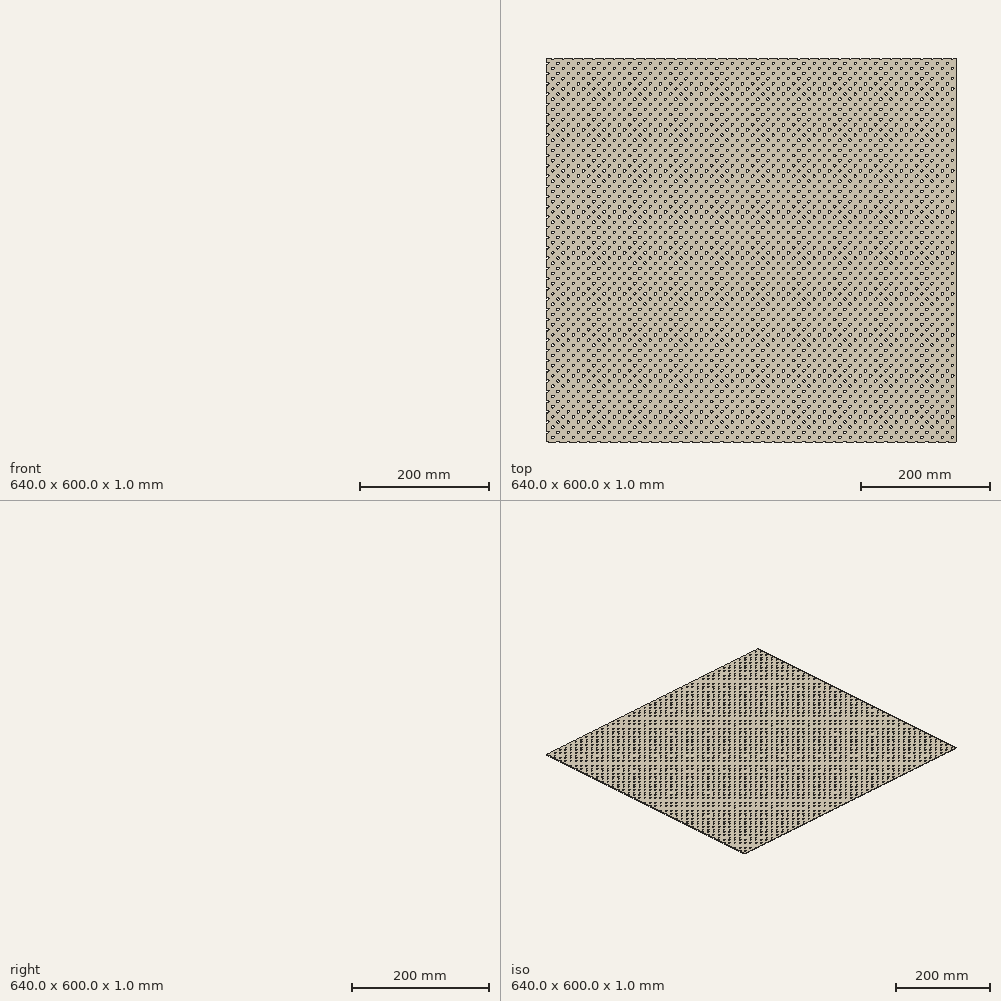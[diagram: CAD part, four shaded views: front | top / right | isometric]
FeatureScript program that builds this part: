
annotation { "Feature Type Name" : "Feature", "Feature Type Description" : "" }
export const myFeature = defineFeature(function(context is Context, id is Id, definition is map)
    precondition{}
    {
        {
            var Q0;
            Q0=qCreatedBy(makeId("Top.planeOp"),FACE);
            var sketch = newSketch(context, id + "F0", { "sketchPlane" : qUnion([Q0])});
            skLineSegment(sketch, "E0.bottom", {"start": v(320, -300) * mm, "end": v(-320, -300) * mm});
            skLineSegment(sketch, "E0.top", {"start": v(320, 300) * mm, "end": v(-320, 300) * mm});
            skLineSegment(sketch, "E0.left", {"start": v(320, -300) * mm, "end": v(320, 300) * mm});
            skLineSegment(sketch, "E0.right", {"start": v(-320, -300) * mm, "end": v(-320, 300) * mm});
            skPoint(sketch, "E0.middle", {"position": v(0, 0) * mm});
            skCircle(sketch, "E1", {"center": v(-317.9, -299.9) * mm, "radius": 2 * mm});
            skCircle(sketch, "E2.0.1.0", {"center": v(-317.9, -283.9) * mm, "radius": 2 * mm});
            skCircle(sketch, "E2.0.2.0", {"center": v(-317.9, -267.9) * mm, "radius": 2 * mm});
            skCircle(sketch, "E2.0.3.0", {"center": v(-317.9, -251.9) * mm, "radius": 2 * mm});
            skCircle(sketch, "E2.0.4.0", {"center": v(-317.9, -235.9) * mm, "radius": 2 * mm});
            skCircle(sketch, "E2.0.5.0", {"center": v(-317.9, -219.9) * mm, "radius": 2 * mm});
            skCircle(sketch, "E2.0.6.0", {"center": v(-317.9, -203.9) * mm, "radius": 2 * mm});
            skCircle(sketch, "E2.0.7.0", {"center": v(-317.9, -187.9) * mm, "radius": 2 * mm});
            skCircle(sketch, "E2.1.0.0", {"center": v(-301.9, -299.9) * mm, "radius": 2 * mm});
            skCircle(sketch, "E2.1.1.0", {"center": v(-301.9, -283.9) * mm, "radius": 2 * mm});
            skCircle(sketch, "E2.1.2.0", {"center": v(-301.9, -267.9) * mm, "radius": 2 * mm});
            skCircle(sketch, "E2.1.3.0", {"center": v(-301.9, -251.9) * mm, "radius": 2 * mm});
            skCircle(sketch, "E2.1.4.0", {"center": v(-301.9, -235.9) * mm, "radius": 2 * mm});
            skCircle(sketch, "E2.1.5.0", {"center": v(-301.9, -219.9) * mm, "radius": 2 * mm});
            skCircle(sketch, "E2.1.6.0", {"center": v(-301.9, -203.9) * mm, "radius": 2 * mm});
            skCircle(sketch, "E2.1.7.0", {"center": v(-301.9, -187.9) * mm, "radius": 2 * mm});
            skCircle(sketch, "E2.2.0.0", {"center": v(-285.9, -299.9) * mm, "radius": 2 * mm});
            skCircle(sketch, "E2.2.1.0", {"center": v(-285.9, -283.9) * mm, "radius": 2 * mm});
            skCircle(sketch, "E2.2.2.0", {"center": v(-285.9, -267.9) * mm, "radius": 2 * mm});
            skCircle(sketch, "E2.2.3.0", {"center": v(-285.9, -251.9) * mm, "radius": 2 * mm});
            skCircle(sketch, "E2.2.4.0", {"center": v(-285.9, -235.9) * mm, "radius": 2 * mm});
            skCircle(sketch, "E2.2.5.0", {"center": v(-285.9, -219.9) * mm, "radius": 2 * mm});
            skCircle(sketch, "E2.2.6.0", {"center": v(-285.9, -203.9) * mm, "radius": 2 * mm});
            skCircle(sketch, "E2.2.7.0", {"center": v(-285.9, -187.9) * mm, "radius": 2 * mm});
            skCircle(sketch, "E2.3.0.0", {"center": v(-269.9, -299.9) * mm, "radius": 2 * mm});
            skCircle(sketch, "E2.3.1.0", {"center": v(-269.9, -283.9) * mm, "radius": 2 * mm});
            skCircle(sketch, "E2.3.2.0", {"center": v(-269.9, -267.9) * mm, "radius": 2 * mm});
            skCircle(sketch, "E2.3.3.0", {"center": v(-269.9, -251.9) * mm, "radius": 2 * mm});
            skCircle(sketch, "E2.3.4.0", {"center": v(-269.9, -235.9) * mm, "radius": 2 * mm});
            skCircle(sketch, "E2.3.5.0", {"center": v(-269.9, -219.9) * mm, "radius": 2 * mm});
            skCircle(sketch, "E2.3.6.0", {"center": v(-269.9, -203.9) * mm, "radius": 2 * mm});
            skCircle(sketch, "E2.3.7.0", {"center": v(-269.9, -187.9) * mm, "radius": 2 * mm});
            skCircle(sketch, "E2.4.0.0", {"center": v(-253.9, -299.9) * mm, "radius": 2 * mm});
            skCircle(sketch, "E2.4.1.0", {"center": v(-253.9, -283.9) * mm, "radius": 2 * mm});
            skCircle(sketch, "E2.4.2.0", {"center": v(-253.9, -267.9) * mm, "radius": 2 * mm});
            skCircle(sketch, "E2.4.3.0", {"center": v(-253.9, -251.9) * mm, "radius": 2 * mm});
            skCircle(sketch, "E2.4.4.0", {"center": v(-253.9, -235.9) * mm, "radius": 2 * mm});
            skCircle(sketch, "E2.4.5.0", {"center": v(-253.9, -219.9) * mm, "radius": 2 * mm});
            skCircle(sketch, "E2.4.6.0", {"center": v(-253.9, -203.9) * mm, "radius": 2 * mm});
            skCircle(sketch, "E2.4.7.0", {"center": v(-253.9, -187.9) * mm, "radius": 2 * mm});
            skCircle(sketch, "E2.5.0.0", {"center": v(-237.9, -299.9) * mm, "radius": 2 * mm});
            skCircle(sketch, "E2.5.1.0", {"center": v(-237.9, -283.9) * mm, "radius": 2 * mm});
            skCircle(sketch, "E2.5.2.0", {"center": v(-237.9, -267.9) * mm, "radius": 2 * mm});
            skCircle(sketch, "E2.5.3.0", {"center": v(-237.9, -251.9) * mm, "radius": 2 * mm});
            skCircle(sketch, "E2.5.4.0", {"center": v(-237.9, -235.9) * mm, "radius": 2 * mm});
            skCircle(sketch, "E2.5.5.0", {"center": v(-237.9, -219.9) * mm, "radius": 2 * mm});
            skCircle(sketch, "E2.5.6.0", {"center": v(-237.9, -203.9) * mm, "radius": 2 * mm});
            skCircle(sketch, "E2.5.7.0", {"center": v(-237.9, -187.9) * mm, "radius": 2 * mm});
            skCircle(sketch, "E2.6.0.0", {"center": v(-221.9, -299.9) * mm, "radius": 2 * mm});
            skCircle(sketch, "E2.6.1.0", {"center": v(-221.9, -283.9) * mm, "radius": 2 * mm});
            skCircle(sketch, "E2.6.2.0", {"center": v(-221.9, -267.9) * mm, "radius": 2 * mm});
            skCircle(sketch, "E2.6.3.0", {"center": v(-221.9, -251.9) * mm, "radius": 2 * mm});
            skCircle(sketch, "E2.6.4.0", {"center": v(-221.9, -235.9) * mm, "radius": 2 * mm});
            skCircle(sketch, "E2.6.5.0", {"center": v(-221.9, -219.9) * mm, "radius": 2 * mm});
            skCircle(sketch, "E2.6.6.0", {"center": v(-221.9, -203.9) * mm, "radius": 2 * mm});
            skCircle(sketch, "E2.6.7.0", {"center": v(-221.9, -187.9) * mm, "radius": 2 * mm});
            skCircle(sketch, "E2.7.0.0", {"center": v(-205.9, -299.9) * mm, "radius": 2 * mm});
            skCircle(sketch, "E2.7.1.0", {"center": v(-205.9, -283.9) * mm, "radius": 2 * mm});
            skCircle(sketch, "E2.7.2.0", {"center": v(-205.9, -267.9) * mm, "radius": 2 * mm});
            skCircle(sketch, "E2.7.3.0", {"center": v(-205.9, -251.9) * mm, "radius": 2 * mm});
            skCircle(sketch, "E2.7.4.0", {"center": v(-205.9, -235.9) * mm, "radius": 2 * mm});
            skCircle(sketch, "E2.7.5.0", {"center": v(-205.9, -219.9) * mm, "radius": 2 * mm});
            skCircle(sketch, "E2.7.6.0", {"center": v(-205.9, -203.9) * mm, "radius": 2 * mm});
            skCircle(sketch, "E2.7.7.0", {"center": v(-205.9, -187.9) * mm, "radius": 2 * mm});
            skCircle(sketch, "E2.8.0.0", {"center": v(-189.9, -299.9) * mm, "radius": 2 * mm});
            skCircle(sketch, "E2.8.1.0", {"center": v(-189.9, -283.9) * mm, "radius": 2 * mm});
            skCircle(sketch, "E2.8.2.0", {"center": v(-189.9, -267.9) * mm, "radius": 2 * mm});
            skCircle(sketch, "E2.8.3.0", {"center": v(-189.9, -251.9) * mm, "radius": 2 * mm});
            skCircle(sketch, "E2.8.4.0", {"center": v(-189.9, -235.9) * mm, "radius": 2 * mm});
            skCircle(sketch, "E2.8.5.0", {"center": v(-189.9, -219.9) * mm, "radius": 2 * mm});
            skCircle(sketch, "E2.8.6.0", {"center": v(-189.9, -203.9) * mm, "radius": 2 * mm});
            skCircle(sketch, "E2.8.7.0", {"center": v(-189.9, -187.9) * mm, "radius": 2 * mm});
            skCircle(sketch, "E2.9.0.0", {"center": v(-173.9, -299.9) * mm, "radius": 2 * mm});
            skCircle(sketch, "E2.9.1.0", {"center": v(-173.9, -283.9) * mm, "radius": 2 * mm});
            skCircle(sketch, "E2.9.2.0", {"center": v(-173.9, -267.9) * mm, "radius": 2 * mm});
            skCircle(sketch, "E2.9.3.0", {"center": v(-173.9, -251.9) * mm, "radius": 2 * mm});
            skCircle(sketch, "E2.9.4.0", {"center": v(-173.9, -235.9) * mm, "radius": 2 * mm});
            skCircle(sketch, "E2.9.5.0", {"center": v(-173.9, -219.9) * mm, "radius": 2 * mm});
            skCircle(sketch, "E2.9.6.0", {"center": v(-173.9, -203.9) * mm, "radius": 2 * mm});
            skCircle(sketch, "E2.9.7.0", {"center": v(-173.9, -187.9) * mm, "radius": 2 * mm});
            skCircle(sketch, "E2.10.0.0", {"center": v(-157.9, -299.9) * mm, "radius": 2 * mm});
            skCircle(sketch, "E2.10.1.0", {"center": v(-157.9, -283.9) * mm, "radius": 2 * mm});
            skCircle(sketch, "E2.10.2.0", {"center": v(-157.9, -267.9) * mm, "radius": 2 * mm});
            skCircle(sketch, "E2.10.3.0", {"center": v(-157.9, -251.9) * mm, "radius": 2 * mm});
            skCircle(sketch, "E2.10.4.0", {"center": v(-157.9, -235.9) * mm, "radius": 2 * mm});
            skCircle(sketch, "E2.10.5.0", {"center": v(-157.9, -219.9) * mm, "radius": 2 * mm});
            skCircle(sketch, "E2.10.6.0", {"center": v(-157.9, -203.9) * mm, "radius": 2 * mm});
            skCircle(sketch, "E2.10.7.0", {"center": v(-157.9, -187.9) * mm, "radius": 2 * mm});
            skCircle(sketch, "E2.11.0.0", {"center": v(-141.9, -299.9) * mm, "radius": 2 * mm});
            skCircle(sketch, "E2.11.1.0", {"center": v(-141.9, -283.9) * mm, "radius": 2 * mm});
            skCircle(sketch, "E2.11.2.0", {"center": v(-141.9, -267.9) * mm, "radius": 2 * mm});
            skCircle(sketch, "E2.11.3.0", {"center": v(-141.9, -251.9) * mm, "radius": 2 * mm});
            skCircle(sketch, "E2.11.4.0", {"center": v(-141.9, -235.9) * mm, "radius": 2 * mm});
            skCircle(sketch, "E2.11.5.0", {"center": v(-141.9, -219.9) * mm, "radius": 2 * mm});
            skCircle(sketch, "E2.11.6.0", {"center": v(-141.9, -203.9) * mm, "radius": 2 * mm});
            skCircle(sketch, "E2.11.7.0", {"center": v(-141.9, -187.9) * mm, "radius": 2 * mm});
            skCircle(sketch, "E2.12.0.0", {"center": v(-125.9, -299.9) * mm, "radius": 2 * mm});
            skCircle(sketch, "E2.12.1.0", {"center": v(-125.9, -283.9) * mm, "radius": 2 * mm});
            skCircle(sketch, "E2.12.2.0", {"center": v(-125.9, -267.9) * mm, "radius": 2 * mm});
            skCircle(sketch, "E2.12.3.0", {"center": v(-125.9, -251.9) * mm, "radius": 2 * mm});
            skCircle(sketch, "E2.12.4.0", {"center": v(-125.9, -235.9) * mm, "radius": 2 * mm});
            skCircle(sketch, "E2.12.5.0", {"center": v(-125.9, -219.9) * mm, "radius": 2 * mm});
            skCircle(sketch, "E2.12.6.0", {"center": v(-125.9, -203.9) * mm, "radius": 2 * mm});
            skCircle(sketch, "E2.12.7.0", {"center": v(-125.9, -187.9) * mm, "radius": 2 * mm});
            skCircle(sketch, "E2.13.0.0", {"center": v(-109.9, -299.9) * mm, "radius": 2 * mm});
            skCircle(sketch, "E2.13.1.0", {"center": v(-109.9, -283.9) * mm, "radius": 2 * mm});
            skCircle(sketch, "E2.13.2.0", {"center": v(-109.9, -267.9) * mm, "radius": 2 * mm});
            skCircle(sketch, "E2.13.3.0", {"center": v(-109.9, -251.9) * mm, "radius": 2 * mm});
            skCircle(sketch, "E2.13.4.0", {"center": v(-109.9, -235.9) * mm, "radius": 2 * mm});
            skCircle(sketch, "E2.13.5.0", {"center": v(-109.9, -219.9) * mm, "radius": 2 * mm});
            skCircle(sketch, "E2.13.6.0", {"center": v(-109.9, -203.9) * mm, "radius": 2 * mm});
            skCircle(sketch, "E2.13.7.0", {"center": v(-109.9, -187.9) * mm, "radius": 2 * mm});
            skCircle(sketch, "E2.14.0.0", {"center": v(-93.9, -299.9) * mm, "radius": 2 * mm});
            skCircle(sketch, "E2.14.1.0", {"center": v(-93.9, -283.9) * mm, "radius": 2 * mm});
            skCircle(sketch, "E2.14.2.0", {"center": v(-93.9, -267.9) * mm, "radius": 2 * mm});
            skCircle(sketch, "E2.14.3.0", {"center": v(-93.9, -251.9) * mm, "radius": 2 * mm});
            skCircle(sketch, "E2.14.4.0", {"center": v(-93.9, -235.9) * mm, "radius": 2 * mm});
            skCircle(sketch, "E2.14.5.0", {"center": v(-93.9, -219.9) * mm, "radius": 2 * mm});
            skCircle(sketch, "E2.14.6.0", {"center": v(-93.9, -203.9) * mm, "radius": 2 * mm});
            skCircle(sketch, "E2.14.7.0", {"center": v(-93.9, -187.9) * mm, "radius": 2 * mm});
            skCircle(sketch, "E2.15.0.0", {"center": v(-77.9, -299.9) * mm, "radius": 2 * mm});
            skCircle(sketch, "E2.15.1.0", {"center": v(-77.9, -283.9) * mm, "radius": 2 * mm});
            skCircle(sketch, "E2.15.2.0", {"center": v(-77.9, -267.9) * mm, "radius": 2 * mm});
            skCircle(sketch, "E2.15.3.0", {"center": v(-77.9, -251.9) * mm, "radius": 2 * mm});
            skCircle(sketch, "E2.15.4.0", {"center": v(-77.9, -235.9) * mm, "radius": 2 * mm});
            skCircle(sketch, "E2.15.5.0", {"center": v(-77.9, -219.9) * mm, "radius": 2 * mm});
            skCircle(sketch, "E2.15.6.0", {"center": v(-77.9, -203.9) * mm, "radius": 2 * mm});
            skCircle(sketch, "E2.15.7.0", {"center": v(-77.9, -187.9) * mm, "radius": 2 * mm});
            skCircle(sketch, "E2.16.0.0", {"center": v(-61.9, -299.9) * mm, "radius": 2 * mm});
            skCircle(sketch, "E2.16.1.0", {"center": v(-61.9, -283.9) * mm, "radius": 2 * mm});
            skCircle(sketch, "E2.16.2.0", {"center": v(-61.9, -267.9) * mm, "radius": 2 * mm});
            skCircle(sketch, "E2.16.3.0", {"center": v(-61.9, -251.9) * mm, "radius": 2 * mm});
            skCircle(sketch, "E2.16.4.0", {"center": v(-61.9, -235.9) * mm, "radius": 2 * mm});
            skCircle(sketch, "E2.16.5.0", {"center": v(-61.9, -219.9) * mm, "radius": 2 * mm});
            skCircle(sketch, "E2.16.6.0", {"center": v(-61.9, -203.9) * mm, "radius": 2 * mm});
            skCircle(sketch, "E2.16.7.0", {"center": v(-61.9, -187.9) * mm, "radius": 2 * mm});
            skCircle(sketch, "E2.17.0.0", {"center": v(-45.9, -299.9) * mm, "radius": 2 * mm});
            skCircle(sketch, "E2.17.1.0", {"center": v(-45.9, -283.9) * mm, "radius": 2 * mm});
            skCircle(sketch, "E2.17.2.0", {"center": v(-45.9, -267.9) * mm, "radius": 2 * mm});
            skCircle(sketch, "E2.17.3.0", {"center": v(-45.9, -251.9) * mm, "radius": 2 * mm});
            skCircle(sketch, "E2.17.4.0", {"center": v(-45.9, -235.9) * mm, "radius": 2 * mm});
            skCircle(sketch, "E2.17.5.0", {"center": v(-45.9, -219.9) * mm, "radius": 2 * mm});
            skCircle(sketch, "E2.17.6.0", {"center": v(-45.9, -203.9) * mm, "radius": 2 * mm});
            skCircle(sketch, "E2.17.7.0", {"center": v(-45.9, -187.9) * mm, "radius": 2 * mm});
            skCircle(sketch, "E2.18.0.0", {"center": v(-29.9, -299.9) * mm, "radius": 2 * mm});
            skCircle(sketch, "E2.18.1.0", {"center": v(-29.9, -283.9) * mm, "radius": 2 * mm});
            skCircle(sketch, "E2.18.2.0", {"center": v(-29.9, -267.9) * mm, "radius": 2 * mm});
            skCircle(sketch, "E2.18.3.0", {"center": v(-29.9, -251.9) * mm, "radius": 2 * mm});
            skCircle(sketch, "E2.18.4.0", {"center": v(-29.9, -235.9) * mm, "radius": 2 * mm});
            skCircle(sketch, "E2.18.5.0", {"center": v(-29.9, -219.9) * mm, "radius": 2 * mm});
            skCircle(sketch, "E2.18.6.0", {"center": v(-29.9, -203.9) * mm, "radius": 2 * mm});
            skCircle(sketch, "E2.18.7.0", {"center": v(-29.9, -187.9) * mm, "radius": 2 * mm});
            skCircle(sketch, "E2.19.0.0", {"center": v(-13.9, -299.9) * mm, "radius": 2 * mm});
            skCircle(sketch, "E2.19.1.0", {"center": v(-13.9, -283.9) * mm, "radius": 2 * mm});
            skCircle(sketch, "E2.19.2.0", {"center": v(-13.9, -267.9) * mm, "radius": 2 * mm});
            skCircle(sketch, "E2.19.3.0", {"center": v(-13.9, -251.9) * mm, "radius": 2 * mm});
            skCircle(sketch, "E2.19.4.0", {"center": v(-13.9, -235.9) * mm, "radius": 2 * mm});
            skCircle(sketch, "E2.19.5.0", {"center": v(-13.9, -219.9) * mm, "radius": 2 * mm});
            skCircle(sketch, "E2.19.6.0", {"center": v(-13.9, -203.9) * mm, "radius": 2 * mm});
            skCircle(sketch, "E2.19.7.0", {"center": v(-13.9, -187.9) * mm, "radius": 2 * mm});
            skCircle(sketch, "E2.20.0.0", {"center": v(2.1, -299.9) * mm, "radius": 2 * mm});
            skCircle(sketch, "E2.20.1.0", {"center": v(2.1, -283.9) * mm, "radius": 2 * mm});
            skCircle(sketch, "E2.20.2.0", {"center": v(2.1, -267.9) * mm, "radius": 2 * mm});
            skCircle(sketch, "E2.20.3.0", {"center": v(2.1, -251.9) * mm, "radius": 2 * mm});
            skCircle(sketch, "E2.20.4.0", {"center": v(2.1, -235.9) * mm, "radius": 2 * mm});
            skCircle(sketch, "E2.20.5.0", {"center": v(2.1, -219.9) * mm, "radius": 2 * mm});
            skCircle(sketch, "E2.20.6.0", {"center": v(2.1, -203.9) * mm, "radius": 2 * mm});
            skCircle(sketch, "E2.20.7.0", {"center": v(2.1, -187.9) * mm, "radius": 2 * mm});
            skCircle(sketch, "E2.21.0.0", {"center": v(18.1, -299.9) * mm, "radius": 2 * mm});
            skCircle(sketch, "E2.21.1.0", {"center": v(18.1, -283.9) * mm, "radius": 2 * mm});
            skCircle(sketch, "E2.21.2.0", {"center": v(18.1, -267.9) * mm, "radius": 2 * mm});
            skCircle(sketch, "E2.21.3.0", {"center": v(18.1, -251.9) * mm, "radius": 2 * mm});
            skCircle(sketch, "E2.21.4.0", {"center": v(18.1, -235.9) * mm, "radius": 2 * mm});
            skCircle(sketch, "E2.21.5.0", {"center": v(18.1, -219.9) * mm, "radius": 2 * mm});
            skCircle(sketch, "E2.21.6.0", {"center": v(18.1, -203.9) * mm, "radius": 2 * mm});
            skCircle(sketch, "E2.21.7.0", {"center": v(18.1, -187.9) * mm, "radius": 2 * mm});
            skCircle(sketch, "E2.22.0.0", {"center": v(34.1, -299.9) * mm, "radius": 2 * mm});
            skCircle(sketch, "E2.22.1.0", {"center": v(34.1, -283.9) * mm, "radius": 2 * mm});
            skCircle(sketch, "E2.22.2.0", {"center": v(34.1, -267.9) * mm, "radius": 2 * mm});
            skCircle(sketch, "E2.22.3.0", {"center": v(34.1, -251.9) * mm, "radius": 2 * mm});
            skCircle(sketch, "E2.22.4.0", {"center": v(34.1, -235.9) * mm, "radius": 2 * mm});
            skCircle(sketch, "E2.22.5.0", {"center": v(34.1, -219.9) * mm, "radius": 2 * mm});
            skCircle(sketch, "E2.22.6.0", {"center": v(34.1, -203.9) * mm, "radius": 2 * mm});
            skCircle(sketch, "E2.22.7.0", {"center": v(34.1, -187.9) * mm, "radius": 2 * mm});
            skCircle(sketch, "E2.23.0.0", {"center": v(50.1, -299.9) * mm, "radius": 2 * mm});
            skCircle(sketch, "E2.23.1.0", {"center": v(50.1, -283.9) * mm, "radius": 2 * mm});
            skCircle(sketch, "E2.23.2.0", {"center": v(50.1, -267.9) * mm, "radius": 2 * mm});
            skCircle(sketch, "E2.23.3.0", {"center": v(50.1, -251.9) * mm, "radius": 2 * mm});
            skCircle(sketch, "E2.23.4.0", {"center": v(50.1, -235.9) * mm, "radius": 2 * mm});
            skCircle(sketch, "E2.23.5.0", {"center": v(50.1, -219.9) * mm, "radius": 2 * mm});
            skCircle(sketch, "E2.23.6.0", {"center": v(50.1, -203.9) * mm, "radius": 2 * mm});
            skCircle(sketch, "E2.23.7.0", {"center": v(50.1, -187.9) * mm, "radius": 2 * mm});
            skCircle(sketch, "E2.24.0.0", {"center": v(66.1, -299.9) * mm, "radius": 2 * mm});
            skCircle(sketch, "E2.24.1.0", {"center": v(66.1, -283.9) * mm, "radius": 2 * mm});
            skCircle(sketch, "E2.24.2.0", {"center": v(66.1, -267.9) * mm, "radius": 2 * mm});
            skCircle(sketch, "E2.24.3.0", {"center": v(66.1, -251.9) * mm, "radius": 2 * mm});
            skCircle(sketch, "E2.24.4.0", {"center": v(66.1, -235.9) * mm, "radius": 2 * mm});
            skCircle(sketch, "E2.24.5.0", {"center": v(66.1, -219.9) * mm, "radius": 2 * mm});
            skCircle(sketch, "E2.24.6.0", {"center": v(66.1, -203.9) * mm, "radius": 2 * mm});
            skCircle(sketch, "E2.24.7.0", {"center": v(66.1, -187.9) * mm, "radius": 2 * mm});
            skCircle(sketch, "E2.25.0.0", {"center": v(82.1, -299.9) * mm, "radius": 2 * mm});
            skCircle(sketch, "E2.25.1.0", {"center": v(82.1, -283.9) * mm, "radius": 2 * mm});
            skCircle(sketch, "E2.25.2.0", {"center": v(82.1, -267.9) * mm, "radius": 2 * mm});
            skCircle(sketch, "E2.25.3.0", {"center": v(82.1, -251.9) * mm, "radius": 2 * mm});
            skCircle(sketch, "E2.25.4.0", {"center": v(82.1, -235.9) * mm, "radius": 2 * mm});
            skCircle(sketch, "E2.25.5.0", {"center": v(82.1, -219.9) * mm, "radius": 2 * mm});
            skCircle(sketch, "E2.25.6.0", {"center": v(82.1, -203.9) * mm, "radius": 2 * mm});
            skCircle(sketch, "E2.25.7.0", {"center": v(82.1, -187.9) * mm, "radius": 2 * mm});
            skCircle(sketch, "E2.26.0.0", {"center": v(98.1, -299.9) * mm, "radius": 2 * mm});
            skCircle(sketch, "E2.26.1.0", {"center": v(98.1, -283.9) * mm, "radius": 2 * mm});
            skCircle(sketch, "E2.26.2.0", {"center": v(98.1, -267.9) * mm, "radius": 2 * mm});
            skCircle(sketch, "E2.26.3.0", {"center": v(98.1, -251.9) * mm, "radius": 2 * mm});
            skCircle(sketch, "E2.26.4.0", {"center": v(98.1, -235.9) * mm, "radius": 2 * mm});
            skCircle(sketch, "E2.26.5.0", {"center": v(98.1, -219.9) * mm, "radius": 2 * mm});
            skCircle(sketch, "E2.26.6.0", {"center": v(98.1, -203.9) * mm, "radius": 2 * mm});
            skCircle(sketch, "E2.26.7.0", {"center": v(98.1, -187.9) * mm, "radius": 2 * mm});
            skCircle(sketch, "E2.27.0.0", {"center": v(114.1, -299.9) * mm, "radius": 2 * mm});
            skCircle(sketch, "E2.27.1.0", {"center": v(114.1, -283.9) * mm, "radius": 2 * mm});
            skCircle(sketch, "E2.27.2.0", {"center": v(114.1, -267.9) * mm, "radius": 2 * mm});
            skCircle(sketch, "E2.27.3.0", {"center": v(114.1, -251.9) * mm, "radius": 2 * mm});
            skCircle(sketch, "E2.27.4.0", {"center": v(114.1, -235.9) * mm, "radius": 2 * mm});
            skCircle(sketch, "E2.27.5.0", {"center": v(114.1, -219.9) * mm, "radius": 2 * mm});
            skCircle(sketch, "E2.27.6.0", {"center": v(114.1, -203.9) * mm, "radius": 2 * mm});
            skCircle(sketch, "E2.27.7.0", {"center": v(114.1, -187.9) * mm, "radius": 2 * mm});
            skCircle(sketch, "E2.28.0.0", {"center": v(130.1, -299.9) * mm, "radius": 2 * mm});
            skCircle(sketch, "E2.28.1.0", {"center": v(130.1, -283.9) * mm, "radius": 2 * mm});
            skCircle(sketch, "E2.28.2.0", {"center": v(130.1, -267.9) * mm, "radius": 2 * mm});
            skCircle(sketch, "E2.28.3.0", {"center": v(130.1, -251.9) * mm, "radius": 2 * mm});
            skCircle(sketch, "E2.28.4.0", {"center": v(130.1, -235.9) * mm, "radius": 2 * mm});
            skCircle(sketch, "E2.28.5.0", {"center": v(130.1, -219.9) * mm, "radius": 2 * mm});
            skCircle(sketch, "E2.28.6.0", {"center": v(130.1, -203.9) * mm, "radius": 2 * mm});
            skCircle(sketch, "E2.28.7.0", {"center": v(130.1, -187.9) * mm, "radius": 2 * mm});
            skCircle(sketch, "E2.29.0.0", {"center": v(146.1, -299.9) * mm, "radius": 2 * mm});
            skCircle(sketch, "E2.29.1.0", {"center": v(146.1, -283.9) * mm, "radius": 2 * mm});
            skCircle(sketch, "E2.29.2.0", {"center": v(146.1, -267.9) * mm, "radius": 2 * mm});
            skCircle(sketch, "E2.29.3.0", {"center": v(146.1, -251.9) * mm, "radius": 2 * mm});
            skCircle(sketch, "E2.29.4.0", {"center": v(146.1, -235.9) * mm, "radius": 2 * mm});
            skCircle(sketch, "E2.29.5.0", {"center": v(146.1, -219.9) * mm, "radius": 2 * mm});
            skCircle(sketch, "E2.29.6.0", {"center": v(146.1, -203.9) * mm, "radius": 2 * mm});
            skCircle(sketch, "E2.29.7.0", {"center": v(146.1, -187.9) * mm, "radius": 2 * mm});
            skCircle(sketch, "E2.30.0.0", {"center": v(162.1, -299.9) * mm, "radius": 2 * mm});
            skCircle(sketch, "E2.30.1.0", {"center": v(162.1, -283.9) * mm, "radius": 2 * mm});
            skCircle(sketch, "E2.30.2.0", {"center": v(162.1, -267.9) * mm, "radius": 2 * mm});
            skCircle(sketch, "E2.30.3.0", {"center": v(162.1, -251.9) * mm, "radius": 2 * mm});
            skCircle(sketch, "E2.30.4.0", {"center": v(162.1, -235.9) * mm, "radius": 2 * mm});
            skCircle(sketch, "E2.30.5.0", {"center": v(162.1, -219.9) * mm, "radius": 2 * mm});
            skCircle(sketch, "E2.30.6.0", {"center": v(162.1, -203.9) * mm, "radius": 2 * mm});
            skCircle(sketch, "E2.30.7.0", {"center": v(162.1, -187.9) * mm, "radius": 2 * mm});
            skCircle(sketch, "E2.31.0.0", {"center": v(178.1, -299.9) * mm, "radius": 2 * mm});
            skCircle(sketch, "E2.31.1.0", {"center": v(178.1, -283.9) * mm, "radius": 2 * mm});
            skCircle(sketch, "E2.31.2.0", {"center": v(178.1, -267.9) * mm, "radius": 2 * mm});
            skCircle(sketch, "E2.31.3.0", {"center": v(178.1, -251.9) * mm, "radius": 2 * mm});
            skCircle(sketch, "E2.31.4.0", {"center": v(178.1, -235.9) * mm, "radius": 2 * mm});
            skCircle(sketch, "E2.31.5.0", {"center": v(178.1, -219.9) * mm, "radius": 2 * mm});
            skCircle(sketch, "E2.31.6.0", {"center": v(178.1, -203.9) * mm, "radius": 2 * mm});
            skCircle(sketch, "E2.31.7.0", {"center": v(178.1, -187.9) * mm, "radius": 2 * mm});
            skCircle(sketch, "E2.32.0.0", {"center": v(194.1, -299.9) * mm, "radius": 2 * mm});
            skCircle(sketch, "E2.32.1.0", {"center": v(194.1, -283.9) * mm, "radius": 2 * mm});
            skCircle(sketch, "E2.32.2.0", {"center": v(194.1, -267.9) * mm, "radius": 2 * mm});
            skCircle(sketch, "E2.32.3.0", {"center": v(194.1, -251.9) * mm, "radius": 2 * mm});
            skCircle(sketch, "E2.32.4.0", {"center": v(194.1, -235.9) * mm, "radius": 2 * mm});
            skCircle(sketch, "E2.32.5.0", {"center": v(194.1, -219.9) * mm, "radius": 2 * mm});
            skCircle(sketch, "E2.32.6.0", {"center": v(194.1, -203.9) * mm, "radius": 2 * mm});
            skCircle(sketch, "E2.32.7.0", {"center": v(194.1, -187.9) * mm, "radius": 2 * mm});
            skCircle(sketch, "E2.33.0.0", {"center": v(210.1, -299.9) * mm, "radius": 2 * mm});
            skCircle(sketch, "E2.33.1.0", {"center": v(210.1, -283.9) * mm, "radius": 2 * mm});
            skCircle(sketch, "E2.33.2.0", {"center": v(210.1, -267.9) * mm, "radius": 2 * mm});
            skCircle(sketch, "E2.33.3.0", {"center": v(210.1, -251.9) * mm, "radius": 2 * mm});
            skCircle(sketch, "E2.33.4.0", {"center": v(210.1, -235.9) * mm, "radius": 2 * mm});
            skCircle(sketch, "E2.33.5.0", {"center": v(210.1, -219.9) * mm, "radius": 2 * mm});
            skCircle(sketch, "E2.33.6.0", {"center": v(210.1, -203.9) * mm, "radius": 2 * mm});
            skCircle(sketch, "E2.33.7.0", {"center": v(210.1, -187.9) * mm, "radius": 2 * mm});
            skCircle(sketch, "E2.34.0.0", {"center": v(226.1, -299.9) * mm, "radius": 2 * mm});
            skCircle(sketch, "E2.34.1.0", {"center": v(226.1, -283.9) * mm, "radius": 2 * mm});
            skCircle(sketch, "E2.34.2.0", {"center": v(226.1, -267.9) * mm, "radius": 2 * mm});
            skCircle(sketch, "E2.34.3.0", {"center": v(226.1, -251.9) * mm, "radius": 2 * mm});
            skCircle(sketch, "E2.34.4.0", {"center": v(226.1, -235.9) * mm, "radius": 2 * mm});
            skCircle(sketch, "E2.34.5.0", {"center": v(226.1, -219.9) * mm, "radius": 2 * mm});
            skCircle(sketch, "E2.34.6.0", {"center": v(226.1, -203.9) * mm, "radius": 2 * mm});
            skCircle(sketch, "E2.34.7.0", {"center": v(226.1, -187.9) * mm, "radius": 2 * mm});
            skCircle(sketch, "E2.35.0.0", {"center": v(242.1, -299.9) * mm, "radius": 2 * mm});
            skCircle(sketch, "E2.35.1.0", {"center": v(242.1, -283.9) * mm, "radius": 2 * mm});
            skCircle(sketch, "E2.35.2.0", {"center": v(242.1, -267.9) * mm, "radius": 2 * mm});
            skCircle(sketch, "E2.35.3.0", {"center": v(242.1, -251.9) * mm, "radius": 2 * mm});
            skCircle(sketch, "E2.35.4.0", {"center": v(242.1, -235.9) * mm, "radius": 2 * mm});
            skCircle(sketch, "E2.35.5.0", {"center": v(242.1, -219.9) * mm, "radius": 2 * mm});
            skCircle(sketch, "E2.35.6.0", {"center": v(242.1, -203.9) * mm, "radius": 2 * mm});
            skCircle(sketch, "E2.35.7.0", {"center": v(242.1, -187.9) * mm, "radius": 2 * mm});
            skCircle(sketch, "E2.36.0.0", {"center": v(258.1, -299.9) * mm, "radius": 2 * mm});
            skCircle(sketch, "E2.36.1.0", {"center": v(258.1, -283.9) * mm, "radius": 2 * mm});
            skCircle(sketch, "E2.36.2.0", {"center": v(258.1, -267.9) * mm, "radius": 2 * mm});
            skCircle(sketch, "E2.36.3.0", {"center": v(258.1, -251.9) * mm, "radius": 2 * mm});
            skCircle(sketch, "E2.36.4.0", {"center": v(258.1, -235.9) * mm, "radius": 2 * mm});
            skCircle(sketch, "E2.36.5.0", {"center": v(258.1, -219.9) * mm, "radius": 2 * mm});
            skCircle(sketch, "E2.36.6.0", {"center": v(258.1, -203.9) * mm, "radius": 2 * mm});
            skCircle(sketch, "E2.36.7.0", {"center": v(258.1, -187.9) * mm, "radius": 2 * mm});
            skCircle(sketch, "E2.37.0.0", {"center": v(274.1, -299.9) * mm, "radius": 2 * mm});
            skCircle(sketch, "E2.37.1.0", {"center": v(274.1, -283.9) * mm, "radius": 2 * mm});
            skCircle(sketch, "E2.37.2.0", {"center": v(274.1, -267.9) * mm, "radius": 2 * mm});
            skCircle(sketch, "E2.37.3.0", {"center": v(274.1, -251.9) * mm, "radius": 2 * mm});
            skCircle(sketch, "E2.37.4.0", {"center": v(274.1, -235.9) * mm, "radius": 2 * mm});
            skCircle(sketch, "E2.37.5.0", {"center": v(274.1, -219.9) * mm, "radius": 2 * mm});
            skCircle(sketch, "E2.37.6.0", {"center": v(274.1, -203.9) * mm, "radius": 2 * mm});
            skCircle(sketch, "E2.37.7.0", {"center": v(274.1, -187.9) * mm, "radius": 2 * mm});
            skCircle(sketch, "E2.38.0.0", {"center": v(290.1, -299.9) * mm, "radius": 2 * mm});
            skCircle(sketch, "E2.38.1.0", {"center": v(290.1, -283.9) * mm, "radius": 2 * mm});
            skCircle(sketch, "E2.38.2.0", {"center": v(290.1, -267.9) * mm, "radius": 2 * mm});
            skCircle(sketch, "E2.38.3.0", {"center": v(290.1, -251.9) * mm, "radius": 2 * mm});
            skCircle(sketch, "E2.38.4.0", {"center": v(290.1, -235.9) * mm, "radius": 2 * mm});
            skCircle(sketch, "E2.38.5.0", {"center": v(290.1, -219.9) * mm, "radius": 2 * mm});
            skCircle(sketch, "E2.38.6.0", {"center": v(290.1, -203.9) * mm, "radius": 2 * mm});
            skCircle(sketch, "E2.38.7.0", {"center": v(290.1, -187.9) * mm, "radius": 2 * mm});
            skCircle(sketch, "E2.39.0.0", {"center": v(306.1, -299.9) * mm, "radius": 2 * mm});
            skCircle(sketch, "E2.39.1.0", {"center": v(306.1, -283.9) * mm, "radius": 2 * mm});
            skCircle(sketch, "E2.39.2.0", {"center": v(306.1, -267.9) * mm, "radius": 2 * mm});
            skCircle(sketch, "E2.39.3.0", {"center": v(306.1, -251.9) * mm, "radius": 2 * mm});
            skCircle(sketch, "E2.39.4.0", {"center": v(306.1, -235.9) * mm, "radius": 2 * mm});
            skCircle(sketch, "E2.39.5.0", {"center": v(306.1, -219.9) * mm, "radius": 2 * mm});
            skCircle(sketch, "E2.39.6.0", {"center": v(306.1, -203.9) * mm, "radius": 2 * mm});
            skCircle(sketch, "E2.39.7.0", {"center": v(306.1, -187.9) * mm, "radius": 2 * mm});
            skLineSegment(sketch, "E2.direction1", {"start": v(-317.9, -299.9) * mm, "end": v(-301.9, -299.9) * mm, "construction": true});
            skLineSegment(sketch, "E2.direction2", {"start": v(-317.9, -299.9) * mm, "end": v(-317.9, -283.9) * mm, "construction": true});
            skCircle(sketch, "E3", {"center": v(-309.9, -291.9) * mm, "radius": 2 * mm});
            skCircle(sketch, "E4.0.1.0", {"center": v(-309.9, -275.9) * mm, "radius": 2 * mm});
            skCircle(sketch, "E4.0.2.0", {"center": v(-309.9, -259.9) * mm, "radius": 2 * mm});
            skCircle(sketch, "E4.0.3.0", {"center": v(-309.9, -243.9) * mm, "radius": 2 * mm});
            skCircle(sketch, "E4.0.4.0", {"center": v(-309.9, -227.9) * mm, "radius": 2 * mm});
            skCircle(sketch, "E4.0.5.0", {"center": v(-309.9, -211.9) * mm, "radius": 2 * mm});
            skCircle(sketch, "E4.1.0.0", {"center": v(-293.9, -291.9) * mm, "radius": 2 * mm});
            skCircle(sketch, "E4.1.1.0", {"center": v(-293.9, -275.9) * mm, "radius": 2 * mm});
            skCircle(sketch, "E4.1.2.0", {"center": v(-293.9, -259.9) * mm, "radius": 2 * mm});
            skCircle(sketch, "E4.1.3.0", {"center": v(-293.9, -243.9) * mm, "radius": 2 * mm});
            skCircle(sketch, "E4.1.4.0", {"center": v(-293.9, -227.9) * mm, "radius": 2 * mm});
            skCircle(sketch, "E4.1.5.0", {"center": v(-293.9, -211.9) * mm, "radius": 2 * mm});
            skCircle(sketch, "E4.2.0.0", {"center": v(-277.9, -291.9) * mm, "radius": 2 * mm});
            skCircle(sketch, "E4.2.1.0", {"center": v(-277.9, -275.9) * mm, "radius": 2 * mm});
            skCircle(sketch, "E4.2.2.0", {"center": v(-277.9, -259.9) * mm, "radius": 2 * mm});
            skCircle(sketch, "E4.2.3.0", {"center": v(-277.9, -243.9) * mm, "radius": 2 * mm});
            skCircle(sketch, "E4.2.4.0", {"center": v(-277.9, -227.9) * mm, "radius": 2 * mm});
            skCircle(sketch, "E4.2.5.0", {"center": v(-277.9, -211.9) * mm, "radius": 2 * mm});
            skCircle(sketch, "E4.3.0.0", {"center": v(-261.9, -291.9) * mm, "radius": 2 * mm});
            skCircle(sketch, "E4.3.1.0", {"center": v(-261.9, -275.9) * mm, "radius": 2 * mm});
            skCircle(sketch, "E4.3.2.0", {"center": v(-261.9, -259.9) * mm, "radius": 2 * mm});
            skCircle(sketch, "E4.3.3.0", {"center": v(-261.9, -243.9) * mm, "radius": 2 * mm});
            skCircle(sketch, "E4.3.4.0", {"center": v(-261.9, -227.9) * mm, "radius": 2 * mm});
            skCircle(sketch, "E4.3.5.0", {"center": v(-261.9, -211.9) * mm, "radius": 2 * mm});
            skCircle(sketch, "E4.4.0.0", {"center": v(-245.9, -291.9) * mm, "radius": 2 * mm});
            skCircle(sketch, "E4.4.1.0", {"center": v(-245.9, -275.9) * mm, "radius": 2 * mm});
            skCircle(sketch, "E4.4.2.0", {"center": v(-245.9, -259.9) * mm, "radius": 2 * mm});
            skCircle(sketch, "E4.4.3.0", {"center": v(-245.9, -243.9) * mm, "radius": 2 * mm});
            skCircle(sketch, "E4.4.4.0", {"center": v(-245.9, -227.9) * mm, "radius": 2 * mm});
            skCircle(sketch, "E4.4.5.0", {"center": v(-245.9, -211.9) * mm, "radius": 2 * mm});
            skCircle(sketch, "E4.5.0.0", {"center": v(-229.9, -291.9) * mm, "radius": 2 * mm});
            skCircle(sketch, "E4.5.1.0", {"center": v(-229.9, -275.9) * mm, "radius": 2 * mm});
            skCircle(sketch, "E4.5.2.0", {"center": v(-229.9, -259.9) * mm, "radius": 2 * mm});
            skCircle(sketch, "E4.5.3.0", {"center": v(-229.9, -243.9) * mm, "radius": 2 * mm});
            skCircle(sketch, "E4.5.4.0", {"center": v(-229.9, -227.9) * mm, "radius": 2 * mm});
            skCircle(sketch, "E4.5.5.0", {"center": v(-229.9, -211.9) * mm, "radius": 2 * mm});
            skCircle(sketch, "E4.6.0.0", {"center": v(-213.9, -291.9) * mm, "radius": 2 * mm});
            skCircle(sketch, "E4.6.1.0", {"center": v(-213.9, -275.9) * mm, "radius": 2 * mm});
            skCircle(sketch, "E4.6.2.0", {"center": v(-213.9, -259.9) * mm, "radius": 2 * mm});
            skCircle(sketch, "E4.6.3.0", {"center": v(-213.9, -243.9) * mm, "radius": 2 * mm});
            skCircle(sketch, "E4.6.4.0", {"center": v(-213.9, -227.9) * mm, "radius": 2 * mm});
            skCircle(sketch, "E4.6.5.0", {"center": v(-213.9, -211.9) * mm, "radius": 2 * mm});
            skCircle(sketch, "E4.7.0.0", {"center": v(-197.9, -291.9) * mm, "radius": 2 * mm});
            skCircle(sketch, "E4.7.1.0", {"center": v(-197.9, -275.9) * mm, "radius": 2 * mm});
            skCircle(sketch, "E4.7.2.0", {"center": v(-197.9, -259.9) * mm, "radius": 2 * mm});
            skCircle(sketch, "E4.7.3.0", {"center": v(-197.9, -243.9) * mm, "radius": 2 * mm});
            skCircle(sketch, "E4.7.4.0", {"center": v(-197.9, -227.9) * mm, "radius": 2 * mm});
            skCircle(sketch, "E4.7.5.0", {"center": v(-197.9, -211.9) * mm, "radius": 2 * mm});
            skCircle(sketch, "E4.8.0.0", {"center": v(-181.9, -291.9) * mm, "radius": 2 * mm});
            skCircle(sketch, "E4.8.1.0", {"center": v(-181.9, -275.9) * mm, "radius": 2 * mm});
            skCircle(sketch, "E4.8.2.0", {"center": v(-181.9, -259.9) * mm, "radius": 2 * mm});
            skCircle(sketch, "E4.8.3.0", {"center": v(-181.9, -243.9) * mm, "radius": 2 * mm});
            skCircle(sketch, "E4.8.4.0", {"center": v(-181.9, -227.9) * mm, "radius": 2 * mm});
            skCircle(sketch, "E4.8.5.0", {"center": v(-181.9, -211.9) * mm, "radius": 2 * mm});
            skCircle(sketch, "E4.9.0.0", {"center": v(-165.9, -291.9) * mm, "radius": 2 * mm});
            skCircle(sketch, "E4.9.1.0", {"center": v(-165.9, -275.9) * mm, "radius": 2 * mm});
            skCircle(sketch, "E4.9.2.0", {"center": v(-165.9, -259.9) * mm, "radius": 2 * mm});
            skCircle(sketch, "E4.9.3.0", {"center": v(-165.9, -243.9) * mm, "radius": 2 * mm});
            skCircle(sketch, "E4.9.4.0", {"center": v(-165.9, -227.9) * mm, "radius": 2 * mm});
            skCircle(sketch, "E4.9.5.0", {"center": v(-165.9, -211.9) * mm, "radius": 2 * mm});
            skCircle(sketch, "E4.10.0.0", {"center": v(-149.9, -291.9) * mm, "radius": 2 * mm});
            skCircle(sketch, "E4.10.1.0", {"center": v(-149.9, -275.9) * mm, "radius": 2 * mm});
            skCircle(sketch, "E4.10.2.0", {"center": v(-149.9, -259.9) * mm, "radius": 2 * mm});
            skCircle(sketch, "E4.10.3.0", {"center": v(-149.9, -243.9) * mm, "radius": 2 * mm});
            skCircle(sketch, "E4.10.4.0", {"center": v(-149.9, -227.9) * mm, "radius": 2 * mm});
            skCircle(sketch, "E4.10.5.0", {"center": v(-149.9, -211.9) * mm, "radius": 2 * mm});
            skCircle(sketch, "E4.11.0.0", {"center": v(-133.9, -291.9) * mm, "radius": 2 * mm});
            skCircle(sketch, "E4.11.1.0", {"center": v(-133.9, -275.9) * mm, "radius": 2 * mm});
            skCircle(sketch, "E4.11.2.0", {"center": v(-133.9, -259.9) * mm, "radius": 2 * mm});
            skCircle(sketch, "E4.11.3.0", {"center": v(-133.9, -243.9) * mm, "radius": 2 * mm});
            skCircle(sketch, "E4.11.4.0", {"center": v(-133.9, -227.9) * mm, "radius": 2 * mm});
            skCircle(sketch, "E4.11.5.0", {"center": v(-133.9, -211.9) * mm, "radius": 2 * mm});
            skCircle(sketch, "E4.12.0.0", {"center": v(-117.9, -291.9) * mm, "radius": 2 * mm});
            skCircle(sketch, "E4.12.1.0", {"center": v(-117.9, -275.9) * mm, "radius": 2 * mm});
            skCircle(sketch, "E4.12.2.0", {"center": v(-117.9, -259.9) * mm, "radius": 2 * mm});
            skCircle(sketch, "E4.12.3.0", {"center": v(-117.9, -243.9) * mm, "radius": 2 * mm});
            skCircle(sketch, "E4.12.4.0", {"center": v(-117.9, -227.9) * mm, "radius": 2 * mm});
            skCircle(sketch, "E4.12.5.0", {"center": v(-117.9, -211.9) * mm, "radius": 2 * mm});
            skCircle(sketch, "E4.13.0.0", {"center": v(-101.9, -291.9) * mm, "radius": 2 * mm});
            skCircle(sketch, "E4.13.1.0", {"center": v(-101.9, -275.9) * mm, "radius": 2 * mm});
            skCircle(sketch, "E4.13.2.0", {"center": v(-101.9, -259.9) * mm, "radius": 2 * mm});
            skCircle(sketch, "E4.13.3.0", {"center": v(-101.9, -243.9) * mm, "radius": 2 * mm});
            skCircle(sketch, "E4.13.4.0", {"center": v(-101.9, -227.9) * mm, "radius": 2 * mm});
            skCircle(sketch, "E4.13.5.0", {"center": v(-101.9, -211.9) * mm, "radius": 2 * mm});
            skCircle(sketch, "E4.14.0.0", {"center": v(-85.9, -291.9) * mm, "radius": 2 * mm});
            skCircle(sketch, "E4.14.1.0", {"center": v(-85.9, -275.9) * mm, "radius": 2 * mm});
            skCircle(sketch, "E4.14.2.0", {"center": v(-85.9, -259.9) * mm, "radius": 2 * mm});
            skCircle(sketch, "E4.14.3.0", {"center": v(-85.9, -243.9) * mm, "radius": 2 * mm});
            skCircle(sketch, "E4.14.4.0", {"center": v(-85.9, -227.9) * mm, "radius": 2 * mm});
            skCircle(sketch, "E4.14.5.0", {"center": v(-85.9, -211.9) * mm, "radius": 2 * mm});
            skCircle(sketch, "E4.15.0.0", {"center": v(-69.9, -291.9) * mm, "radius": 2 * mm});
            skCircle(sketch, "E4.15.1.0", {"center": v(-69.9, -275.9) * mm, "radius": 2 * mm});
            skCircle(sketch, "E4.15.2.0", {"center": v(-69.9, -259.9) * mm, "radius": 2 * mm});
            skCircle(sketch, "E4.15.3.0", {"center": v(-69.9, -243.9) * mm, "radius": 2 * mm});
            skCircle(sketch, "E4.15.4.0", {"center": v(-69.9, -227.9) * mm, "radius": 2 * mm});
            skCircle(sketch, "E4.15.5.0", {"center": v(-69.9, -211.9) * mm, "radius": 2 * mm});
            skCircle(sketch, "E4.16.0.0", {"center": v(-53.9, -291.9) * mm, "radius": 2 * mm});
            skCircle(sketch, "E4.16.1.0", {"center": v(-53.9, -275.9) * mm, "radius": 2 * mm});
            skCircle(sketch, "E4.16.2.0", {"center": v(-53.9, -259.9) * mm, "radius": 2 * mm});
            skCircle(sketch, "E4.16.3.0", {"center": v(-53.9, -243.9) * mm, "radius": 2 * mm});
            skCircle(sketch, "E4.16.4.0", {"center": v(-53.9, -227.9) * mm, "radius": 2 * mm});
            skCircle(sketch, "E4.16.5.0", {"center": v(-53.9, -211.9) * mm, "radius": 2 * mm});
            skCircle(sketch, "E4.17.0.0", {"center": v(-37.9, -291.9) * mm, "radius": 2 * mm});
            skCircle(sketch, "E4.17.1.0", {"center": v(-37.9, -275.9) * mm, "radius": 2 * mm});
            skCircle(sketch, "E4.17.2.0", {"center": v(-37.9, -259.9) * mm, "radius": 2 * mm});
            skCircle(sketch, "E4.17.3.0", {"center": v(-37.9, -243.9) * mm, "radius": 2 * mm});
            skCircle(sketch, "E4.17.4.0", {"center": v(-37.9, -227.9) * mm, "radius": 2 * mm});
            skCircle(sketch, "E4.17.5.0", {"center": v(-37.9, -211.9) * mm, "radius": 2 * mm});
            skCircle(sketch, "E4.18.0.0", {"center": v(-21.9, -291.9) * mm, "radius": 2 * mm});
            skCircle(sketch, "E4.18.1.0", {"center": v(-21.9, -275.9) * mm, "radius": 2 * mm});
            skCircle(sketch, "E4.18.2.0", {"center": v(-21.9, -259.9) * mm, "radius": 2 * mm});
            skCircle(sketch, "E4.18.3.0", {"center": v(-21.9, -243.9) * mm, "radius": 2 * mm});
            skCircle(sketch, "E4.18.4.0", {"center": v(-21.9, -227.9) * mm, "radius": 2 * mm});
            skCircle(sketch, "E4.18.5.0", {"center": v(-21.9, -211.9) * mm, "radius": 2 * mm});
            skCircle(sketch, "E4.19.0.0", {"center": v(-5.9, -291.9) * mm, "radius": 2 * mm});
            skCircle(sketch, "E4.19.1.0", {"center": v(-5.9, -275.9) * mm, "radius": 2 * mm});
            skCircle(sketch, "E4.19.2.0", {"center": v(-5.9, -259.9) * mm, "radius": 2 * mm});
            skCircle(sketch, "E4.19.3.0", {"center": v(-5.9, -243.9) * mm, "radius": 2 * mm});
            skCircle(sketch, "E4.19.4.0", {"center": v(-5.9, -227.9) * mm, "radius": 2 * mm});
            skCircle(sketch, "E4.19.5.0", {"center": v(-5.9, -211.9) * mm, "radius": 2 * mm});
            skCircle(sketch, "E4.20.0.0", {"center": v(10.1, -291.9) * mm, "radius": 2 * mm});
            skCircle(sketch, "E4.20.1.0", {"center": v(10.1, -275.9) * mm, "radius": 2 * mm});
            skCircle(sketch, "E4.20.2.0", {"center": v(10.1, -259.9) * mm, "radius": 2 * mm});
            skCircle(sketch, "E4.20.3.0", {"center": v(10.1, -243.9) * mm, "radius": 2 * mm});
            skCircle(sketch, "E4.20.4.0", {"center": v(10.1, -227.9) * mm, "radius": 2 * mm});
            skCircle(sketch, "E4.20.5.0", {"center": v(10.1, -211.9) * mm, "radius": 2 * mm});
            skCircle(sketch, "E4.21.0.0", {"center": v(26.1, -291.9) * mm, "radius": 2 * mm});
            skCircle(sketch, "E4.21.1.0", {"center": v(26.1, -275.9) * mm, "radius": 2 * mm});
            skCircle(sketch, "E4.21.2.0", {"center": v(26.1, -259.9) * mm, "radius": 2 * mm});
            skCircle(sketch, "E4.21.3.0", {"center": v(26.1, -243.9) * mm, "radius": 2 * mm});
            skCircle(sketch, "E4.21.4.0", {"center": v(26.1, -227.9) * mm, "radius": 2 * mm});
            skCircle(sketch, "E4.21.5.0", {"center": v(26.1, -211.9) * mm, "radius": 2 * mm});
            skCircle(sketch, "E4.22.0.0", {"center": v(42.1, -291.9) * mm, "radius": 2 * mm});
            skCircle(sketch, "E4.22.1.0", {"center": v(42.1, -275.9) * mm, "radius": 2 * mm});
            skCircle(sketch, "E4.22.2.0", {"center": v(42.1, -259.9) * mm, "radius": 2 * mm});
            skCircle(sketch, "E4.22.3.0", {"center": v(42.1, -243.9) * mm, "radius": 2 * mm});
            skCircle(sketch, "E4.22.4.0", {"center": v(42.1, -227.9) * mm, "radius": 2 * mm});
            skCircle(sketch, "E4.22.5.0", {"center": v(42.1, -211.9) * mm, "radius": 2 * mm});
            skCircle(sketch, "E4.23.0.0", {"center": v(58.1, -291.9) * mm, "radius": 2 * mm});
            skCircle(sketch, "E4.23.1.0", {"center": v(58.1, -275.9) * mm, "radius": 2 * mm});
            skCircle(sketch, "E4.23.2.0", {"center": v(58.1, -259.9) * mm, "radius": 2 * mm});
            skCircle(sketch, "E4.23.3.0", {"center": v(58.1, -243.9) * mm, "radius": 2 * mm});
            skCircle(sketch, "E4.23.4.0", {"center": v(58.1, -227.9) * mm, "radius": 2 * mm});
            skCircle(sketch, "E4.23.5.0", {"center": v(58.1, -211.9) * mm, "radius": 2 * mm});
            skCircle(sketch, "E4.24.0.0", {"center": v(74.1, -291.9) * mm, "radius": 2 * mm});
            skCircle(sketch, "E4.24.1.0", {"center": v(74.1, -275.9) * mm, "radius": 2 * mm});
            skCircle(sketch, "E4.24.2.0", {"center": v(74.1, -259.9) * mm, "radius": 2 * mm});
            skCircle(sketch, "E4.24.3.0", {"center": v(74.1, -243.9) * mm, "radius": 2 * mm});
            skCircle(sketch, "E4.24.4.0", {"center": v(74.1, -227.9) * mm, "radius": 2 * mm});
            skCircle(sketch, "E4.24.5.0", {"center": v(74.1, -211.9) * mm, "radius": 2 * mm});
            skCircle(sketch, "E4.25.0.0", {"center": v(90.1, -291.9) * mm, "radius": 2 * mm});
            skCircle(sketch, "E4.25.1.0", {"center": v(90.1, -275.9) * mm, "radius": 2 * mm});
            skCircle(sketch, "E4.25.2.0", {"center": v(90.1, -259.9) * mm, "radius": 2 * mm});
            skCircle(sketch, "E4.25.3.0", {"center": v(90.1, -243.9) * mm, "radius": 2 * mm});
            skCircle(sketch, "E4.25.4.0", {"center": v(90.1, -227.9) * mm, "radius": 2 * mm});
            skCircle(sketch, "E4.25.5.0", {"center": v(90.1, -211.9) * mm, "radius": 2 * mm});
            skCircle(sketch, "E4.26.0.0", {"center": v(106.1, -291.9) * mm, "radius": 2 * mm});
            skCircle(sketch, "E4.26.1.0", {"center": v(106.1, -275.9) * mm, "radius": 2 * mm});
            skCircle(sketch, "E4.26.2.0", {"center": v(106.1, -259.9) * mm, "radius": 2 * mm});
            skCircle(sketch, "E4.26.3.0", {"center": v(106.1, -243.9) * mm, "radius": 2 * mm});
            skCircle(sketch, "E4.26.4.0", {"center": v(106.1, -227.9) * mm, "radius": 2 * mm});
            skCircle(sketch, "E4.26.5.0", {"center": v(106.1, -211.9) * mm, "radius": 2 * mm});
            skCircle(sketch, "E4.27.0.0", {"center": v(122.1, -291.9) * mm, "radius": 2 * mm});
            skCircle(sketch, "E4.27.1.0", {"center": v(122.1, -275.9) * mm, "radius": 2 * mm});
            skCircle(sketch, "E4.27.2.0", {"center": v(122.1, -259.9) * mm, "radius": 2 * mm});
            skCircle(sketch, "E4.27.3.0", {"center": v(122.1, -243.9) * mm, "radius": 2 * mm});
            skCircle(sketch, "E4.27.4.0", {"center": v(122.1, -227.9) * mm, "radius": 2 * mm});
            skCircle(sketch, "E4.27.5.0", {"center": v(122.1, -211.9) * mm, "radius": 2 * mm});
            skCircle(sketch, "E4.28.0.0", {"center": v(138.1, -291.9) * mm, "radius": 2 * mm});
            skCircle(sketch, "E4.28.1.0", {"center": v(138.1, -275.9) * mm, "radius": 2 * mm});
            skCircle(sketch, "E4.28.2.0", {"center": v(138.1, -259.9) * mm, "radius": 2 * mm});
            skCircle(sketch, "E4.28.3.0", {"center": v(138.1, -243.9) * mm, "radius": 2 * mm});
            skCircle(sketch, "E4.28.4.0", {"center": v(138.1, -227.9) * mm, "radius": 2 * mm});
            skCircle(sketch, "E4.28.5.0", {"center": v(138.1, -211.9) * mm, "radius": 2 * mm});
            skCircle(sketch, "E4.29.0.0", {"center": v(154.1, -291.9) * mm, "radius": 2 * mm});
            skCircle(sketch, "E4.29.1.0", {"center": v(154.1, -275.9) * mm, "radius": 2 * mm});
            skCircle(sketch, "E4.29.2.0", {"center": v(154.1, -259.9) * mm, "radius": 2 * mm});
            skCircle(sketch, "E4.29.3.0", {"center": v(154.1, -243.9) * mm, "radius": 2 * mm});
            skCircle(sketch, "E4.29.4.0", {"center": v(154.1, -227.9) * mm, "radius": 2 * mm});
            skCircle(sketch, "E4.29.5.0", {"center": v(154.1, -211.9) * mm, "radius": 2 * mm});
            skCircle(sketch, "E4.30.0.0", {"center": v(170.1, -291.9) * mm, "radius": 2 * mm});
            skCircle(sketch, "E4.30.1.0", {"center": v(170.1, -275.9) * mm, "radius": 2 * mm});
            skCircle(sketch, "E4.30.2.0", {"center": v(170.1, -259.9) * mm, "radius": 2 * mm});
            skCircle(sketch, "E4.30.3.0", {"center": v(170.1, -243.9) * mm, "radius": 2 * mm});
            skCircle(sketch, "E4.30.4.0", {"center": v(170.1, -227.9) * mm, "radius": 2 * mm});
            skCircle(sketch, "E4.30.5.0", {"center": v(170.1, -211.9) * mm, "radius": 2 * mm});
            skCircle(sketch, "E4.31.0.0", {"center": v(186.1, -291.9) * mm, "radius": 2 * mm});
            skCircle(sketch, "E4.31.1.0", {"center": v(186.1, -275.9) * mm, "radius": 2 * mm});
            skCircle(sketch, "E4.31.2.0", {"center": v(186.1, -259.9) * mm, "radius": 2 * mm});
            skCircle(sketch, "E4.31.3.0", {"center": v(186.1, -243.9) * mm, "radius": 2 * mm});
            skCircle(sketch, "E4.31.4.0", {"center": v(186.1, -227.9) * mm, "radius": 2 * mm});
            skCircle(sketch, "E4.31.5.0", {"center": v(186.1, -211.9) * mm, "radius": 2 * mm});
            skCircle(sketch, "E4.32.0.0", {"center": v(202.1, -291.9) * mm, "radius": 2 * mm});
            skCircle(sketch, "E4.32.1.0", {"center": v(202.1, -275.9) * mm, "radius": 2 * mm});
            skCircle(sketch, "E4.32.2.0", {"center": v(202.1, -259.9) * mm, "radius": 2 * mm});
            skCircle(sketch, "E4.32.3.0", {"center": v(202.1, -243.9) * mm, "radius": 2 * mm});
            skCircle(sketch, "E4.32.4.0", {"center": v(202.1, -227.9) * mm, "radius": 2 * mm});
            skCircle(sketch, "E4.32.5.0", {"center": v(202.1, -211.9) * mm, "radius": 2 * mm});
            skCircle(sketch, "E4.33.0.0", {"center": v(218.1, -291.9) * mm, "radius": 2 * mm});
            skCircle(sketch, "E4.33.1.0", {"center": v(218.1, -275.9) * mm, "radius": 2 * mm});
            skCircle(sketch, "E4.33.2.0", {"center": v(218.1, -259.9) * mm, "radius": 2 * mm});
            skCircle(sketch, "E4.33.3.0", {"center": v(218.1, -243.9) * mm, "radius": 2 * mm});
            skCircle(sketch, "E4.33.4.0", {"center": v(218.1, -227.9) * mm, "radius": 2 * mm});
            skCircle(sketch, "E4.33.5.0", {"center": v(218.1, -211.9) * mm, "radius": 2 * mm});
            skCircle(sketch, "E4.34.0.0", {"center": v(234.1, -291.9) * mm, "radius": 2 * mm});
            skCircle(sketch, "E4.34.1.0", {"center": v(234.1, -275.9) * mm, "radius": 2 * mm});
            skCircle(sketch, "E4.34.2.0", {"center": v(234.1, -259.9) * mm, "radius": 2 * mm});
            skCircle(sketch, "E4.34.3.0", {"center": v(234.1, -243.9) * mm, "radius": 2 * mm});
            skCircle(sketch, "E4.34.4.0", {"center": v(234.1, -227.9) * mm, "radius": 2 * mm});
            skCircle(sketch, "E4.34.5.0", {"center": v(234.1, -211.9) * mm, "radius": 2 * mm});
            skCircle(sketch, "E4.35.0.0", {"center": v(250.1, -291.9) * mm, "radius": 2 * mm});
            skCircle(sketch, "E4.35.1.0", {"center": v(250.1, -275.9) * mm, "radius": 2 * mm});
            skCircle(sketch, "E4.35.2.0", {"center": v(250.1, -259.9) * mm, "radius": 2 * mm});
            skCircle(sketch, "E4.35.3.0", {"center": v(250.1, -243.9) * mm, "radius": 2 * mm});
            skCircle(sketch, "E4.35.4.0", {"center": v(250.1, -227.9) * mm, "radius": 2 * mm});
            skCircle(sketch, "E4.35.5.0", {"center": v(250.1, -211.9) * mm, "radius": 2 * mm});
            skCircle(sketch, "E4.36.0.0", {"center": v(266.1, -291.9) * mm, "radius": 2 * mm});
            skCircle(sketch, "E4.36.1.0", {"center": v(266.1, -275.9) * mm, "radius": 2 * mm});
            skCircle(sketch, "E4.36.2.0", {"center": v(266.1, -259.9) * mm, "radius": 2 * mm});
            skCircle(sketch, "E4.36.3.0", {"center": v(266.1, -243.9) * mm, "radius": 2 * mm});
            skCircle(sketch, "E4.36.4.0", {"center": v(266.1, -227.9) * mm, "radius": 2 * mm});
            skCircle(sketch, "E4.36.5.0", {"center": v(266.1, -211.9) * mm, "radius": 2 * mm});
            skCircle(sketch, "E4.37.0.0", {"center": v(282.1, -291.9) * mm, "radius": 2 * mm});
            skCircle(sketch, "E4.37.1.0", {"center": v(282.1, -275.9) * mm, "radius": 2 * mm});
            skCircle(sketch, "E4.37.2.0", {"center": v(282.1, -259.9) * mm, "radius": 2 * mm});
            skCircle(sketch, "E4.37.3.0", {"center": v(282.1, -243.9) * mm, "radius": 2 * mm});
            skCircle(sketch, "E4.37.4.0", {"center": v(282.1, -227.9) * mm, "radius": 2 * mm});
            skCircle(sketch, "E4.37.5.0", {"center": v(282.1, -211.9) * mm, "radius": 2 * mm});
            skCircle(sketch, "E4.38.0.0", {"center": v(298.1, -291.9) * mm, "radius": 2 * mm});
            skCircle(sketch, "E4.38.1.0", {"center": v(298.1, -275.9) * mm, "radius": 2 * mm});
            skCircle(sketch, "E4.38.2.0", {"center": v(298.1, -259.9) * mm, "radius": 2 * mm});
            skCircle(sketch, "E4.38.3.0", {"center": v(298.1, -243.9) * mm, "radius": 2 * mm});
            skCircle(sketch, "E4.38.4.0", {"center": v(298.1, -227.9) * mm, "radius": 2 * mm});
            skCircle(sketch, "E4.38.5.0", {"center": v(298.1, -211.9) * mm, "radius": 2 * mm});
            skCircle(sketch, "E4.39.0.0", {"center": v(314.1, -291.9) * mm, "radius": 2 * mm});
            skCircle(sketch, "E4.39.1.0", {"center": v(314.1, -275.9) * mm, "radius": 2 * mm});
            skCircle(sketch, "E4.39.2.0", {"center": v(314.1, -259.9) * mm, "radius": 2 * mm});
            skCircle(sketch, "E4.39.3.0", {"center": v(314.1, -243.9) * mm, "radius": 2 * mm});
            skCircle(sketch, "E4.39.4.0", {"center": v(314.1, -227.9) * mm, "radius": 2 * mm});
            skCircle(sketch, "E4.39.5.0", {"center": v(314.1, -211.9) * mm, "radius": 2 * mm});
            skLineSegment(sketch, "E4.direction1", {"start": v(-309.9, -291.9) * mm, "end": v(-293.9, -291.9) * mm, "construction": true});
            skLineSegment(sketch, "E4.direction2", {"start": v(-309.9, -291.9) * mm, "end": v(-309.9, -275.9) * mm, "construction": true});
            skCircle(sketch, "E5.0.0.6", {"center": v(-309.9, -195.9) * mm, "radius": 2 * mm});
            skCircle(sketch, "E5.0.0.7", {"center": v(-309.9, -179.9) * mm, "radius": 2 * mm});
            skCircle(sketch, "E5.0.0.8", {"center": v(-309.9, -163.9) * mm, "radius": 2 * mm});
            skCircle(sketch, "E5.0.0.9", {"center": v(-309.9, -147.9) * mm, "radius": 2 * mm});
            skCircle(sketch, "E5.0.1.6", {"center": v(-293.9, -195.9) * mm, "radius": 2 * mm});
            skCircle(sketch, "E5.0.1.7", {"center": v(-293.9, -179.9) * mm, "radius": 2 * mm});
            skCircle(sketch, "E5.0.1.8", {"center": v(-293.9, -163.9) * mm, "radius": 2 * mm});
            skCircle(sketch, "E5.0.1.9", {"center": v(-293.9, -147.9) * mm, "radius": 2 * mm});
            skCircle(sketch, "E5.0.2.6", {"center": v(-277.9, -195.9) * mm, "radius": 2 * mm});
            skCircle(sketch, "E5.0.2.7", {"center": v(-277.9, -179.9) * mm, "radius": 2 * mm});
            skCircle(sketch, "E5.0.2.8", {"center": v(-277.9, -163.9) * mm, "radius": 2 * mm});
            skCircle(sketch, "E5.0.2.9", {"center": v(-277.9, -147.9) * mm, "radius": 2 * mm});
            skCircle(sketch, "E5.0.3.6", {"center": v(-261.9, -195.9) * mm, "radius": 2 * mm});
            skCircle(sketch, "E5.0.3.7", {"center": v(-261.9, -179.9) * mm, "radius": 2 * mm});
            skCircle(sketch, "E5.0.3.8", {"center": v(-261.9, -163.9) * mm, "radius": 2 * mm});
            skCircle(sketch, "E5.0.3.9", {"center": v(-261.9, -147.9) * mm, "radius": 2 * mm});
            skCircle(sketch, "E5.0.4.6", {"center": v(-245.9, -195.9) * mm, "radius": 2 * mm});
            skCircle(sketch, "E5.0.4.7", {"center": v(-245.9, -179.9) * mm, "radius": 2 * mm});
            skCircle(sketch, "E5.0.4.8", {"center": v(-245.9, -163.9) * mm, "radius": 2 * mm});
            skCircle(sketch, "E5.0.4.9", {"center": v(-245.9, -147.9) * mm, "radius": 2 * mm});
            skCircle(sketch, "E5.0.5.6", {"center": v(-229.9, -195.9) * mm, "radius": 2 * mm});
            skCircle(sketch, "E5.0.5.7", {"center": v(-229.9, -179.9) * mm, "radius": 2 * mm});
            skCircle(sketch, "E5.0.5.8", {"center": v(-229.9, -163.9) * mm, "radius": 2 * mm});
            skCircle(sketch, "E5.0.5.9", {"center": v(-229.9, -147.9) * mm, "radius": 2 * mm});
            skCircle(sketch, "E5.0.6.6", {"center": v(-213.9, -195.9) * mm, "radius": 2 * mm});
            skCircle(sketch, "E5.0.6.7", {"center": v(-213.9, -179.9) * mm, "radius": 2 * mm});
            skCircle(sketch, "E5.0.6.8", {"center": v(-213.9, -163.9) * mm, "radius": 2 * mm});
            skCircle(sketch, "E5.0.6.9", {"center": v(-213.9, -147.9) * mm, "radius": 2 * mm});
            skCircle(sketch, "E5.0.7.6", {"center": v(-197.9, -195.9) * mm, "radius": 2 * mm});
            skCircle(sketch, "E5.0.7.7", {"center": v(-197.9, -179.9) * mm, "radius": 2 * mm});
            skCircle(sketch, "E5.0.7.8", {"center": v(-197.9, -163.9) * mm, "radius": 2 * mm});
            skCircle(sketch, "E5.0.7.9", {"center": v(-197.9, -147.9) * mm, "radius": 2 * mm});
            skCircle(sketch, "E5.0.8.6", {"center": v(-181.9, -195.9) * mm, "radius": 2 * mm});
            skCircle(sketch, "E5.0.8.7", {"center": v(-181.9, -179.9) * mm, "radius": 2 * mm});
            skCircle(sketch, "E5.0.8.8", {"center": v(-181.9, -163.9) * mm, "radius": 2 * mm});
            skCircle(sketch, "E5.0.8.9", {"center": v(-181.9, -147.9) * mm, "radius": 2 * mm});
            skCircle(sketch, "E5.0.9.6", {"center": v(-165.9, -195.9) * mm, "radius": 2 * mm});
            skCircle(sketch, "E5.0.9.7", {"center": v(-165.9, -179.9) * mm, "radius": 2 * mm});
            skCircle(sketch, "E5.0.9.8", {"center": v(-165.9, -163.9) * mm, "radius": 2 * mm});
            skCircle(sketch, "E5.0.9.9", {"center": v(-165.9, -147.9) * mm, "radius": 2 * mm});
            skCircle(sketch, "E5.0.10.6", {"center": v(-149.9, -195.9) * mm, "radius": 2 * mm});
            skCircle(sketch, "E5.0.10.7", {"center": v(-149.9, -179.9) * mm, "radius": 2 * mm});
            skCircle(sketch, "E5.0.10.8", {"center": v(-149.9, -163.9) * mm, "radius": 2 * mm});
            skCircle(sketch, "E5.0.10.9", {"center": v(-149.9, -147.9) * mm, "radius": 2 * mm});
            skCircle(sketch, "E5.0.11.6", {"center": v(-133.9, -195.9) * mm, "radius": 2 * mm});
            skCircle(sketch, "E5.0.11.7", {"center": v(-133.9, -179.9) * mm, "radius": 2 * mm});
            skCircle(sketch, "E5.0.11.8", {"center": v(-133.9, -163.9) * mm, "radius": 2 * mm});
            skCircle(sketch, "E5.0.11.9", {"center": v(-133.9, -147.9) * mm, "radius": 2 * mm});
            skCircle(sketch, "E5.0.12.6", {"center": v(-117.9, -195.9) * mm, "radius": 2 * mm});
            skCircle(sketch, "E5.0.12.7", {"center": v(-117.9, -179.9) * mm, "radius": 2 * mm});
            skCircle(sketch, "E5.0.12.8", {"center": v(-117.9, -163.9) * mm, "radius": 2 * mm});
            skCircle(sketch, "E5.0.12.9", {"center": v(-117.9, -147.9) * mm, "radius": 2 * mm});
            skCircle(sketch, "E5.0.13.6", {"center": v(-101.9, -195.9) * mm, "radius": 2 * mm});
            skCircle(sketch, "E5.0.13.7", {"center": v(-101.9, -179.9) * mm, "radius": 2 * mm});
            skCircle(sketch, "E5.0.13.8", {"center": v(-101.9, -163.9) * mm, "radius": 2 * mm});
            skCircle(sketch, "E5.0.13.9", {"center": v(-101.9, -147.9) * mm, "radius": 2 * mm});
            skCircle(sketch, "E5.0.14.6", {"center": v(-85.9, -195.9) * mm, "radius": 2 * mm});
            skCircle(sketch, "E5.0.14.7", {"center": v(-85.9, -179.9) * mm, "radius": 2 * mm});
            skCircle(sketch, "E5.0.14.8", {"center": v(-85.9, -163.9) * mm, "radius": 2 * mm});
            skCircle(sketch, "E5.0.14.9", {"center": v(-85.9, -147.9) * mm, "radius": 2 * mm});
            skCircle(sketch, "E5.0.15.6", {"center": v(-69.9, -195.9) * mm, "radius": 2 * mm});
            skCircle(sketch, "E5.0.15.7", {"center": v(-69.9, -179.9) * mm, "radius": 2 * mm});
            skCircle(sketch, "E5.0.15.8", {"center": v(-69.9, -163.9) * mm, "radius": 2 * mm});
            skCircle(sketch, "E5.0.15.9", {"center": v(-69.9, -147.9) * mm, "radius": 2 * mm});
            skCircle(sketch, "E5.0.16.6", {"center": v(-53.9, -195.9) * mm, "radius": 2 * mm});
            skCircle(sketch, "E5.0.16.7", {"center": v(-53.9, -179.9) * mm, "radius": 2 * mm});
            skCircle(sketch, "E5.0.16.8", {"center": v(-53.9, -163.9) * mm, "radius": 2 * mm});
            skCircle(sketch, "E5.0.16.9", {"center": v(-53.9, -147.9) * mm, "radius": 2 * mm});
            skCircle(sketch, "E5.0.17.6", {"center": v(-37.9, -195.9) * mm, "radius": 2 * mm});
            skCircle(sketch, "E5.0.17.7", {"center": v(-37.9, -179.9) * mm, "radius": 2 * mm});
            skCircle(sketch, "E5.0.17.8", {"center": v(-37.9, -163.9) * mm, "radius": 2 * mm});
            skCircle(sketch, "E5.0.17.9", {"center": v(-37.9, -147.9) * mm, "radius": 2 * mm});
            skCircle(sketch, "E5.0.18.6", {"center": v(-21.9, -195.9) * mm, "radius": 2 * mm});
            skCircle(sketch, "E5.0.18.7", {"center": v(-21.9, -179.9) * mm, "radius": 2 * mm});
            skCircle(sketch, "E5.0.18.8", {"center": v(-21.9, -163.9) * mm, "radius": 2 * mm});
            skCircle(sketch, "E5.0.18.9", {"center": v(-21.9, -147.9) * mm, "radius": 2 * mm});
            skCircle(sketch, "E5.0.19.6", {"center": v(-5.9, -195.9) * mm, "radius": 2 * mm});
            skCircle(sketch, "E5.0.19.7", {"center": v(-5.9, -179.9) * mm, "radius": 2 * mm});
            skCircle(sketch, "E5.0.19.8", {"center": v(-5.9, -163.9) * mm, "radius": 2 * mm});
            skCircle(sketch, "E5.0.19.9", {"center": v(-5.9, -147.9) * mm, "radius": 2 * mm});
            skCircle(sketch, "E5.0.20.6", {"center": v(10.1, -195.9) * mm, "radius": 2 * mm});
            skCircle(sketch, "E5.0.20.7", {"center": v(10.1, -179.9) * mm, "radius": 2 * mm});
            skCircle(sketch, "E5.0.20.8", {"center": v(10.1, -163.9) * mm, "radius": 2 * mm});
            skCircle(sketch, "E5.0.20.9", {"center": v(10.1, -147.9) * mm, "radius": 2 * mm});
            skCircle(sketch, "E5.0.21.6", {"center": v(26.1, -195.9) * mm, "radius": 2 * mm});
            skCircle(sketch, "E5.0.21.7", {"center": v(26.1, -179.9) * mm, "radius": 2 * mm});
            skCircle(sketch, "E5.0.21.8", {"center": v(26.1, -163.9) * mm, "radius": 2 * mm});
            skCircle(sketch, "E5.0.21.9", {"center": v(26.1, -147.9) * mm, "radius": 2 * mm});
            skCircle(sketch, "E5.0.22.6", {"center": v(42.1, -195.9) * mm, "radius": 2 * mm});
            skCircle(sketch, "E5.0.22.7", {"center": v(42.1, -179.9) * mm, "radius": 2 * mm});
            skCircle(sketch, "E5.0.22.8", {"center": v(42.1, -163.9) * mm, "radius": 2 * mm});
            skCircle(sketch, "E5.0.22.9", {"center": v(42.1, -147.9) * mm, "radius": 2 * mm});
            skCircle(sketch, "E5.0.23.6", {"center": v(58.1, -195.9) * mm, "radius": 2 * mm});
            skCircle(sketch, "E5.0.23.7", {"center": v(58.1, -179.9) * mm, "radius": 2 * mm});
            skCircle(sketch, "E5.0.23.8", {"center": v(58.1, -163.9) * mm, "radius": 2 * mm});
            skCircle(sketch, "E5.0.23.9", {"center": v(58.1, -147.9) * mm, "radius": 2 * mm});
            skCircle(sketch, "E5.0.24.6", {"center": v(74.1, -195.9) * mm, "radius": 2 * mm});
            skCircle(sketch, "E5.0.24.7", {"center": v(74.1, -179.9) * mm, "radius": 2 * mm});
            skCircle(sketch, "E5.0.24.8", {"center": v(74.1, -163.9) * mm, "radius": 2 * mm});
            skCircle(sketch, "E5.0.24.9", {"center": v(74.1, -147.9) * mm, "radius": 2 * mm});
            skCircle(sketch, "E5.0.25.6", {"center": v(90.1, -195.9) * mm, "radius": 2 * mm});
            skCircle(sketch, "E5.0.25.7", {"center": v(90.1, -179.9) * mm, "radius": 2 * mm});
            skCircle(sketch, "E5.0.25.8", {"center": v(90.1, -163.9) * mm, "radius": 2 * mm});
            skCircle(sketch, "E5.0.25.9", {"center": v(90.1, -147.9) * mm, "radius": 2 * mm});
            skCircle(sketch, "E5.0.26.6", {"center": v(106.1, -195.9) * mm, "radius": 2 * mm});
            skCircle(sketch, "E5.0.26.7", {"center": v(106.1, -179.9) * mm, "radius": 2 * mm});
            skCircle(sketch, "E5.0.26.8", {"center": v(106.1, -163.9) * mm, "radius": 2 * mm});
            skCircle(sketch, "E5.0.26.9", {"center": v(106.1, -147.9) * mm, "radius": 2 * mm});
            skCircle(sketch, "E5.0.27.6", {"center": v(122.1, -195.9) * mm, "radius": 2 * mm});
            skCircle(sketch, "E5.0.27.7", {"center": v(122.1, -179.9) * mm, "radius": 2 * mm});
            skCircle(sketch, "E5.0.27.8", {"center": v(122.1, -163.9) * mm, "radius": 2 * mm});
            skCircle(sketch, "E5.0.27.9", {"center": v(122.1, -147.9) * mm, "radius": 2 * mm});
            skCircle(sketch, "E5.0.28.6", {"center": v(138.1, -195.9) * mm, "radius": 2 * mm});
            skCircle(sketch, "E5.0.28.7", {"center": v(138.1, -179.9) * mm, "radius": 2 * mm});
            skCircle(sketch, "E5.0.28.8", {"center": v(138.1, -163.9) * mm, "radius": 2 * mm});
            skCircle(sketch, "E5.0.28.9", {"center": v(138.1, -147.9) * mm, "radius": 2 * mm});
            skCircle(sketch, "E5.0.29.6", {"center": v(154.1, -195.9) * mm, "radius": 2 * mm});
            skCircle(sketch, "E5.0.29.7", {"center": v(154.1, -179.9) * mm, "radius": 2 * mm});
            skCircle(sketch, "E5.0.29.8", {"center": v(154.1, -163.9) * mm, "radius": 2 * mm});
            skCircle(sketch, "E5.0.29.9", {"center": v(154.1, -147.9) * mm, "radius": 2 * mm});
            skCircle(sketch, "E5.0.30.6", {"center": v(170.1, -195.9) * mm, "radius": 2 * mm});
            skCircle(sketch, "E5.0.30.7", {"center": v(170.1, -179.9) * mm, "radius": 2 * mm});
            skCircle(sketch, "E5.0.30.8", {"center": v(170.1, -163.9) * mm, "radius": 2 * mm});
            skCircle(sketch, "E5.0.30.9", {"center": v(170.1, -147.9) * mm, "radius": 2 * mm});
            skCircle(sketch, "E5.0.31.6", {"center": v(186.1, -195.9) * mm, "radius": 2 * mm});
            skCircle(sketch, "E5.0.31.7", {"center": v(186.1, -179.9) * mm, "radius": 2 * mm});
            skCircle(sketch, "E5.0.31.8", {"center": v(186.1, -163.9) * mm, "radius": 2 * mm});
            skCircle(sketch, "E5.0.31.9", {"center": v(186.1, -147.9) * mm, "radius": 2 * mm});
            skCircle(sketch, "E5.0.32.6", {"center": v(202.1, -195.9) * mm, "radius": 2 * mm});
            skCircle(sketch, "E5.0.32.7", {"center": v(202.1, -179.9) * mm, "radius": 2 * mm});
            skCircle(sketch, "E5.0.32.8", {"center": v(202.1, -163.9) * mm, "radius": 2 * mm});
            skCircle(sketch, "E5.0.32.9", {"center": v(202.1, -147.9) * mm, "radius": 2 * mm});
            skCircle(sketch, "E5.0.33.6", {"center": v(218.1, -195.9) * mm, "radius": 2 * mm});
            skCircle(sketch, "E5.0.33.7", {"center": v(218.1, -179.9) * mm, "radius": 2 * mm});
            skCircle(sketch, "E5.0.33.8", {"center": v(218.1, -163.9) * mm, "radius": 2 * mm});
            skCircle(sketch, "E5.0.33.9", {"center": v(218.1, -147.9) * mm, "radius": 2 * mm});
            skCircle(sketch, "E5.0.34.6", {"center": v(234.1, -195.9) * mm, "radius": 2 * mm});
            skCircle(sketch, "E5.0.34.7", {"center": v(234.1, -179.9) * mm, "radius": 2 * mm});
            skCircle(sketch, "E5.0.34.8", {"center": v(234.1, -163.9) * mm, "radius": 2 * mm});
            skCircle(sketch, "E5.0.34.9", {"center": v(234.1, -147.9) * mm, "radius": 2 * mm});
            skCircle(sketch, "E5.0.35.6", {"center": v(250.1, -195.9) * mm, "radius": 2 * mm});
            skCircle(sketch, "E5.0.35.7", {"center": v(250.1, -179.9) * mm, "radius": 2 * mm});
            skCircle(sketch, "E5.0.35.8", {"center": v(250.1, -163.9) * mm, "radius": 2 * mm});
            skCircle(sketch, "E5.0.35.9", {"center": v(250.1, -147.9) * mm, "radius": 2 * mm});
            skCircle(sketch, "E5.0.36.6", {"center": v(266.1, -195.9) * mm, "radius": 2 * mm});
            skCircle(sketch, "E5.0.36.7", {"center": v(266.1, -179.9) * mm, "radius": 2 * mm});
            skCircle(sketch, "E5.0.36.8", {"center": v(266.1, -163.9) * mm, "radius": 2 * mm});
            skCircle(sketch, "E5.0.36.9", {"center": v(266.1, -147.9) * mm, "radius": 2 * mm});
            skCircle(sketch, "E5.0.37.6", {"center": v(282.1, -195.9) * mm, "radius": 2 * mm});
            skCircle(sketch, "E5.0.37.7", {"center": v(282.1, -179.9) * mm, "radius": 2 * mm});
            skCircle(sketch, "E5.0.37.8", {"center": v(282.1, -163.9) * mm, "radius": 2 * mm});
            skCircle(sketch, "E5.0.37.9", {"center": v(282.1, -147.9) * mm, "radius": 2 * mm});
            skCircle(sketch, "E5.0.38.6", {"center": v(298.1, -195.9) * mm, "radius": 2 * mm});
            skCircle(sketch, "E5.0.38.7", {"center": v(298.1, -179.9) * mm, "radius": 2 * mm});
            skCircle(sketch, "E5.0.38.8", {"center": v(298.1, -163.9) * mm, "radius": 2 * mm});
            skCircle(sketch, "E5.0.38.9", {"center": v(298.1, -147.9) * mm, "radius": 2 * mm});
            skCircle(sketch, "E5.0.39.6", {"center": v(314.1, -195.9) * mm, "radius": 2 * mm});
            skCircle(sketch, "E5.0.39.7", {"center": v(314.1, -179.9) * mm, "radius": 2 * mm});
            skCircle(sketch, "E5.0.39.8", {"center": v(314.1, -163.9) * mm, "radius": 2 * mm});
            skCircle(sketch, "E5.0.39.9", {"center": v(314.1, -147.9) * mm, "radius": 2 * mm});
            skCircle(sketch, "E6.0.0.8", {"center": v(-317.9, -171.9) * mm, "radius": 2 * mm});
            skCircle(sketch, "E6.0.0.9", {"center": v(-317.9, -155.9) * mm, "radius": 2 * mm});
            skCircle(sketch, "E6.0.1.8", {"center": v(-301.9, -171.9) * mm, "radius": 2 * mm});
            skCircle(sketch, "E6.0.1.9", {"center": v(-301.9, -155.9) * mm, "radius": 2 * mm});
            skCircle(sketch, "E6.0.2.8", {"center": v(-285.9, -171.9) * mm, "radius": 2 * mm});
            skCircle(sketch, "E6.0.2.9", {"center": v(-285.9, -155.9) * mm, "radius": 2 * mm});
            skCircle(sketch, "E6.0.3.8", {"center": v(-269.9, -171.9) * mm, "radius": 2 * mm});
            skCircle(sketch, "E6.0.3.9", {"center": v(-269.9, -155.9) * mm, "radius": 2 * mm});
            skCircle(sketch, "E6.0.4.8", {"center": v(-253.9, -171.9) * mm, "radius": 2 * mm});
            skCircle(sketch, "E6.0.4.9", {"center": v(-253.9, -155.9) * mm, "radius": 2 * mm});
            skCircle(sketch, "E6.0.5.8", {"center": v(-237.9, -171.9) * mm, "radius": 2 * mm});
            skCircle(sketch, "E6.0.5.9", {"center": v(-237.9, -155.9) * mm, "radius": 2 * mm});
            skCircle(sketch, "E6.0.6.8", {"center": v(-221.9, -171.9) * mm, "radius": 2 * mm});
            skCircle(sketch, "E6.0.6.9", {"center": v(-221.9, -155.9) * mm, "radius": 2 * mm});
            skCircle(sketch, "E6.0.7.8", {"center": v(-205.9, -171.9) * mm, "radius": 2 * mm});
            skCircle(sketch, "E6.0.7.9", {"center": v(-205.9, -155.9) * mm, "radius": 2 * mm});
            skCircle(sketch, "E6.0.8.8", {"center": v(-189.9, -171.9) * mm, "radius": 2 * mm});
            skCircle(sketch, "E6.0.8.9", {"center": v(-189.9, -155.9) * mm, "radius": 2 * mm});
            skCircle(sketch, "E6.0.9.8", {"center": v(-173.9, -171.9) * mm, "radius": 2 * mm});
            skCircle(sketch, "E6.0.9.9", {"center": v(-173.9, -155.9) * mm, "radius": 2 * mm});
            skCircle(sketch, "E6.0.10.8", {"center": v(-157.9, -171.9) * mm, "radius": 2 * mm});
            skCircle(sketch, "E6.0.10.9", {"center": v(-157.9, -155.9) * mm, "radius": 2 * mm});
            skCircle(sketch, "E6.0.11.8", {"center": v(-141.9, -171.9) * mm, "radius": 2 * mm});
            skCircle(sketch, "E6.0.11.9", {"center": v(-141.9, -155.9) * mm, "radius": 2 * mm});
            skCircle(sketch, "E6.0.12.8", {"center": v(-125.9, -171.9) * mm, "radius": 2 * mm});
            skCircle(sketch, "E6.0.12.9", {"center": v(-125.9, -155.9) * mm, "radius": 2 * mm});
            skCircle(sketch, "E6.0.13.8", {"center": v(-109.9, -171.9) * mm, "radius": 2 * mm});
            skCircle(sketch, "E6.0.13.9", {"center": v(-109.9, -155.9) * mm, "radius": 2 * mm});
            skCircle(sketch, "E6.0.14.8", {"center": v(-93.9, -171.9) * mm, "radius": 2 * mm});
            skCircle(sketch, "E6.0.14.9", {"center": v(-93.9, -155.9) * mm, "radius": 2 * mm});
            skCircle(sketch, "E6.0.15.8", {"center": v(-77.9, -171.9) * mm, "radius": 2 * mm});
            skCircle(sketch, "E6.0.15.9", {"center": v(-77.9, -155.9) * mm, "radius": 2 * mm});
            skCircle(sketch, "E6.0.16.8", {"center": v(-61.9, -171.9) * mm, "radius": 2 * mm});
            skCircle(sketch, "E6.0.16.9", {"center": v(-61.9, -155.9) * mm, "radius": 2 * mm});
            skCircle(sketch, "E6.0.17.8", {"center": v(-45.9, -171.9) * mm, "radius": 2 * mm});
            skCircle(sketch, "E6.0.17.9", {"center": v(-45.9, -155.9) * mm, "radius": 2 * mm});
            skCircle(sketch, "E6.0.18.8", {"center": v(-29.9, -171.9) * mm, "radius": 2 * mm});
            skCircle(sketch, "E6.0.18.9", {"center": v(-29.9, -155.9) * mm, "radius": 2 * mm});
            skCircle(sketch, "E6.0.19.8", {"center": v(-13.9, -171.9) * mm, "radius": 2 * mm});
            skCircle(sketch, "E6.0.19.9", {"center": v(-13.9, -155.9) * mm, "radius": 2 * mm});
            skCircle(sketch, "E6.0.20.8", {"center": v(2.1, -171.9) * mm, "radius": 2 * mm});
            skCircle(sketch, "E6.0.20.9", {"center": v(2.1, -155.9) * mm, "radius": 2 * mm});
            skCircle(sketch, "E6.0.21.8", {"center": v(18.1, -171.9) * mm, "radius": 2 * mm});
            skCircle(sketch, "E6.0.21.9", {"center": v(18.1, -155.9) * mm, "radius": 2 * mm});
            skCircle(sketch, "E6.0.22.8", {"center": v(34.1, -171.9) * mm, "radius": 2 * mm});
            skCircle(sketch, "E6.0.22.9", {"center": v(34.1, -155.9) * mm, "radius": 2 * mm});
            skCircle(sketch, "E6.0.23.8", {"center": v(50.1, -171.9) * mm, "radius": 2 * mm});
            skCircle(sketch, "E6.0.23.9", {"center": v(50.1, -155.9) * mm, "radius": 2 * mm});
            skCircle(sketch, "E6.0.24.8", {"center": v(66.1, -171.9) * mm, "radius": 2 * mm});
            skCircle(sketch, "E6.0.24.9", {"center": v(66.1, -155.9) * mm, "radius": 2 * mm});
            skCircle(sketch, "E6.0.25.8", {"center": v(82.1, -171.9) * mm, "radius": 2 * mm});
            skCircle(sketch, "E6.0.25.9", {"center": v(82.1, -155.9) * mm, "radius": 2 * mm});
            skCircle(sketch, "E6.0.26.8", {"center": v(98.1, -171.9) * mm, "radius": 2 * mm});
            skCircle(sketch, "E6.0.26.9", {"center": v(98.1, -155.9) * mm, "radius": 2 * mm});
            skCircle(sketch, "E6.0.27.8", {"center": v(114.1, -171.9) * mm, "radius": 2 * mm});
            skCircle(sketch, "E6.0.27.9", {"center": v(114.1, -155.9) * mm, "radius": 2 * mm});
            skCircle(sketch, "E6.0.28.8", {"center": v(130.1, -171.9) * mm, "radius": 2 * mm});
            skCircle(sketch, "E6.0.28.9", {"center": v(130.1, -155.9) * mm, "radius": 2 * mm});
            skCircle(sketch, "E6.0.29.8", {"center": v(146.1, -171.9) * mm, "radius": 2 * mm});
            skCircle(sketch, "E6.0.29.9", {"center": v(146.1, -155.9) * mm, "radius": 2 * mm});
            skCircle(sketch, "E6.0.30.8", {"center": v(162.1, -171.9) * mm, "radius": 2 * mm});
            skCircle(sketch, "E6.0.30.9", {"center": v(162.1, -155.9) * mm, "radius": 2 * mm});
            skCircle(sketch, "E6.0.31.8", {"center": v(178.1, -171.9) * mm, "radius": 2 * mm});
            skCircle(sketch, "E6.0.31.9", {"center": v(178.1, -155.9) * mm, "radius": 2 * mm});
            skCircle(sketch, "E6.0.32.8", {"center": v(194.1, -171.9) * mm, "radius": 2 * mm});
            skCircle(sketch, "E6.0.32.9", {"center": v(194.1, -155.9) * mm, "radius": 2 * mm});
            skCircle(sketch, "E6.0.33.8", {"center": v(210.1, -171.9) * mm, "radius": 2 * mm});
            skCircle(sketch, "E6.0.33.9", {"center": v(210.1, -155.9) * mm, "radius": 2 * mm});
            skCircle(sketch, "E6.0.34.8", {"center": v(226.1, -171.9) * mm, "radius": 2 * mm});
            skCircle(sketch, "E6.0.34.9", {"center": v(226.1, -155.9) * mm, "radius": 2 * mm});
            skCircle(sketch, "E6.0.35.8", {"center": v(242.1, -171.9) * mm, "radius": 2 * mm});
            skCircle(sketch, "E6.0.35.9", {"center": v(242.1, -155.9) * mm, "radius": 2 * mm});
            skCircle(sketch, "E6.0.36.8", {"center": v(258.1, -171.9) * mm, "radius": 2 * mm});
            skCircle(sketch, "E6.0.36.9", {"center": v(258.1, -155.9) * mm, "radius": 2 * mm});
            skCircle(sketch, "E6.0.37.8", {"center": v(274.1, -171.9) * mm, "radius": 2 * mm});
            skCircle(sketch, "E6.0.37.9", {"center": v(274.1, -155.9) * mm, "radius": 2 * mm});
            skCircle(sketch, "E6.0.38.8", {"center": v(290.1, -171.9) * mm, "radius": 2 * mm});
            skCircle(sketch, "E6.0.38.9", {"center": v(290.1, -155.9) * mm, "radius": 2 * mm});
            skCircle(sketch, "E6.0.39.8", {"center": v(306.1, -171.9) * mm, "radius": 2 * mm});
            skCircle(sketch, "E6.0.39.9", {"center": v(306.1, -155.9) * mm, "radius": 2 * mm});
            skCircle(sketch, "E7.0.0.10", {"center": v(-317.9, -139.9) * mm, "radius": 2 * mm});
            skCircle(sketch, "E7.0.0.11", {"center": v(-317.9, -123.9) * mm, "radius": 2 * mm});
            skCircle(sketch, "E7.0.0.12", {"center": v(-317.9, -107.9) * mm, "radius": 2 * mm});
            skCircle(sketch, "E7.0.0.13", {"center": v(-317.9, -91.9) * mm, "radius": 2 * mm});
            skCircle(sketch, "E7.0.0.14", {"center": v(-317.9, -75.9) * mm, "radius": 2 * mm});
            skCircle(sketch, "E7.0.0.15", {"center": v(-317.9, -59.9) * mm, "radius": 2 * mm});
            skCircle(sketch, "E7.0.0.16", {"center": v(-317.9, -43.9) * mm, "radius": 2 * mm});
            skCircle(sketch, "E7.0.0.17", {"center": v(-317.9, -27.9) * mm, "radius": 2 * mm});
            skCircle(sketch, "E7.0.0.18", {"center": v(-317.9, -11.9) * mm, "radius": 2 * mm});
            skCircle(sketch, "E7.0.0.19", {"center": v(-317.9, 4.1) * mm, "radius": 2 * mm});
            skCircle(sketch, "E7.0.0.20", {"center": v(-317.9, 20.1) * mm, "radius": 2 * mm});
            skCircle(sketch, "E7.0.0.21", {"center": v(-317.9, 36.1) * mm, "radius": 2 * mm});
            skCircle(sketch, "E7.0.0.22", {"center": v(-317.9, 52.1) * mm, "radius": 2 * mm});
            skCircle(sketch, "E7.0.0.23", {"center": v(-317.9, 68.1) * mm, "radius": 2 * mm});
            skCircle(sketch, "E7.0.0.24", {"center": v(-317.9, 84.1) * mm, "radius": 2 * mm});
            skCircle(sketch, "E7.0.0.25", {"center": v(-317.9, 100.1) * mm, "radius": 2 * mm});
            skCircle(sketch, "E7.0.0.26", {"center": v(-317.9, 116.1) * mm, "radius": 2 * mm});
            skCircle(sketch, "E7.0.0.27", {"center": v(-317.9, 132.1) * mm, "radius": 2 * mm});
            skCircle(sketch, "E7.0.0.28", {"center": v(-317.9, 148.1) * mm, "radius": 2 * mm});
            skCircle(sketch, "E7.0.0.29", {"center": v(-317.9, 164.1) * mm, "radius": 2 * mm});
            skCircle(sketch, "E7.0.0.30", {"center": v(-317.9, 180.1) * mm, "radius": 2 * mm});
            skCircle(sketch, "E7.0.0.31", {"center": v(-317.9, 196.1) * mm, "radius": 2 * mm});
            skCircle(sketch, "E7.0.0.32", {"center": v(-317.9, 212.1) * mm, "radius": 2 * mm});
            skCircle(sketch, "E7.0.0.33", {"center": v(-317.9, 228.1) * mm, "radius": 2 * mm});
            skCircle(sketch, "E7.0.0.34", {"center": v(-317.9, 244.1) * mm, "radius": 2 * mm});
            skCircle(sketch, "E7.0.0.35", {"center": v(-317.9, 260.1) * mm, "radius": 2 * mm});
            skCircle(sketch, "E7.0.0.36", {"center": v(-317.9, 276.1) * mm, "radius": 2 * mm});
            skCircle(sketch, "E7.0.0.37", {"center": v(-317.9, 292.1) * mm, "radius": 2 * mm});
            skCircle(sketch, "E7.0.1.10", {"center": v(-301.9, -139.9) * mm, "radius": 2 * mm});
            skCircle(sketch, "E7.0.1.11", {"center": v(-301.9, -123.9) * mm, "radius": 2 * mm});
            skCircle(sketch, "E7.0.1.12", {"center": v(-301.9, -107.9) * mm, "radius": 2 * mm});
            skCircle(sketch, "E7.0.1.13", {"center": v(-301.9, -91.9) * mm, "radius": 2 * mm});
            skCircle(sketch, "E7.0.1.14", {"center": v(-301.9, -75.9) * mm, "radius": 2 * mm});
            skCircle(sketch, "E7.0.1.15", {"center": v(-301.9, -59.9) * mm, "radius": 2 * mm});
            skCircle(sketch, "E7.0.1.16", {"center": v(-301.9, -43.9) * mm, "radius": 2 * mm});
            skCircle(sketch, "E7.0.1.17", {"center": v(-301.9, -27.9) * mm, "radius": 2 * mm});
            skCircle(sketch, "E7.0.1.18", {"center": v(-301.9, -11.9) * mm, "radius": 2 * mm});
            skCircle(sketch, "E7.0.1.19", {"center": v(-301.9, 4.1) * mm, "radius": 2 * mm});
            skCircle(sketch, "E7.0.1.20", {"center": v(-301.9, 20.1) * mm, "radius": 2 * mm});
            skCircle(sketch, "E7.0.1.21", {"center": v(-301.9, 36.1) * mm, "radius": 2 * mm});
            skCircle(sketch, "E7.0.1.22", {"center": v(-301.9, 52.1) * mm, "radius": 2 * mm});
            skCircle(sketch, "E7.0.1.23", {"center": v(-301.9, 68.1) * mm, "radius": 2 * mm});
            skCircle(sketch, "E7.0.1.24", {"center": v(-301.9, 84.1) * mm, "radius": 2 * mm});
            skCircle(sketch, "E7.0.1.25", {"center": v(-301.9, 100.1) * mm, "radius": 2 * mm});
            skCircle(sketch, "E7.0.1.26", {"center": v(-301.9, 116.1) * mm, "radius": 2 * mm});
            skCircle(sketch, "E7.0.1.27", {"center": v(-301.9, 132.1) * mm, "radius": 2 * mm});
            skCircle(sketch, "E7.0.1.28", {"center": v(-301.9, 148.1) * mm, "radius": 2 * mm});
            skCircle(sketch, "E7.0.1.29", {"center": v(-301.9, 164.1) * mm, "radius": 2 * mm});
            skCircle(sketch, "E7.0.1.30", {"center": v(-301.9, 180.1) * mm, "radius": 2 * mm});
            skCircle(sketch, "E7.0.1.31", {"center": v(-301.9, 196.1) * mm, "radius": 2 * mm});
            skCircle(sketch, "E7.0.1.32", {"center": v(-301.9, 212.1) * mm, "radius": 2 * mm});
            skCircle(sketch, "E7.0.1.33", {"center": v(-301.9, 228.1) * mm, "radius": 2 * mm});
            skCircle(sketch, "E7.0.1.34", {"center": v(-301.9, 244.1) * mm, "radius": 2 * mm});
            skCircle(sketch, "E7.0.1.35", {"center": v(-301.9, 260.1) * mm, "radius": 2 * mm});
            skCircle(sketch, "E7.0.1.36", {"center": v(-301.9, 276.1) * mm, "radius": 2 * mm});
            skCircle(sketch, "E7.0.1.37", {"center": v(-301.9, 292.1) * mm, "radius": 2 * mm});
            skCircle(sketch, "E7.0.2.10", {"center": v(-285.9, -139.9) * mm, "radius": 2 * mm});
            skCircle(sketch, "E7.0.2.11", {"center": v(-285.9, -123.9) * mm, "radius": 2 * mm});
            skCircle(sketch, "E7.0.2.12", {"center": v(-285.9, -107.9) * mm, "radius": 2 * mm});
            skCircle(sketch, "E7.0.2.13", {"center": v(-285.9, -91.9) * mm, "radius": 2 * mm});
            skCircle(sketch, "E7.0.2.14", {"center": v(-285.9, -75.9) * mm, "radius": 2 * mm});
            skCircle(sketch, "E7.0.2.15", {"center": v(-285.9, -59.9) * mm, "radius": 2 * mm});
            skCircle(sketch, "E7.0.2.16", {"center": v(-285.9, -43.9) * mm, "radius": 2 * mm});
            skCircle(sketch, "E7.0.2.17", {"center": v(-285.9, -27.9) * mm, "radius": 2 * mm});
            skCircle(sketch, "E7.0.2.18", {"center": v(-285.9, -11.9) * mm, "radius": 2 * mm});
            skCircle(sketch, "E7.0.2.19", {"center": v(-285.9, 4.1) * mm, "radius": 2 * mm});
            skCircle(sketch, "E7.0.2.20", {"center": v(-285.9, 20.1) * mm, "radius": 2 * mm});
            skCircle(sketch, "E7.0.2.21", {"center": v(-285.9, 36.1) * mm, "radius": 2 * mm});
            skCircle(sketch, "E7.0.2.22", {"center": v(-285.9, 52.1) * mm, "radius": 2 * mm});
            skCircle(sketch, "E7.0.2.23", {"center": v(-285.9, 68.1) * mm, "radius": 2 * mm});
            skCircle(sketch, "E7.0.2.24", {"center": v(-285.9, 84.1) * mm, "radius": 2 * mm});
            skCircle(sketch, "E7.0.2.25", {"center": v(-285.9, 100.1) * mm, "radius": 2 * mm});
            skCircle(sketch, "E7.0.2.26", {"center": v(-285.9, 116.1) * mm, "radius": 2 * mm});
            skCircle(sketch, "E7.0.2.27", {"center": v(-285.9, 132.1) * mm, "radius": 2 * mm});
            skCircle(sketch, "E7.0.2.28", {"center": v(-285.9, 148.1) * mm, "radius": 2 * mm});
            skCircle(sketch, "E7.0.2.29", {"center": v(-285.9, 164.1) * mm, "radius": 2 * mm});
            skCircle(sketch, "E7.0.2.30", {"center": v(-285.9, 180.1) * mm, "radius": 2 * mm});
            skCircle(sketch, "E7.0.2.31", {"center": v(-285.9, 196.1) * mm, "radius": 2 * mm});
            skCircle(sketch, "E7.0.2.32", {"center": v(-285.9, 212.1) * mm, "radius": 2 * mm});
            skCircle(sketch, "E7.0.2.33", {"center": v(-285.9, 228.1) * mm, "radius": 2 * mm});
            skCircle(sketch, "E7.0.2.34", {"center": v(-285.9, 244.1) * mm, "radius": 2 * mm});
            skCircle(sketch, "E7.0.2.35", {"center": v(-285.9, 260.1) * mm, "radius": 2 * mm});
            skCircle(sketch, "E7.0.2.36", {"center": v(-285.9, 276.1) * mm, "radius": 2 * mm});
            skCircle(sketch, "E7.0.2.37", {"center": v(-285.9, 292.1) * mm, "radius": 2 * mm});
            skCircle(sketch, "E7.0.3.10", {"center": v(-269.9, -139.9) * mm, "radius": 2 * mm});
            skCircle(sketch, "E7.0.3.11", {"center": v(-269.9, -123.9) * mm, "radius": 2 * mm});
            skCircle(sketch, "E7.0.3.12", {"center": v(-269.9, -107.9) * mm, "radius": 2 * mm});
            skCircle(sketch, "E7.0.3.13", {"center": v(-269.9, -91.9) * mm, "radius": 2 * mm});
            skCircle(sketch, "E7.0.3.14", {"center": v(-269.9, -75.9) * mm, "radius": 2 * mm});
            skCircle(sketch, "E7.0.3.15", {"center": v(-269.9, -59.9) * mm, "radius": 2 * mm});
            skCircle(sketch, "E7.0.3.16", {"center": v(-269.9, -43.9) * mm, "radius": 2 * mm});
            skCircle(sketch, "E7.0.3.17", {"center": v(-269.9, -27.9) * mm, "radius": 2 * mm});
            skCircle(sketch, "E7.0.3.18", {"center": v(-269.9, -11.9) * mm, "radius": 2 * mm});
            skCircle(sketch, "E7.0.3.19", {"center": v(-269.9, 4.1) * mm, "radius": 2 * mm});
            skCircle(sketch, "E7.0.3.20", {"center": v(-269.9, 20.1) * mm, "radius": 2 * mm});
            skCircle(sketch, "E7.0.3.21", {"center": v(-269.9, 36.1) * mm, "radius": 2 * mm});
            skCircle(sketch, "E7.0.3.22", {"center": v(-269.9, 52.1) * mm, "radius": 2 * mm});
            skCircle(sketch, "E7.0.3.23", {"center": v(-269.9, 68.1) * mm, "radius": 2 * mm});
            skCircle(sketch, "E7.0.3.24", {"center": v(-269.9, 84.1) * mm, "radius": 2 * mm});
            skCircle(sketch, "E7.0.3.25", {"center": v(-269.9, 100.1) * mm, "radius": 2 * mm});
            skCircle(sketch, "E7.0.3.26", {"center": v(-269.9, 116.1) * mm, "radius": 2 * mm});
            skCircle(sketch, "E7.0.3.27", {"center": v(-269.9, 132.1) * mm, "radius": 2 * mm});
            skCircle(sketch, "E7.0.3.28", {"center": v(-269.9, 148.1) * mm, "radius": 2 * mm});
            skCircle(sketch, "E7.0.3.29", {"center": v(-269.9, 164.1) * mm, "radius": 2 * mm});
            skCircle(sketch, "E7.0.3.30", {"center": v(-269.9, 180.1) * mm, "radius": 2 * mm});
            skCircle(sketch, "E7.0.3.31", {"center": v(-269.9, 196.1) * mm, "radius": 2 * mm});
            skCircle(sketch, "E7.0.3.32", {"center": v(-269.9, 212.1) * mm, "radius": 2 * mm});
            skCircle(sketch, "E7.0.3.33", {"center": v(-269.9, 228.1) * mm, "radius": 2 * mm});
            skCircle(sketch, "E7.0.3.34", {"center": v(-269.9, 244.1) * mm, "radius": 2 * mm});
            skCircle(sketch, "E7.0.3.35", {"center": v(-269.9, 260.1) * mm, "radius": 2 * mm});
            skCircle(sketch, "E7.0.3.36", {"center": v(-269.9, 276.1) * mm, "radius": 2 * mm});
            skCircle(sketch, "E7.0.3.37", {"center": v(-269.9, 292.1) * mm, "radius": 2 * mm});
            skCircle(sketch, "E7.0.4.10", {"center": v(-253.9, -139.9) * mm, "radius": 2 * mm});
            skCircle(sketch, "E7.0.4.11", {"center": v(-253.9, -123.9) * mm, "radius": 2 * mm});
            skCircle(sketch, "E7.0.4.12", {"center": v(-253.9, -107.9) * mm, "radius": 2 * mm});
            skCircle(sketch, "E7.0.4.13", {"center": v(-253.9, -91.9) * mm, "radius": 2 * mm});
            skCircle(sketch, "E7.0.4.14", {"center": v(-253.9, -75.9) * mm, "radius": 2 * mm});
            skCircle(sketch, "E7.0.4.15", {"center": v(-253.9, -59.9) * mm, "radius": 2 * mm});
            skCircle(sketch, "E7.0.4.16", {"center": v(-253.9, -43.9) * mm, "radius": 2 * mm});
            skCircle(sketch, "E7.0.4.17", {"center": v(-253.9, -27.9) * mm, "radius": 2 * mm});
            skCircle(sketch, "E7.0.4.18", {"center": v(-253.9, -11.9) * mm, "radius": 2 * mm});
            skCircle(sketch, "E7.0.4.19", {"center": v(-253.9, 4.1) * mm, "radius": 2 * mm});
            skCircle(sketch, "E7.0.4.20", {"center": v(-253.9, 20.1) * mm, "radius": 2 * mm});
            skCircle(sketch, "E7.0.4.21", {"center": v(-253.9, 36.1) * mm, "radius": 2 * mm});
            skCircle(sketch, "E7.0.4.22", {"center": v(-253.9, 52.1) * mm, "radius": 2 * mm});
            skCircle(sketch, "E7.0.4.23", {"center": v(-253.9, 68.1) * mm, "radius": 2 * mm});
            skCircle(sketch, "E7.0.4.24", {"center": v(-253.9, 84.1) * mm, "radius": 2 * mm});
            skCircle(sketch, "E7.0.4.25", {"center": v(-253.9, 100.1) * mm, "radius": 2 * mm});
            skCircle(sketch, "E7.0.4.26", {"center": v(-253.9, 116.1) * mm, "radius": 2 * mm});
            skCircle(sketch, "E7.0.4.27", {"center": v(-253.9, 132.1) * mm, "radius": 2 * mm});
            skCircle(sketch, "E7.0.4.28", {"center": v(-253.9, 148.1) * mm, "radius": 2 * mm});
            skCircle(sketch, "E7.0.4.29", {"center": v(-253.9, 164.1) * mm, "radius": 2 * mm});
            skCircle(sketch, "E7.0.4.30", {"center": v(-253.9, 180.1) * mm, "radius": 2 * mm});
            skCircle(sketch, "E7.0.4.31", {"center": v(-253.9, 196.1) * mm, "radius": 2 * mm});
            skCircle(sketch, "E7.0.4.32", {"center": v(-253.9, 212.1) * mm, "radius": 2 * mm});
            skCircle(sketch, "E7.0.4.33", {"center": v(-253.9, 228.1) * mm, "radius": 2 * mm});
            skCircle(sketch, "E7.0.4.34", {"center": v(-253.9, 244.1) * mm, "radius": 2 * mm});
            skCircle(sketch, "E7.0.4.35", {"center": v(-253.9, 260.1) * mm, "radius": 2 * mm});
            skCircle(sketch, "E7.0.4.36", {"center": v(-253.9, 276.1) * mm, "radius": 2 * mm});
            skCircle(sketch, "E7.0.4.37", {"center": v(-253.9, 292.1) * mm, "radius": 2 * mm});
            skCircle(sketch, "E7.0.5.10", {"center": v(-237.9, -139.9) * mm, "radius": 2 * mm});
            skCircle(sketch, "E7.0.5.11", {"center": v(-237.9, -123.9) * mm, "radius": 2 * mm});
            skCircle(sketch, "E7.0.5.12", {"center": v(-237.9, -107.9) * mm, "radius": 2 * mm});
            skCircle(sketch, "E7.0.5.13", {"center": v(-237.9, -91.9) * mm, "radius": 2 * mm});
            skCircle(sketch, "E7.0.5.14", {"center": v(-237.9, -75.9) * mm, "radius": 2 * mm});
            skCircle(sketch, "E7.0.5.15", {"center": v(-237.9, -59.9) * mm, "radius": 2 * mm});
            skCircle(sketch, "E7.0.5.16", {"center": v(-237.9, -43.9) * mm, "radius": 2 * mm});
            skCircle(sketch, "E7.0.5.17", {"center": v(-237.9, -27.9) * mm, "radius": 2 * mm});
            skCircle(sketch, "E7.0.5.18", {"center": v(-237.9, -11.9) * mm, "radius": 2 * mm});
            skCircle(sketch, "E7.0.5.19", {"center": v(-237.9, 4.1) * mm, "radius": 2 * mm});
            skCircle(sketch, "E7.0.5.20", {"center": v(-237.9, 20.1) * mm, "radius": 2 * mm});
            skCircle(sketch, "E7.0.5.21", {"center": v(-237.9, 36.1) * mm, "radius": 2 * mm});
            skCircle(sketch, "E7.0.5.22", {"center": v(-237.9, 52.1) * mm, "radius": 2 * mm});
            skCircle(sketch, "E7.0.5.23", {"center": v(-237.9, 68.1) * mm, "radius": 2 * mm});
            skCircle(sketch, "E7.0.5.24", {"center": v(-237.9, 84.1) * mm, "radius": 2 * mm});
            skCircle(sketch, "E7.0.5.25", {"center": v(-237.9, 100.1) * mm, "radius": 2 * mm});
            skCircle(sketch, "E7.0.5.26", {"center": v(-237.9, 116.1) * mm, "radius": 2 * mm});
            skCircle(sketch, "E7.0.5.27", {"center": v(-237.9, 132.1) * mm, "radius": 2 * mm});
            skCircle(sketch, "E7.0.5.28", {"center": v(-237.9, 148.1) * mm, "radius": 2 * mm});
            skCircle(sketch, "E7.0.5.29", {"center": v(-237.9, 164.1) * mm, "radius": 2 * mm});
            skCircle(sketch, "E7.0.5.30", {"center": v(-237.9, 180.1) * mm, "radius": 2 * mm});
            skCircle(sketch, "E7.0.5.31", {"center": v(-237.9, 196.1) * mm, "radius": 2 * mm});
            skCircle(sketch, "E7.0.5.32", {"center": v(-237.9, 212.1) * mm, "radius": 2 * mm});
            skCircle(sketch, "E7.0.5.33", {"center": v(-237.9, 228.1) * mm, "radius": 2 * mm});
            skCircle(sketch, "E7.0.5.34", {"center": v(-237.9, 244.1) * mm, "radius": 2 * mm});
            skCircle(sketch, "E7.0.5.35", {"center": v(-237.9, 260.1) * mm, "radius": 2 * mm});
            skCircle(sketch, "E7.0.5.36", {"center": v(-237.9, 276.1) * mm, "radius": 2 * mm});
            skCircle(sketch, "E7.0.5.37", {"center": v(-237.9, 292.1) * mm, "radius": 2 * mm});
            skCircle(sketch, "E7.0.6.10", {"center": v(-221.9, -139.9) * mm, "radius": 2 * mm});
            skCircle(sketch, "E7.0.6.11", {"center": v(-221.9, -123.9) * mm, "radius": 2 * mm});
            skCircle(sketch, "E7.0.6.12", {"center": v(-221.9, -107.9) * mm, "radius": 2 * mm});
            skCircle(sketch, "E7.0.6.13", {"center": v(-221.9, -91.9) * mm, "radius": 2 * mm});
            skCircle(sketch, "E7.0.6.14", {"center": v(-221.9, -75.9) * mm, "radius": 2 * mm});
            skCircle(sketch, "E7.0.6.15", {"center": v(-221.9, -59.9) * mm, "radius": 2 * mm});
            skCircle(sketch, "E7.0.6.16", {"center": v(-221.9, -43.9) * mm, "radius": 2 * mm});
            skCircle(sketch, "E7.0.6.17", {"center": v(-221.9, -27.9) * mm, "radius": 2 * mm});
            skCircle(sketch, "E7.0.6.18", {"center": v(-221.9, -11.9) * mm, "radius": 2 * mm});
            skCircle(sketch, "E7.0.6.19", {"center": v(-221.9, 4.1) * mm, "radius": 2 * mm});
            skCircle(sketch, "E7.0.6.20", {"center": v(-221.9, 20.1) * mm, "radius": 2 * mm});
            skCircle(sketch, "E7.0.6.21", {"center": v(-221.9, 36.1) * mm, "radius": 2 * mm});
            skCircle(sketch, "E7.0.6.22", {"center": v(-221.9, 52.1) * mm, "radius": 2 * mm});
            skCircle(sketch, "E7.0.6.23", {"center": v(-221.9, 68.1) * mm, "radius": 2 * mm});
            skCircle(sketch, "E7.0.6.24", {"center": v(-221.9, 84.1) * mm, "radius": 2 * mm});
            skCircle(sketch, "E7.0.6.25", {"center": v(-221.9, 100.1) * mm, "radius": 2 * mm});
            skCircle(sketch, "E7.0.6.26", {"center": v(-221.9, 116.1) * mm, "radius": 2 * mm});
            skCircle(sketch, "E7.0.6.27", {"center": v(-221.9, 132.1) * mm, "radius": 2 * mm});
            skCircle(sketch, "E7.0.6.28", {"center": v(-221.9, 148.1) * mm, "radius": 2 * mm});
            skCircle(sketch, "E7.0.6.29", {"center": v(-221.9, 164.1) * mm, "radius": 2 * mm});
            skCircle(sketch, "E7.0.6.30", {"center": v(-221.9, 180.1) * mm, "radius": 2 * mm});
            skCircle(sketch, "E7.0.6.31", {"center": v(-221.9, 196.1) * mm, "radius": 2 * mm});
            skCircle(sketch, "E7.0.6.32", {"center": v(-221.9, 212.1) * mm, "radius": 2 * mm});
            skCircle(sketch, "E7.0.6.33", {"center": v(-221.9, 228.1) * mm, "radius": 2 * mm});
            skCircle(sketch, "E7.0.6.34", {"center": v(-221.9, 244.1) * mm, "radius": 2 * mm});
            skCircle(sketch, "E7.0.6.35", {"center": v(-221.9, 260.1) * mm, "radius": 2 * mm});
            skCircle(sketch, "E7.0.6.36", {"center": v(-221.9, 276.1) * mm, "radius": 2 * mm});
            skCircle(sketch, "E7.0.6.37", {"center": v(-221.9, 292.1) * mm, "radius": 2 * mm});
            skCircle(sketch, "E7.0.7.10", {"center": v(-205.9, -139.9) * mm, "radius": 2 * mm});
            skCircle(sketch, "E7.0.7.11", {"center": v(-205.9, -123.9) * mm, "radius": 2 * mm});
            skCircle(sketch, "E7.0.7.12", {"center": v(-205.9, -107.9) * mm, "radius": 2 * mm});
            skCircle(sketch, "E7.0.7.13", {"center": v(-205.9, -91.9) * mm, "radius": 2 * mm});
            skCircle(sketch, "E7.0.7.14", {"center": v(-205.9, -75.9) * mm, "radius": 2 * mm});
            skCircle(sketch, "E7.0.7.15", {"center": v(-205.9, -59.9) * mm, "radius": 2 * mm});
            skCircle(sketch, "E7.0.7.16", {"center": v(-205.9, -43.9) * mm, "radius": 2 * mm});
            skCircle(sketch, "E7.0.7.17", {"center": v(-205.9, -27.9) * mm, "radius": 2 * mm});
            skCircle(sketch, "E7.0.7.18", {"center": v(-205.9, -11.9) * mm, "radius": 2 * mm});
            skCircle(sketch, "E7.0.7.19", {"center": v(-205.9, 4.1) * mm, "radius": 2 * mm});
            skCircle(sketch, "E7.0.7.20", {"center": v(-205.9, 20.1) * mm, "radius": 2 * mm});
            skCircle(sketch, "E7.0.7.21", {"center": v(-205.9, 36.1) * mm, "radius": 2 * mm});
            skCircle(sketch, "E7.0.7.22", {"center": v(-205.9, 52.1) * mm, "radius": 2 * mm});
            skCircle(sketch, "E7.0.7.23", {"center": v(-205.9, 68.1) * mm, "radius": 2 * mm});
            skCircle(sketch, "E7.0.7.24", {"center": v(-205.9, 84.1) * mm, "radius": 2 * mm});
            skCircle(sketch, "E7.0.7.25", {"center": v(-205.9, 100.1) * mm, "radius": 2 * mm});
            skCircle(sketch, "E7.0.7.26", {"center": v(-205.9, 116.1) * mm, "radius": 2 * mm});
            skCircle(sketch, "E7.0.7.27", {"center": v(-205.9, 132.1) * mm, "radius": 2 * mm});
            skCircle(sketch, "E7.0.7.28", {"center": v(-205.9, 148.1) * mm, "radius": 2 * mm});
            skCircle(sketch, "E7.0.7.29", {"center": v(-205.9, 164.1) * mm, "radius": 2 * mm});
            skCircle(sketch, "E7.0.7.30", {"center": v(-205.9, 180.1) * mm, "radius": 2 * mm});
            skCircle(sketch, "E7.0.7.31", {"center": v(-205.9, 196.1) * mm, "radius": 2 * mm});
            skCircle(sketch, "E7.0.7.32", {"center": v(-205.9, 212.1) * mm, "radius": 2 * mm});
            skCircle(sketch, "E7.0.7.33", {"center": v(-205.9, 228.1) * mm, "radius": 2 * mm});
            skCircle(sketch, "E7.0.7.34", {"center": v(-205.9, 244.1) * mm, "radius": 2 * mm});
            skCircle(sketch, "E7.0.7.35", {"center": v(-205.9, 260.1) * mm, "radius": 2 * mm});
            skCircle(sketch, "E7.0.7.36", {"center": v(-205.9, 276.1) * mm, "radius": 2 * mm});
            skCircle(sketch, "E7.0.7.37", {"center": v(-205.9, 292.1) * mm, "radius": 2 * mm});
            skCircle(sketch, "E7.0.8.10", {"center": v(-189.9, -139.9) * mm, "radius": 2 * mm});
            skCircle(sketch, "E7.0.8.11", {"center": v(-189.9, -123.9) * mm, "radius": 2 * mm});
            skCircle(sketch, "E7.0.8.12", {"center": v(-189.9, -107.9) * mm, "radius": 2 * mm});
            skCircle(sketch, "E7.0.8.13", {"center": v(-189.9, -91.9) * mm, "radius": 2 * mm});
            skCircle(sketch, "E7.0.8.14", {"center": v(-189.9, -75.9) * mm, "radius": 2 * mm});
            skCircle(sketch, "E7.0.8.15", {"center": v(-189.9, -59.9) * mm, "radius": 2 * mm});
            skCircle(sketch, "E7.0.8.16", {"center": v(-189.9, -43.9) * mm, "radius": 2 * mm});
            skCircle(sketch, "E7.0.8.17", {"center": v(-189.9, -27.9) * mm, "radius": 2 * mm});
            skCircle(sketch, "E7.0.8.18", {"center": v(-189.9, -11.9) * mm, "radius": 2 * mm});
            skCircle(sketch, "E7.0.8.19", {"center": v(-189.9, 4.1) * mm, "radius": 2 * mm});
            skCircle(sketch, "E7.0.8.20", {"center": v(-189.9, 20.1) * mm, "radius": 2 * mm});
            skCircle(sketch, "E7.0.8.21", {"center": v(-189.9, 36.1) * mm, "radius": 2 * mm});
            skCircle(sketch, "E7.0.8.22", {"center": v(-189.9, 52.1) * mm, "radius": 2 * mm});
            skCircle(sketch, "E7.0.8.23", {"center": v(-189.9, 68.1) * mm, "radius": 2 * mm});
            skCircle(sketch, "E7.0.8.24", {"center": v(-189.9, 84.1) * mm, "radius": 2 * mm});
            skCircle(sketch, "E7.0.8.25", {"center": v(-189.9, 100.1) * mm, "radius": 2 * mm});
            skCircle(sketch, "E7.0.8.26", {"center": v(-189.9, 116.1) * mm, "radius": 2 * mm});
            skCircle(sketch, "E7.0.8.27", {"center": v(-189.9, 132.1) * mm, "radius": 2 * mm});
            skCircle(sketch, "E7.0.8.28", {"center": v(-189.9, 148.1) * mm, "radius": 2 * mm});
            skCircle(sketch, "E7.0.8.29", {"center": v(-189.9, 164.1) * mm, "radius": 2 * mm});
            skCircle(sketch, "E7.0.8.30", {"center": v(-189.9, 180.1) * mm, "radius": 2 * mm});
            skCircle(sketch, "E7.0.8.31", {"center": v(-189.9, 196.1) * mm, "radius": 2 * mm});
            skCircle(sketch, "E7.0.8.32", {"center": v(-189.9, 212.1) * mm, "radius": 2 * mm});
            skCircle(sketch, "E7.0.8.33", {"center": v(-189.9, 228.1) * mm, "radius": 2 * mm});
            skCircle(sketch, "E7.0.8.34", {"center": v(-189.9, 244.1) * mm, "radius": 2 * mm});
            skCircle(sketch, "E7.0.8.35", {"center": v(-189.9, 260.1) * mm, "radius": 2 * mm});
            skCircle(sketch, "E7.0.8.36", {"center": v(-189.9, 276.1) * mm, "radius": 2 * mm});
            skCircle(sketch, "E7.0.8.37", {"center": v(-189.9, 292.1) * mm, "radius": 2 * mm});
            skCircle(sketch, "E7.0.9.10", {"center": v(-173.9, -139.9) * mm, "radius": 2 * mm});
            skCircle(sketch, "E7.0.9.11", {"center": v(-173.9, -123.9) * mm, "radius": 2 * mm});
            skCircle(sketch, "E7.0.9.12", {"center": v(-173.9, -107.9) * mm, "radius": 2 * mm});
            skCircle(sketch, "E7.0.9.13", {"center": v(-173.9, -91.9) * mm, "radius": 2 * mm});
            skCircle(sketch, "E7.0.9.14", {"center": v(-173.9, -75.9) * mm, "radius": 2 * mm});
            skCircle(sketch, "E7.0.9.15", {"center": v(-173.9, -59.9) * mm, "radius": 2 * mm});
            skCircle(sketch, "E7.0.9.16", {"center": v(-173.9, -43.9) * mm, "radius": 2 * mm});
            skCircle(sketch, "E7.0.9.17", {"center": v(-173.9, -27.9) * mm, "radius": 2 * mm});
            skCircle(sketch, "E7.0.9.18", {"center": v(-173.9, -11.9) * mm, "radius": 2 * mm});
            skCircle(sketch, "E7.0.9.19", {"center": v(-173.9, 4.1) * mm, "radius": 2 * mm});
            skCircle(sketch, "E7.0.9.20", {"center": v(-173.9, 20.1) * mm, "radius": 2 * mm});
            skCircle(sketch, "E7.0.9.21", {"center": v(-173.9, 36.1) * mm, "radius": 2 * mm});
            skCircle(sketch, "E7.0.9.22", {"center": v(-173.9, 52.1) * mm, "radius": 2 * mm});
            skCircle(sketch, "E7.0.9.23", {"center": v(-173.9, 68.1) * mm, "radius": 2 * mm});
            skCircle(sketch, "E7.0.9.24", {"center": v(-173.9, 84.1) * mm, "radius": 2 * mm});
            skCircle(sketch, "E7.0.9.25", {"center": v(-173.9, 100.1) * mm, "radius": 2 * mm});
            skCircle(sketch, "E7.0.9.26", {"center": v(-173.9, 116.1) * mm, "radius": 2 * mm});
            skCircle(sketch, "E7.0.9.27", {"center": v(-173.9, 132.1) * mm, "radius": 2 * mm});
            skCircle(sketch, "E7.0.9.28", {"center": v(-173.9, 148.1) * mm, "radius": 2 * mm});
            skCircle(sketch, "E7.0.9.29", {"center": v(-173.9, 164.1) * mm, "radius": 2 * mm});
            skCircle(sketch, "E7.0.9.30", {"center": v(-173.9, 180.1) * mm, "radius": 2 * mm});
            skCircle(sketch, "E7.0.9.31", {"center": v(-173.9, 196.1) * mm, "radius": 2 * mm});
            skCircle(sketch, "E7.0.9.32", {"center": v(-173.9, 212.1) * mm, "radius": 2 * mm});
            skCircle(sketch, "E7.0.9.33", {"center": v(-173.9, 228.1) * mm, "radius": 2 * mm});
            skCircle(sketch, "E7.0.9.34", {"center": v(-173.9, 244.1) * mm, "radius": 2 * mm});
            skCircle(sketch, "E7.0.9.35", {"center": v(-173.9, 260.1) * mm, "radius": 2 * mm});
            skCircle(sketch, "E7.0.9.36", {"center": v(-173.9, 276.1) * mm, "radius": 2 * mm});
            skCircle(sketch, "E7.0.9.37", {"center": v(-173.9, 292.1) * mm, "radius": 2 * mm});
            skCircle(sketch, "E7.0.10.10", {"center": v(-157.9, -139.9) * mm, "radius": 2 * mm});
            skCircle(sketch, "E7.0.10.11", {"center": v(-157.9, -123.9) * mm, "radius": 2 * mm});
            skCircle(sketch, "E7.0.10.12", {"center": v(-157.9, -107.9) * mm, "radius": 2 * mm});
            skCircle(sketch, "E7.0.10.13", {"center": v(-157.9, -91.9) * mm, "radius": 2 * mm});
            skCircle(sketch, "E7.0.10.14", {"center": v(-157.9, -75.9) * mm, "radius": 2 * mm});
            skCircle(sketch, "E7.0.10.15", {"center": v(-157.9, -59.9) * mm, "radius": 2 * mm});
            skCircle(sketch, "E7.0.10.16", {"center": v(-157.9, -43.9) * mm, "radius": 2 * mm});
            skCircle(sketch, "E7.0.10.17", {"center": v(-157.9, -27.9) * mm, "radius": 2 * mm});
            skCircle(sketch, "E7.0.10.18", {"center": v(-157.9, -11.9) * mm, "radius": 2 * mm});
            skCircle(sketch, "E7.0.10.19", {"center": v(-157.9, 4.1) * mm, "radius": 2 * mm});
            skCircle(sketch, "E7.0.10.20", {"center": v(-157.9, 20.1) * mm, "radius": 2 * mm});
            skCircle(sketch, "E7.0.10.21", {"center": v(-157.9, 36.1) * mm, "radius": 2 * mm});
            skCircle(sketch, "E7.0.10.22", {"center": v(-157.9, 52.1) * mm, "radius": 2 * mm});
            skCircle(sketch, "E7.0.10.23", {"center": v(-157.9, 68.1) * mm, "radius": 2 * mm});
            skCircle(sketch, "E7.0.10.24", {"center": v(-157.9, 84.1) * mm, "radius": 2 * mm});
            skCircle(sketch, "E7.0.10.25", {"center": v(-157.9, 100.1) * mm, "radius": 2 * mm});
            skCircle(sketch, "E7.0.10.26", {"center": v(-157.9, 116.1) * mm, "radius": 2 * mm});
            skCircle(sketch, "E7.0.10.27", {"center": v(-157.9, 132.1) * mm, "radius": 2 * mm});
            skCircle(sketch, "E7.0.10.28", {"center": v(-157.9, 148.1) * mm, "radius": 2 * mm});
            skCircle(sketch, "E7.0.10.29", {"center": v(-157.9, 164.1) * mm, "radius": 2 * mm});
            skCircle(sketch, "E7.0.10.30", {"center": v(-157.9, 180.1) * mm, "radius": 2 * mm});
            skCircle(sketch, "E7.0.10.31", {"center": v(-157.9, 196.1) * mm, "radius": 2 * mm});
            skCircle(sketch, "E7.0.10.32", {"center": v(-157.9, 212.1) * mm, "radius": 2 * mm});
            skCircle(sketch, "E7.0.10.33", {"center": v(-157.9, 228.1) * mm, "radius": 2 * mm});
            skCircle(sketch, "E7.0.10.34", {"center": v(-157.9, 244.1) * mm, "radius": 2 * mm});
            skCircle(sketch, "E7.0.10.35", {"center": v(-157.9, 260.1) * mm, "radius": 2 * mm});
            skCircle(sketch, "E7.0.10.36", {"center": v(-157.9, 276.1) * mm, "radius": 2 * mm});
            skCircle(sketch, "E7.0.10.37", {"center": v(-157.9, 292.1) * mm, "radius": 2 * mm});
            skCircle(sketch, "E7.0.11.10", {"center": v(-141.9, -139.9) * mm, "radius": 2 * mm});
            skCircle(sketch, "E7.0.11.11", {"center": v(-141.9, -123.9) * mm, "radius": 2 * mm});
            skCircle(sketch, "E7.0.11.12", {"center": v(-141.9, -107.9) * mm, "radius": 2 * mm});
            skCircle(sketch, "E7.0.11.13", {"center": v(-141.9, -91.9) * mm, "radius": 2 * mm});
            skCircle(sketch, "E7.0.11.14", {"center": v(-141.9, -75.9) * mm, "radius": 2 * mm});
            skCircle(sketch, "E7.0.11.15", {"center": v(-141.9, -59.9) * mm, "radius": 2 * mm});
            skCircle(sketch, "E7.0.11.16", {"center": v(-141.9, -43.9) * mm, "radius": 2 * mm});
            skCircle(sketch, "E7.0.11.17", {"center": v(-141.9, -27.9) * mm, "radius": 2 * mm});
            skCircle(sketch, "E7.0.11.18", {"center": v(-141.9, -11.9) * mm, "radius": 2 * mm});
            skCircle(sketch, "E7.0.11.19", {"center": v(-141.9, 4.1) * mm, "radius": 2 * mm});
            skCircle(sketch, "E7.0.11.20", {"center": v(-141.9, 20.1) * mm, "radius": 2 * mm});
            skCircle(sketch, "E7.0.11.21", {"center": v(-141.9, 36.1) * mm, "radius": 2 * mm});
            skCircle(sketch, "E7.0.11.22", {"center": v(-141.9, 52.1) * mm, "radius": 2 * mm});
            skCircle(sketch, "E7.0.11.23", {"center": v(-141.9, 68.1) * mm, "radius": 2 * mm});
            skCircle(sketch, "E7.0.11.24", {"center": v(-141.9, 84.1) * mm, "radius": 2 * mm});
            skCircle(sketch, "E7.0.11.25", {"center": v(-141.9, 100.1) * mm, "radius": 2 * mm});
            skCircle(sketch, "E7.0.11.26", {"center": v(-141.9, 116.1) * mm, "radius": 2 * mm});
            skCircle(sketch, "E7.0.11.27", {"center": v(-141.9, 132.1) * mm, "radius": 2 * mm});
            skCircle(sketch, "E7.0.11.28", {"center": v(-141.9, 148.1) * mm, "radius": 2 * mm});
            skCircle(sketch, "E7.0.11.29", {"center": v(-141.9, 164.1) * mm, "radius": 2 * mm});
            skCircle(sketch, "E7.0.11.30", {"center": v(-141.9, 180.1) * mm, "radius": 2 * mm});
            skCircle(sketch, "E7.0.11.31", {"center": v(-141.9, 196.1) * mm, "radius": 2 * mm});
            skCircle(sketch, "E7.0.11.32", {"center": v(-141.9, 212.1) * mm, "radius": 2 * mm});
            skCircle(sketch, "E7.0.11.33", {"center": v(-141.9, 228.1) * mm, "radius": 2 * mm});
            skCircle(sketch, "E7.0.11.34", {"center": v(-141.9, 244.1) * mm, "radius": 2 * mm});
            skCircle(sketch, "E7.0.11.35", {"center": v(-141.9, 260.1) * mm, "radius": 2 * mm});
            skCircle(sketch, "E7.0.11.36", {"center": v(-141.9, 276.1) * mm, "radius": 2 * mm});
            skCircle(sketch, "E7.0.11.37", {"center": v(-141.9, 292.1) * mm, "radius": 2 * mm});
            skCircle(sketch, "E7.0.12.10", {"center": v(-125.9, -139.9) * mm, "radius": 2 * mm});
            skCircle(sketch, "E7.0.12.11", {"center": v(-125.9, -123.9) * mm, "radius": 2 * mm});
            skCircle(sketch, "E7.0.12.12", {"center": v(-125.9, -107.9) * mm, "radius": 2 * mm});
            skCircle(sketch, "E7.0.12.13", {"center": v(-125.9, -91.9) * mm, "radius": 2 * mm});
            skCircle(sketch, "E7.0.12.14", {"center": v(-125.9, -75.9) * mm, "radius": 2 * mm});
            skCircle(sketch, "E7.0.12.15", {"center": v(-125.9, -59.9) * mm, "radius": 2 * mm});
            skCircle(sketch, "E7.0.12.16", {"center": v(-125.9, -43.9) * mm, "radius": 2 * mm});
            skCircle(sketch, "E7.0.12.17", {"center": v(-125.9, -27.9) * mm, "radius": 2 * mm});
            skCircle(sketch, "E7.0.12.18", {"center": v(-125.9, -11.9) * mm, "radius": 2 * mm});
            skCircle(sketch, "E7.0.12.19", {"center": v(-125.9, 4.1) * mm, "radius": 2 * mm});
            skCircle(sketch, "E7.0.12.20", {"center": v(-125.9, 20.1) * mm, "radius": 2 * mm});
            skCircle(sketch, "E7.0.12.21", {"center": v(-125.9, 36.1) * mm, "radius": 2 * mm});
            skCircle(sketch, "E7.0.12.22", {"center": v(-125.9, 52.1) * mm, "radius": 2 * mm});
            skCircle(sketch, "E7.0.12.23", {"center": v(-125.9, 68.1) * mm, "radius": 2 * mm});
            skCircle(sketch, "E7.0.12.24", {"center": v(-125.9, 84.1) * mm, "radius": 2 * mm});
            skCircle(sketch, "E7.0.12.25", {"center": v(-125.9, 100.1) * mm, "radius": 2 * mm});
            skCircle(sketch, "E7.0.12.26", {"center": v(-125.9, 116.1) * mm, "radius": 2 * mm});
            skCircle(sketch, "E7.0.12.27", {"center": v(-125.9, 132.1) * mm, "radius": 2 * mm});
            skCircle(sketch, "E7.0.12.28", {"center": v(-125.9, 148.1) * mm, "radius": 2 * mm});
            skCircle(sketch, "E7.0.12.29", {"center": v(-125.9, 164.1) * mm, "radius": 2 * mm});
            skCircle(sketch, "E7.0.12.30", {"center": v(-125.9, 180.1) * mm, "radius": 2 * mm});
            skCircle(sketch, "E7.0.12.31", {"center": v(-125.9, 196.1) * mm, "radius": 2 * mm});
            skCircle(sketch, "E7.0.12.32", {"center": v(-125.9, 212.1) * mm, "radius": 2 * mm});
            skCircle(sketch, "E7.0.12.33", {"center": v(-125.9, 228.1) * mm, "radius": 2 * mm});
            skCircle(sketch, "E7.0.12.34", {"center": v(-125.9, 244.1) * mm, "radius": 2 * mm});
            skCircle(sketch, "E7.0.12.35", {"center": v(-125.9, 260.1) * mm, "radius": 2 * mm});
            skCircle(sketch, "E7.0.12.36", {"center": v(-125.9, 276.1) * mm, "radius": 2 * mm});
            skCircle(sketch, "E7.0.12.37", {"center": v(-125.9, 292.1) * mm, "radius": 2 * mm});
            skCircle(sketch, "E7.0.13.10", {"center": v(-109.9, -139.9) * mm, "radius": 2 * mm});
            skCircle(sketch, "E7.0.13.11", {"center": v(-109.9, -123.9) * mm, "radius": 2 * mm});
            skCircle(sketch, "E7.0.13.12", {"center": v(-109.9, -107.9) * mm, "radius": 2 * mm});
            skCircle(sketch, "E7.0.13.13", {"center": v(-109.9, -91.9) * mm, "radius": 2 * mm});
            skCircle(sketch, "E7.0.13.14", {"center": v(-109.9, -75.9) * mm, "radius": 2 * mm});
            skCircle(sketch, "E7.0.13.15", {"center": v(-109.9, -59.9) * mm, "radius": 2 * mm});
            skCircle(sketch, "E7.0.13.16", {"center": v(-109.9, -43.9) * mm, "radius": 2 * mm});
            skCircle(sketch, "E7.0.13.17", {"center": v(-109.9, -27.9) * mm, "radius": 2 * mm});
            skCircle(sketch, "E7.0.13.18", {"center": v(-109.9, -11.9) * mm, "radius": 2 * mm});
            skCircle(sketch, "E7.0.13.19", {"center": v(-109.9, 4.1) * mm, "radius": 2 * mm});
            skCircle(sketch, "E7.0.13.20", {"center": v(-109.9, 20.1) * mm, "radius": 2 * mm});
            skCircle(sketch, "E7.0.13.21", {"center": v(-109.9, 36.1) * mm, "radius": 2 * mm});
            skCircle(sketch, "E7.0.13.22", {"center": v(-109.9, 52.1) * mm, "radius": 2 * mm});
            skCircle(sketch, "E7.0.13.23", {"center": v(-109.9, 68.1) * mm, "radius": 2 * mm});
            skCircle(sketch, "E7.0.13.24", {"center": v(-109.9, 84.1) * mm, "radius": 2 * mm});
            skCircle(sketch, "E7.0.13.25", {"center": v(-109.9, 100.1) * mm, "radius": 2 * mm});
            skCircle(sketch, "E7.0.13.26", {"center": v(-109.9, 116.1) * mm, "radius": 2 * mm});
            skCircle(sketch, "E7.0.13.27", {"center": v(-109.9, 132.1) * mm, "radius": 2 * mm});
            skCircle(sketch, "E7.0.13.28", {"center": v(-109.9, 148.1) * mm, "radius": 2 * mm});
            skCircle(sketch, "E7.0.13.29", {"center": v(-109.9, 164.1) * mm, "radius": 2 * mm});
            skCircle(sketch, "E7.0.13.30", {"center": v(-109.9, 180.1) * mm, "radius": 2 * mm});
            skCircle(sketch, "E7.0.13.31", {"center": v(-109.9, 196.1) * mm, "radius": 2 * mm});
            skCircle(sketch, "E7.0.13.32", {"center": v(-109.9, 212.1) * mm, "radius": 2 * mm});
            skCircle(sketch, "E7.0.13.33", {"center": v(-109.9, 228.1) * mm, "radius": 2 * mm});
            skCircle(sketch, "E7.0.13.34", {"center": v(-109.9, 244.1) * mm, "radius": 2 * mm});
            skCircle(sketch, "E7.0.13.35", {"center": v(-109.9, 260.1) * mm, "radius": 2 * mm});
            skCircle(sketch, "E7.0.13.36", {"center": v(-109.9, 276.1) * mm, "radius": 2 * mm});
            skCircle(sketch, "E7.0.13.37", {"center": v(-109.9, 292.1) * mm, "radius": 2 * mm});
            skCircle(sketch, "E7.0.14.10", {"center": v(-93.9, -139.9) * mm, "radius": 2 * mm});
            skCircle(sketch, "E7.0.14.11", {"center": v(-93.9, -123.9) * mm, "radius": 2 * mm});
            skCircle(sketch, "E7.0.14.12", {"center": v(-93.9, -107.9) * mm, "radius": 2 * mm});
            skCircle(sketch, "E7.0.14.13", {"center": v(-93.9, -91.9) * mm, "radius": 2 * mm});
            skCircle(sketch, "E7.0.14.14", {"center": v(-93.9, -75.9) * mm, "radius": 2 * mm});
            skCircle(sketch, "E7.0.14.15", {"center": v(-93.9, -59.9) * mm, "radius": 2 * mm});
            skCircle(sketch, "E7.0.14.16", {"center": v(-93.9, -43.9) * mm, "radius": 2 * mm});
            skCircle(sketch, "E7.0.14.17", {"center": v(-93.9, -27.9) * mm, "radius": 2 * mm});
            skCircle(sketch, "E7.0.14.18", {"center": v(-93.9, -11.9) * mm, "radius": 2 * mm});
            skCircle(sketch, "E7.0.14.19", {"center": v(-93.9, 4.1) * mm, "radius": 2 * mm});
            skCircle(sketch, "E7.0.14.20", {"center": v(-93.9, 20.1) * mm, "radius": 2 * mm});
            skCircle(sketch, "E7.0.14.21", {"center": v(-93.9, 36.1) * mm, "radius": 2 * mm});
            skCircle(sketch, "E7.0.14.22", {"center": v(-93.9, 52.1) * mm, "radius": 2 * mm});
            skCircle(sketch, "E7.0.14.23", {"center": v(-93.9, 68.1) * mm, "radius": 2 * mm});
            skCircle(sketch, "E7.0.14.24", {"center": v(-93.9, 84.1) * mm, "radius": 2 * mm});
            skCircle(sketch, "E7.0.14.25", {"center": v(-93.9, 100.1) * mm, "radius": 2 * mm});
            skCircle(sketch, "E7.0.14.26", {"center": v(-93.9, 116.1) * mm, "radius": 2 * mm});
            skCircle(sketch, "E7.0.14.27", {"center": v(-93.9, 132.1) * mm, "radius": 2 * mm});
            skCircle(sketch, "E7.0.14.28", {"center": v(-93.9, 148.1) * mm, "radius": 2 * mm});
            skCircle(sketch, "E7.0.14.29", {"center": v(-93.9, 164.1) * mm, "radius": 2 * mm});
            skCircle(sketch, "E7.0.14.30", {"center": v(-93.9, 180.1) * mm, "radius": 2 * mm});
            skCircle(sketch, "E7.0.14.31", {"center": v(-93.9, 196.1) * mm, "radius": 2 * mm});
            skCircle(sketch, "E7.0.14.32", {"center": v(-93.9, 212.1) * mm, "radius": 2 * mm});
            skCircle(sketch, "E7.0.14.33", {"center": v(-93.9, 228.1) * mm, "radius": 2 * mm});
            skCircle(sketch, "E7.0.14.34", {"center": v(-93.9, 244.1) * mm, "radius": 2 * mm});
            skCircle(sketch, "E7.0.14.35", {"center": v(-93.9, 260.1) * mm, "radius": 2 * mm});
            skCircle(sketch, "E7.0.14.36", {"center": v(-93.9, 276.1) * mm, "radius": 2 * mm});
            skCircle(sketch, "E7.0.14.37", {"center": v(-93.9, 292.1) * mm, "radius": 2 * mm});
            skCircle(sketch, "E7.0.15.10", {"center": v(-77.9, -139.9) * mm, "radius": 2 * mm});
            skCircle(sketch, "E7.0.15.11", {"center": v(-77.9, -123.9) * mm, "radius": 2 * mm});
            skCircle(sketch, "E7.0.15.12", {"center": v(-77.9, -107.9) * mm, "radius": 2 * mm});
            skCircle(sketch, "E7.0.15.13", {"center": v(-77.9, -91.9) * mm, "radius": 2 * mm});
            skCircle(sketch, "E7.0.15.14", {"center": v(-77.9, -75.9) * mm, "radius": 2 * mm});
            skCircle(sketch, "E7.0.15.15", {"center": v(-77.9, -59.9) * mm, "radius": 2 * mm});
            skCircle(sketch, "E7.0.15.16", {"center": v(-77.9, -43.9) * mm, "radius": 2 * mm});
            skCircle(sketch, "E7.0.15.17", {"center": v(-77.9, -27.9) * mm, "radius": 2 * mm});
            skCircle(sketch, "E7.0.15.18", {"center": v(-77.9, -11.9) * mm, "radius": 2 * mm});
            skCircle(sketch, "E7.0.15.19", {"center": v(-77.9, 4.1) * mm, "radius": 2 * mm});
            skCircle(sketch, "E7.0.15.20", {"center": v(-77.9, 20.1) * mm, "radius": 2 * mm});
            skCircle(sketch, "E7.0.15.21", {"center": v(-77.9, 36.1) * mm, "radius": 2 * mm});
            skCircle(sketch, "E7.0.15.22", {"center": v(-77.9, 52.1) * mm, "radius": 2 * mm});
            skCircle(sketch, "E7.0.15.23", {"center": v(-77.9, 68.1) * mm, "radius": 2 * mm});
            skCircle(sketch, "E7.0.15.24", {"center": v(-77.9, 84.1) * mm, "radius": 2 * mm});
            skCircle(sketch, "E7.0.15.25", {"center": v(-77.9, 100.1) * mm, "radius": 2 * mm});
            skCircle(sketch, "E7.0.15.26", {"center": v(-77.9, 116.1) * mm, "radius": 2 * mm});
            skCircle(sketch, "E7.0.15.27", {"center": v(-77.9, 132.1) * mm, "radius": 2 * mm});
            skCircle(sketch, "E7.0.15.28", {"center": v(-77.9, 148.1) * mm, "radius": 2 * mm});
            skCircle(sketch, "E7.0.15.29", {"center": v(-77.9, 164.1) * mm, "radius": 2 * mm});
            skCircle(sketch, "E7.0.15.30", {"center": v(-77.9, 180.1) * mm, "radius": 2 * mm});
            skCircle(sketch, "E7.0.15.31", {"center": v(-77.9, 196.1) * mm, "radius": 2 * mm});
            skCircle(sketch, "E7.0.15.32", {"center": v(-77.9, 212.1) * mm, "radius": 2 * mm});
            skCircle(sketch, "E7.0.15.33", {"center": v(-77.9, 228.1) * mm, "radius": 2 * mm});
            skCircle(sketch, "E7.0.15.34", {"center": v(-77.9, 244.1) * mm, "radius": 2 * mm});
            skCircle(sketch, "E7.0.15.35", {"center": v(-77.9, 260.1) * mm, "radius": 2 * mm});
            skCircle(sketch, "E7.0.15.36", {"center": v(-77.9, 276.1) * mm, "radius": 2 * mm});
            skCircle(sketch, "E7.0.15.37", {"center": v(-77.9, 292.1) * mm, "radius": 2 * mm});
            skCircle(sketch, "E7.0.16.10", {"center": v(-61.9, -139.9) * mm, "radius": 2 * mm});
            skCircle(sketch, "E7.0.16.11", {"center": v(-61.9, -123.9) * mm, "radius": 2 * mm});
            skCircle(sketch, "E7.0.16.12", {"center": v(-61.9, -107.9) * mm, "radius": 2 * mm});
            skCircle(sketch, "E7.0.16.13", {"center": v(-61.9, -91.9) * mm, "radius": 2 * mm});
            skCircle(sketch, "E7.0.16.14", {"center": v(-61.9, -75.9) * mm, "radius": 2 * mm});
            skCircle(sketch, "E7.0.16.15", {"center": v(-61.9, -59.9) * mm, "radius": 2 * mm});
            skCircle(sketch, "E7.0.16.16", {"center": v(-61.9, -43.9) * mm, "radius": 2 * mm});
            skCircle(sketch, "E7.0.16.17", {"center": v(-61.9, -27.9) * mm, "radius": 2 * mm});
            skCircle(sketch, "E7.0.16.18", {"center": v(-61.9, -11.9) * mm, "radius": 2 * mm});
            skCircle(sketch, "E7.0.16.19", {"center": v(-61.9, 4.1) * mm, "radius": 2 * mm});
            skCircle(sketch, "E7.0.16.20", {"center": v(-61.9, 20.1) * mm, "radius": 2 * mm});
            skCircle(sketch, "E7.0.16.21", {"center": v(-61.9, 36.1) * mm, "radius": 2 * mm});
            skCircle(sketch, "E7.0.16.22", {"center": v(-61.9, 52.1) * mm, "radius": 2 * mm});
            skCircle(sketch, "E7.0.16.23", {"center": v(-61.9, 68.1) * mm, "radius": 2 * mm});
            skCircle(sketch, "E7.0.16.24", {"center": v(-61.9, 84.1) * mm, "radius": 2 * mm});
            skCircle(sketch, "E7.0.16.25", {"center": v(-61.9, 100.1) * mm, "radius": 2 * mm});
            skCircle(sketch, "E7.0.16.26", {"center": v(-61.9, 116.1) * mm, "radius": 2 * mm});
            skCircle(sketch, "E7.0.16.27", {"center": v(-61.9, 132.1) * mm, "radius": 2 * mm});
            skCircle(sketch, "E7.0.16.28", {"center": v(-61.9, 148.1) * mm, "radius": 2 * mm});
            skCircle(sketch, "E7.0.16.29", {"center": v(-61.9, 164.1) * mm, "radius": 2 * mm});
            skCircle(sketch, "E7.0.16.30", {"center": v(-61.9, 180.1) * mm, "radius": 2 * mm});
            skCircle(sketch, "E7.0.16.31", {"center": v(-61.9, 196.1) * mm, "radius": 2 * mm});
            skCircle(sketch, "E7.0.16.32", {"center": v(-61.9, 212.1) * mm, "radius": 2 * mm});
            skCircle(sketch, "E7.0.16.33", {"center": v(-61.9, 228.1) * mm, "radius": 2 * mm});
            skCircle(sketch, "E7.0.16.34", {"center": v(-61.9, 244.1) * mm, "radius": 2 * mm});
            skCircle(sketch, "E7.0.16.35", {"center": v(-61.9, 260.1) * mm, "radius": 2 * mm});
            skCircle(sketch, "E7.0.16.36", {"center": v(-61.9, 276.1) * mm, "radius": 2 * mm});
            skCircle(sketch, "E7.0.16.37", {"center": v(-61.9, 292.1) * mm, "radius": 2 * mm});
            skCircle(sketch, "E7.0.17.10", {"center": v(-45.9, -139.9) * mm, "radius": 2 * mm});
            skCircle(sketch, "E7.0.17.11", {"center": v(-45.9, -123.9) * mm, "radius": 2 * mm});
            skCircle(sketch, "E7.0.17.12", {"center": v(-45.9, -107.9) * mm, "radius": 2 * mm});
            skCircle(sketch, "E7.0.17.13", {"center": v(-45.9, -91.9) * mm, "radius": 2 * mm});
            skCircle(sketch, "E7.0.17.14", {"center": v(-45.9, -75.9) * mm, "radius": 2 * mm});
            skCircle(sketch, "E7.0.17.15", {"center": v(-45.9, -59.9) * mm, "radius": 2 * mm});
            skCircle(sketch, "E7.0.17.16", {"center": v(-45.9, -43.9) * mm, "radius": 2 * mm});
            skCircle(sketch, "E7.0.17.17", {"center": v(-45.9, -27.9) * mm, "radius": 2 * mm});
            skCircle(sketch, "E7.0.17.18", {"center": v(-45.9, -11.9) * mm, "radius": 2 * mm});
            skCircle(sketch, "E7.0.17.19", {"center": v(-45.9, 4.1) * mm, "radius": 2 * mm});
            skCircle(sketch, "E7.0.17.20", {"center": v(-45.9, 20.1) * mm, "radius": 2 * mm});
            skCircle(sketch, "E7.0.17.21", {"center": v(-45.9, 36.1) * mm, "radius": 2 * mm});
            skCircle(sketch, "E7.0.17.22", {"center": v(-45.9, 52.1) * mm, "radius": 2 * mm});
            skCircle(sketch, "E7.0.17.23", {"center": v(-45.9, 68.1) * mm, "radius": 2 * mm});
            skCircle(sketch, "E7.0.17.24", {"center": v(-45.9, 84.1) * mm, "radius": 2 * mm});
            skCircle(sketch, "E7.0.17.25", {"center": v(-45.9, 100.1) * mm, "radius": 2 * mm});
            skCircle(sketch, "E7.0.17.26", {"center": v(-45.9, 116.1) * mm, "radius": 2 * mm});
            skCircle(sketch, "E7.0.17.27", {"center": v(-45.9, 132.1) * mm, "radius": 2 * mm});
            skCircle(sketch, "E7.0.17.28", {"center": v(-45.9, 148.1) * mm, "radius": 2 * mm});
            skCircle(sketch, "E7.0.17.29", {"center": v(-45.9, 164.1) * mm, "radius": 2 * mm});
            skCircle(sketch, "E7.0.17.30", {"center": v(-45.9, 180.1) * mm, "radius": 2 * mm});
            skCircle(sketch, "E7.0.17.31", {"center": v(-45.9, 196.1) * mm, "radius": 2 * mm});
            skCircle(sketch, "E7.0.17.32", {"center": v(-45.9, 212.1) * mm, "radius": 2 * mm});
            skCircle(sketch, "E7.0.17.33", {"center": v(-45.9, 228.1) * mm, "radius": 2 * mm});
            skCircle(sketch, "E7.0.17.34", {"center": v(-45.9, 244.1) * mm, "radius": 2 * mm});
            skCircle(sketch, "E7.0.17.35", {"center": v(-45.9, 260.1) * mm, "radius": 2 * mm});
            skCircle(sketch, "E7.0.17.36", {"center": v(-45.9, 276.1) * mm, "radius": 2 * mm});
            skCircle(sketch, "E7.0.17.37", {"center": v(-45.9, 292.1) * mm, "radius": 2 * mm});
            skCircle(sketch, "E7.0.18.10", {"center": v(-29.9, -139.9) * mm, "radius": 2 * mm});
            skCircle(sketch, "E7.0.18.11", {"center": v(-29.9, -123.9) * mm, "radius": 2 * mm});
            skCircle(sketch, "E7.0.18.12", {"center": v(-29.9, -107.9) * mm, "radius": 2 * mm});
            skCircle(sketch, "E7.0.18.13", {"center": v(-29.9, -91.9) * mm, "radius": 2 * mm});
            skCircle(sketch, "E7.0.18.14", {"center": v(-29.9, -75.9) * mm, "radius": 2 * mm});
            skCircle(sketch, "E7.0.18.15", {"center": v(-29.9, -59.9) * mm, "radius": 2 * mm});
            skCircle(sketch, "E7.0.18.16", {"center": v(-29.9, -43.9) * mm, "radius": 2 * mm});
            skCircle(sketch, "E7.0.18.17", {"center": v(-29.9, -27.9) * mm, "radius": 2 * mm});
            skCircle(sketch, "E7.0.18.18", {"center": v(-29.9, -11.9) * mm, "radius": 2 * mm});
            skCircle(sketch, "E7.0.18.19", {"center": v(-29.9, 4.1) * mm, "radius": 2 * mm});
            skCircle(sketch, "E7.0.18.20", {"center": v(-29.9, 20.1) * mm, "radius": 2 * mm});
            skCircle(sketch, "E7.0.18.21", {"center": v(-29.9, 36.1) * mm, "radius": 2 * mm});
            skCircle(sketch, "E7.0.18.22", {"center": v(-29.9, 52.1) * mm, "radius": 2 * mm});
            skCircle(sketch, "E7.0.18.23", {"center": v(-29.9, 68.1) * mm, "radius": 2 * mm});
            skCircle(sketch, "E7.0.18.24", {"center": v(-29.9, 84.1) * mm, "radius": 2 * mm});
            skCircle(sketch, "E7.0.18.25", {"center": v(-29.9, 100.1) * mm, "radius": 2 * mm});
            skCircle(sketch, "E7.0.18.26", {"center": v(-29.9, 116.1) * mm, "radius": 2 * mm});
            skCircle(sketch, "E7.0.18.27", {"center": v(-29.9, 132.1) * mm, "radius": 2 * mm});
            skCircle(sketch, "E7.0.18.28", {"center": v(-29.9, 148.1) * mm, "radius": 2 * mm});
            skCircle(sketch, "E7.0.18.29", {"center": v(-29.9, 164.1) * mm, "radius": 2 * mm});
            skCircle(sketch, "E7.0.18.30", {"center": v(-29.9, 180.1) * mm, "radius": 2 * mm});
            skCircle(sketch, "E7.0.18.31", {"center": v(-29.9, 196.1) * mm, "radius": 2 * mm});
            skCircle(sketch, "E7.0.18.32", {"center": v(-29.9, 212.1) * mm, "radius": 2 * mm});
            skCircle(sketch, "E7.0.18.33", {"center": v(-29.9, 228.1) * mm, "radius": 2 * mm});
            skCircle(sketch, "E7.0.18.34", {"center": v(-29.9, 244.1) * mm, "radius": 2 * mm});
            skCircle(sketch, "E7.0.18.35", {"center": v(-29.9, 260.1) * mm, "radius": 2 * mm});
            skCircle(sketch, "E7.0.18.36", {"center": v(-29.9, 276.1) * mm, "radius": 2 * mm});
            skCircle(sketch, "E7.0.18.37", {"center": v(-29.9, 292.1) * mm, "radius": 2 * mm});
            skCircle(sketch, "E7.0.19.10", {"center": v(-13.9, -139.9) * mm, "radius": 2 * mm});
            skCircle(sketch, "E7.0.19.11", {"center": v(-13.9, -123.9) * mm, "radius": 2 * mm});
            skCircle(sketch, "E7.0.19.12", {"center": v(-13.9, -107.9) * mm, "radius": 2 * mm});
            skCircle(sketch, "E7.0.19.13", {"center": v(-13.9, -91.9) * mm, "radius": 2 * mm});
            skCircle(sketch, "E7.0.19.14", {"center": v(-13.9, -75.9) * mm, "radius": 2 * mm});
            skCircle(sketch, "E7.0.19.15", {"center": v(-13.9, -59.9) * mm, "radius": 2 * mm});
            skCircle(sketch, "E7.0.19.16", {"center": v(-13.9, -43.9) * mm, "radius": 2 * mm});
            skCircle(sketch, "E7.0.19.17", {"center": v(-13.9, -27.9) * mm, "radius": 2 * mm});
            skCircle(sketch, "E7.0.19.18", {"center": v(-13.9, -11.9) * mm, "radius": 2 * mm});
            skCircle(sketch, "E7.0.19.19", {"center": v(-13.9, 4.1) * mm, "radius": 2 * mm});
            skCircle(sketch, "E7.0.19.20", {"center": v(-13.9, 20.1) * mm, "radius": 2 * mm});
            skCircle(sketch, "E7.0.19.21", {"center": v(-13.9, 36.1) * mm, "radius": 2 * mm});
            skCircle(sketch, "E7.0.19.22", {"center": v(-13.9, 52.1) * mm, "radius": 2 * mm});
            skCircle(sketch, "E7.0.19.23", {"center": v(-13.9, 68.1) * mm, "radius": 2 * mm});
            skCircle(sketch, "E7.0.19.24", {"center": v(-13.9, 84.1) * mm, "radius": 2 * mm});
            skCircle(sketch, "E7.0.19.25", {"center": v(-13.9, 100.1) * mm, "radius": 2 * mm});
            skCircle(sketch, "E7.0.19.26", {"center": v(-13.9, 116.1) * mm, "radius": 2 * mm});
            skCircle(sketch, "E7.0.19.27", {"center": v(-13.9, 132.1) * mm, "radius": 2 * mm});
            skCircle(sketch, "E7.0.19.28", {"center": v(-13.9, 148.1) * mm, "radius": 2 * mm});
            skCircle(sketch, "E7.0.19.29", {"center": v(-13.9, 164.1) * mm, "radius": 2 * mm});
            skCircle(sketch, "E7.0.19.30", {"center": v(-13.9, 180.1) * mm, "radius": 2 * mm});
            skCircle(sketch, "E7.0.19.31", {"center": v(-13.9, 196.1) * mm, "radius": 2 * mm});
            skCircle(sketch, "E7.0.19.32", {"center": v(-13.9, 212.1) * mm, "radius": 2 * mm});
            skCircle(sketch, "E7.0.19.33", {"center": v(-13.9, 228.1) * mm, "radius": 2 * mm});
            skCircle(sketch, "E7.0.19.34", {"center": v(-13.9, 244.1) * mm, "radius": 2 * mm});
            skCircle(sketch, "E7.0.19.35", {"center": v(-13.9, 260.1) * mm, "radius": 2 * mm});
            skCircle(sketch, "E7.0.19.36", {"center": v(-13.9, 276.1) * mm, "radius": 2 * mm});
            skCircle(sketch, "E7.0.19.37", {"center": v(-13.9, 292.1) * mm, "radius": 2 * mm});
            skCircle(sketch, "E7.0.20.10", {"center": v(2.1, -139.9) * mm, "radius": 2 * mm});
            skCircle(sketch, "E7.0.20.11", {"center": v(2.1, -123.9) * mm, "radius": 2 * mm});
            skCircle(sketch, "E7.0.20.12", {"center": v(2.1, -107.9) * mm, "radius": 2 * mm});
            skCircle(sketch, "E7.0.20.13", {"center": v(2.1, -91.9) * mm, "radius": 2 * mm});
            skCircle(sketch, "E7.0.20.14", {"center": v(2.1, -75.9) * mm, "radius": 2 * mm});
            skCircle(sketch, "E7.0.20.15", {"center": v(2.1, -59.9) * mm, "radius": 2 * mm});
            skCircle(sketch, "E7.0.20.16", {"center": v(2.1, -43.9) * mm, "radius": 2 * mm});
            skCircle(sketch, "E7.0.20.17", {"center": v(2.1, -27.9) * mm, "radius": 2 * mm});
            skCircle(sketch, "E7.0.20.18", {"center": v(2.1, -11.9) * mm, "radius": 2 * mm});
            skCircle(sketch, "E7.0.20.19", {"center": v(2.1, 4.1) * mm, "radius": 2 * mm});
            skCircle(sketch, "E7.0.20.20", {"center": v(2.1, 20.1) * mm, "radius": 2 * mm});
            skCircle(sketch, "E7.0.20.21", {"center": v(2.1, 36.1) * mm, "radius": 2 * mm});
            skCircle(sketch, "E7.0.20.22", {"center": v(2.1, 52.1) * mm, "radius": 2 * mm});
            skCircle(sketch, "E7.0.20.23", {"center": v(2.1, 68.1) * mm, "radius": 2 * mm});
            skCircle(sketch, "E7.0.20.24", {"center": v(2.1, 84.1) * mm, "radius": 2 * mm});
            skCircle(sketch, "E7.0.20.25", {"center": v(2.1, 100.1) * mm, "radius": 2 * mm});
            skCircle(sketch, "E7.0.20.26", {"center": v(2.1, 116.1) * mm, "radius": 2 * mm});
            skCircle(sketch, "E7.0.20.27", {"center": v(2.1, 132.1) * mm, "radius": 2 * mm});
            skCircle(sketch, "E7.0.20.28", {"center": v(2.1, 148.1) * mm, "radius": 2 * mm});
            skCircle(sketch, "E7.0.20.29", {"center": v(2.1, 164.1) * mm, "radius": 2 * mm});
            skCircle(sketch, "E7.0.20.30", {"center": v(2.1, 180.1) * mm, "radius": 2 * mm});
            skCircle(sketch, "E7.0.20.31", {"center": v(2.1, 196.1) * mm, "radius": 2 * mm});
            skCircle(sketch, "E7.0.20.32", {"center": v(2.1, 212.1) * mm, "radius": 2 * mm});
            skCircle(sketch, "E7.0.20.33", {"center": v(2.1, 228.1) * mm, "radius": 2 * mm});
            skCircle(sketch, "E7.0.20.34", {"center": v(2.1, 244.1) * mm, "radius": 2 * mm});
            skCircle(sketch, "E7.0.20.35", {"center": v(2.1, 260.1) * mm, "radius": 2 * mm});
            skCircle(sketch, "E7.0.20.36", {"center": v(2.1, 276.1) * mm, "radius": 2 * mm});
            skCircle(sketch, "E7.0.20.37", {"center": v(2.1, 292.1) * mm, "radius": 2 * mm});
            skCircle(sketch, "E7.0.21.10", {"center": v(18.1, -139.9) * mm, "radius": 2 * mm});
            skCircle(sketch, "E7.0.21.11", {"center": v(18.1, -123.9) * mm, "radius": 2 * mm});
            skCircle(sketch, "E7.0.21.12", {"center": v(18.1, -107.9) * mm, "radius": 2 * mm});
            skCircle(sketch, "E7.0.21.13", {"center": v(18.1, -91.9) * mm, "radius": 2 * mm});
            skCircle(sketch, "E7.0.21.14", {"center": v(18.1, -75.9) * mm, "radius": 2 * mm});
            skCircle(sketch, "E7.0.21.15", {"center": v(18.1, -59.9) * mm, "radius": 2 * mm});
            skCircle(sketch, "E7.0.21.16", {"center": v(18.1, -43.9) * mm, "radius": 2 * mm});
            skCircle(sketch, "E7.0.21.17", {"center": v(18.1, -27.9) * mm, "radius": 2 * mm});
            skCircle(sketch, "E7.0.21.18", {"center": v(18.1, -11.9) * mm, "radius": 2 * mm});
            skCircle(sketch, "E7.0.21.19", {"center": v(18.1, 4.1) * mm, "radius": 2 * mm});
            skCircle(sketch, "E7.0.21.20", {"center": v(18.1, 20.1) * mm, "radius": 2 * mm});
            skCircle(sketch, "E7.0.21.21", {"center": v(18.1, 36.1) * mm, "radius": 2 * mm});
            skCircle(sketch, "E7.0.21.22", {"center": v(18.1, 52.1) * mm, "radius": 2 * mm});
            skCircle(sketch, "E7.0.21.23", {"center": v(18.1, 68.1) * mm, "radius": 2 * mm});
            skCircle(sketch, "E7.0.21.24", {"center": v(18.1, 84.1) * mm, "radius": 2 * mm});
            skCircle(sketch, "E7.0.21.25", {"center": v(18.1, 100.1) * mm, "radius": 2 * mm});
            skCircle(sketch, "E7.0.21.26", {"center": v(18.1, 116.1) * mm, "radius": 2 * mm});
            skCircle(sketch, "E7.0.21.27", {"center": v(18.1, 132.1) * mm, "radius": 2 * mm});
            skCircle(sketch, "E7.0.21.28", {"center": v(18.1, 148.1) * mm, "radius": 2 * mm});
            skCircle(sketch, "E7.0.21.29", {"center": v(18.1, 164.1) * mm, "radius": 2 * mm});
            skCircle(sketch, "E7.0.21.30", {"center": v(18.1, 180.1) * mm, "radius": 2 * mm});
            skCircle(sketch, "E7.0.21.31", {"center": v(18.1, 196.1) * mm, "radius": 2 * mm});
            skCircle(sketch, "E7.0.21.32", {"center": v(18.1, 212.1) * mm, "radius": 2 * mm});
            skCircle(sketch, "E7.0.21.33", {"center": v(18.1, 228.1) * mm, "radius": 2 * mm});
            skCircle(sketch, "E7.0.21.34", {"center": v(18.1, 244.1) * mm, "radius": 2 * mm});
            skCircle(sketch, "E7.0.21.35", {"center": v(18.1, 260.1) * mm, "radius": 2 * mm});
            skCircle(sketch, "E7.0.21.36", {"center": v(18.1, 276.1) * mm, "radius": 2 * mm});
            skCircle(sketch, "E7.0.21.37", {"center": v(18.1, 292.1) * mm, "radius": 2 * mm});
            skCircle(sketch, "E7.0.22.10", {"center": v(34.1, -139.9) * mm, "radius": 2 * mm});
            skCircle(sketch, "E7.0.22.11", {"center": v(34.1, -123.9) * mm, "radius": 2 * mm});
            skCircle(sketch, "E7.0.22.12", {"center": v(34.1, -107.9) * mm, "radius": 2 * mm});
            skCircle(sketch, "E7.0.22.13", {"center": v(34.1, -91.9) * mm, "radius": 2 * mm});
            skCircle(sketch, "E7.0.22.14", {"center": v(34.1, -75.9) * mm, "radius": 2 * mm});
            skCircle(sketch, "E7.0.22.15", {"center": v(34.1, -59.9) * mm, "radius": 2 * mm});
            skCircle(sketch, "E7.0.22.16", {"center": v(34.1, -43.9) * mm, "radius": 2 * mm});
            skCircle(sketch, "E7.0.22.17", {"center": v(34.1, -27.9) * mm, "radius": 2 * mm});
            skCircle(sketch, "E7.0.22.18", {"center": v(34.1, -11.9) * mm, "radius": 2 * mm});
            skCircle(sketch, "E7.0.22.19", {"center": v(34.1, 4.1) * mm, "radius": 2 * mm});
            skCircle(sketch, "E7.0.22.20", {"center": v(34.1, 20.1) * mm, "radius": 2 * mm});
            skCircle(sketch, "E7.0.22.21", {"center": v(34.1, 36.1) * mm, "radius": 2 * mm});
            skCircle(sketch, "E7.0.22.22", {"center": v(34.1, 52.1) * mm, "radius": 2 * mm});
            skCircle(sketch, "E7.0.22.23", {"center": v(34.1, 68.1) * mm, "radius": 2 * mm});
            skCircle(sketch, "E7.0.22.24", {"center": v(34.1, 84.1) * mm, "radius": 2 * mm});
            skCircle(sketch, "E7.0.22.25", {"center": v(34.1, 100.1) * mm, "radius": 2 * mm});
            skCircle(sketch, "E7.0.22.26", {"center": v(34.1, 116.1) * mm, "radius": 2 * mm});
            skCircle(sketch, "E7.0.22.27", {"center": v(34.1, 132.1) * mm, "radius": 2 * mm});
            skCircle(sketch, "E7.0.22.28", {"center": v(34.1, 148.1) * mm, "radius": 2 * mm});
            skCircle(sketch, "E7.0.22.29", {"center": v(34.1, 164.1) * mm, "radius": 2 * mm});
            skCircle(sketch, "E7.0.22.30", {"center": v(34.1, 180.1) * mm, "radius": 2 * mm});
            skCircle(sketch, "E7.0.22.31", {"center": v(34.1, 196.1) * mm, "radius": 2 * mm});
            skCircle(sketch, "E7.0.22.32", {"center": v(34.1, 212.1) * mm, "radius": 2 * mm});
            skCircle(sketch, "E7.0.22.33", {"center": v(34.1, 228.1) * mm, "radius": 2 * mm});
            skCircle(sketch, "E7.0.22.34", {"center": v(34.1, 244.1) * mm, "radius": 2 * mm});
            skCircle(sketch, "E7.0.22.35", {"center": v(34.1, 260.1) * mm, "radius": 2 * mm});
            skCircle(sketch, "E7.0.22.36", {"center": v(34.1, 276.1) * mm, "radius": 2 * mm});
            skCircle(sketch, "E7.0.22.37", {"center": v(34.1, 292.1) * mm, "radius": 2 * mm});
            skCircle(sketch, "E7.0.23.10", {"center": v(50.1, -139.9) * mm, "radius": 2 * mm});
            skCircle(sketch, "E7.0.23.11", {"center": v(50.1, -123.9) * mm, "radius": 2 * mm});
            skCircle(sketch, "E7.0.23.12", {"center": v(50.1, -107.9) * mm, "radius": 2 * mm});
            skCircle(sketch, "E7.0.23.13", {"center": v(50.1, -91.9) * mm, "radius": 2 * mm});
            skCircle(sketch, "E7.0.23.14", {"center": v(50.1, -75.9) * mm, "radius": 2 * mm});
            skCircle(sketch, "E7.0.23.15", {"center": v(50.1, -59.9) * mm, "radius": 2 * mm});
            skCircle(sketch, "E7.0.23.16", {"center": v(50.1, -43.9) * mm, "radius": 2 * mm});
            skCircle(sketch, "E7.0.23.17", {"center": v(50.1, -27.9) * mm, "radius": 2 * mm});
            skCircle(sketch, "E7.0.23.18", {"center": v(50.1, -11.9) * mm, "radius": 2 * mm});
            skCircle(sketch, "E7.0.23.19", {"center": v(50.1, 4.1) * mm, "radius": 2 * mm});
            skCircle(sketch, "E7.0.23.20", {"center": v(50.1, 20.1) * mm, "radius": 2 * mm});
            skCircle(sketch, "E7.0.23.21", {"center": v(50.1, 36.1) * mm, "radius": 2 * mm});
            skCircle(sketch, "E7.0.23.22", {"center": v(50.1, 52.1) * mm, "radius": 2 * mm});
            skCircle(sketch, "E7.0.23.23", {"center": v(50.1, 68.1) * mm, "radius": 2 * mm});
            skCircle(sketch, "E7.0.23.24", {"center": v(50.1, 84.1) * mm, "radius": 2 * mm});
            skCircle(sketch, "E7.0.23.25", {"center": v(50.1, 100.1) * mm, "radius": 2 * mm});
            skCircle(sketch, "E7.0.23.26", {"center": v(50.1, 116.1) * mm, "radius": 2 * mm});
            skCircle(sketch, "E7.0.23.27", {"center": v(50.1, 132.1) * mm, "radius": 2 * mm});
            skCircle(sketch, "E7.0.23.28", {"center": v(50.1, 148.1) * mm, "radius": 2 * mm});
            skCircle(sketch, "E7.0.23.29", {"center": v(50.1, 164.1) * mm, "radius": 2 * mm});
            skCircle(sketch, "E7.0.23.30", {"center": v(50.1, 180.1) * mm, "radius": 2 * mm});
            skCircle(sketch, "E7.0.23.31", {"center": v(50.1, 196.1) * mm, "radius": 2 * mm});
            skCircle(sketch, "E7.0.23.32", {"center": v(50.1, 212.1) * mm, "radius": 2 * mm});
            skCircle(sketch, "E7.0.23.33", {"center": v(50.1, 228.1) * mm, "radius": 2 * mm});
            skCircle(sketch, "E7.0.23.34", {"center": v(50.1, 244.1) * mm, "radius": 2 * mm});
            skCircle(sketch, "E7.0.23.35", {"center": v(50.1, 260.1) * mm, "radius": 2 * mm});
            skCircle(sketch, "E7.0.23.36", {"center": v(50.1, 276.1) * mm, "radius": 2 * mm});
            skCircle(sketch, "E7.0.23.37", {"center": v(50.1, 292.1) * mm, "radius": 2 * mm});
            skCircle(sketch, "E7.0.24.10", {"center": v(66.1, -139.9) * mm, "radius": 2 * mm});
            skCircle(sketch, "E7.0.24.11", {"center": v(66.1, -123.9) * mm, "radius": 2 * mm});
            skCircle(sketch, "E7.0.24.12", {"center": v(66.1, -107.9) * mm, "radius": 2 * mm});
            skCircle(sketch, "E7.0.24.13", {"center": v(66.1, -91.9) * mm, "radius": 2 * mm});
            skCircle(sketch, "E7.0.24.14", {"center": v(66.1, -75.9) * mm, "radius": 2 * mm});
            skCircle(sketch, "E7.0.24.15", {"center": v(66.1, -59.9) * mm, "radius": 2 * mm});
            skCircle(sketch, "E7.0.24.16", {"center": v(66.1, -43.9) * mm, "radius": 2 * mm});
            skCircle(sketch, "E7.0.24.17", {"center": v(66.1, -27.9) * mm, "radius": 2 * mm});
            skCircle(sketch, "E7.0.24.18", {"center": v(66.1, -11.9) * mm, "radius": 2 * mm});
            skCircle(sketch, "E7.0.24.19", {"center": v(66.1, 4.1) * mm, "radius": 2 * mm});
            skCircle(sketch, "E7.0.24.20", {"center": v(66.1, 20.1) * mm, "radius": 2 * mm});
            skCircle(sketch, "E7.0.24.21", {"center": v(66.1, 36.1) * mm, "radius": 2 * mm});
            skCircle(sketch, "E7.0.24.22", {"center": v(66.1, 52.1) * mm, "radius": 2 * mm});
            skCircle(sketch, "E7.0.24.23", {"center": v(66.1, 68.1) * mm, "radius": 2 * mm});
            skCircle(sketch, "E7.0.24.24", {"center": v(66.1, 84.1) * mm, "radius": 2 * mm});
            skCircle(sketch, "E7.0.24.25", {"center": v(66.1, 100.1) * mm, "radius": 2 * mm});
            skCircle(sketch, "E7.0.24.26", {"center": v(66.1, 116.1) * mm, "radius": 2 * mm});
            skCircle(sketch, "E7.0.24.27", {"center": v(66.1, 132.1) * mm, "radius": 2 * mm});
            skCircle(sketch, "E7.0.24.28", {"center": v(66.1, 148.1) * mm, "radius": 2 * mm});
            skCircle(sketch, "E7.0.24.29", {"center": v(66.1, 164.1) * mm, "radius": 2 * mm});
            skCircle(sketch, "E7.0.24.30", {"center": v(66.1, 180.1) * mm, "radius": 2 * mm});
            skCircle(sketch, "E7.0.24.31", {"center": v(66.1, 196.1) * mm, "radius": 2 * mm});
            skCircle(sketch, "E7.0.24.32", {"center": v(66.1, 212.1) * mm, "radius": 2 * mm});
            skCircle(sketch, "E7.0.24.33", {"center": v(66.1, 228.1) * mm, "radius": 2 * mm});
            skCircle(sketch, "E7.0.24.34", {"center": v(66.1, 244.1) * mm, "radius": 2 * mm});
            skCircle(sketch, "E7.0.24.35", {"center": v(66.1, 260.1) * mm, "radius": 2 * mm});
            skCircle(sketch, "E7.0.24.36", {"center": v(66.1, 276.1) * mm, "radius": 2 * mm});
            skCircle(sketch, "E7.0.24.37", {"center": v(66.1, 292.1) * mm, "radius": 2 * mm});
            skCircle(sketch, "E7.0.25.10", {"center": v(82.1, -139.9) * mm, "radius": 2 * mm});
            skCircle(sketch, "E7.0.25.11", {"center": v(82.1, -123.9) * mm, "radius": 2 * mm});
            skCircle(sketch, "E7.0.25.12", {"center": v(82.1, -107.9) * mm, "radius": 2 * mm});
            skCircle(sketch, "E7.0.25.13", {"center": v(82.1, -91.9) * mm, "radius": 2 * mm});
            skCircle(sketch, "E7.0.25.14", {"center": v(82.1, -75.9) * mm, "radius": 2 * mm});
            skCircle(sketch, "E7.0.25.15", {"center": v(82.1, -59.9) * mm, "radius": 2 * mm});
            skCircle(sketch, "E7.0.25.16", {"center": v(82.1, -43.9) * mm, "radius": 2 * mm});
            skCircle(sketch, "E7.0.25.17", {"center": v(82.1, -27.9) * mm, "radius": 2 * mm});
            skCircle(sketch, "E7.0.25.18", {"center": v(82.1, -11.9) * mm, "radius": 2 * mm});
            skCircle(sketch, "E7.0.25.19", {"center": v(82.1, 4.1) * mm, "radius": 2 * mm});
            skCircle(sketch, "E7.0.25.20", {"center": v(82.1, 20.1) * mm, "radius": 2 * mm});
            skCircle(sketch, "E7.0.25.21", {"center": v(82.1, 36.1) * mm, "radius": 2 * mm});
            skCircle(sketch, "E7.0.25.22", {"center": v(82.1, 52.1) * mm, "radius": 2 * mm});
            skCircle(sketch, "E7.0.25.23", {"center": v(82.1, 68.1) * mm, "radius": 2 * mm});
            skCircle(sketch, "E7.0.25.24", {"center": v(82.1, 84.1) * mm, "radius": 2 * mm});
            skCircle(sketch, "E7.0.25.25", {"center": v(82.1, 100.1) * mm, "radius": 2 * mm});
            skCircle(sketch, "E7.0.25.26", {"center": v(82.1, 116.1) * mm, "radius": 2 * mm});
            skCircle(sketch, "E7.0.25.27", {"center": v(82.1, 132.1) * mm, "radius": 2 * mm});
            skCircle(sketch, "E7.0.25.28", {"center": v(82.1, 148.1) * mm, "radius": 2 * mm});
            skCircle(sketch, "E7.0.25.29", {"center": v(82.1, 164.1) * mm, "radius": 2 * mm});
            skCircle(sketch, "E7.0.25.30", {"center": v(82.1, 180.1) * mm, "radius": 2 * mm});
            skCircle(sketch, "E7.0.25.31", {"center": v(82.1, 196.1) * mm, "radius": 2 * mm});
            skCircle(sketch, "E7.0.25.32", {"center": v(82.1, 212.1) * mm, "radius": 2 * mm});
            skCircle(sketch, "E7.0.25.33", {"center": v(82.1, 228.1) * mm, "radius": 2 * mm});
            skCircle(sketch, "E7.0.25.34", {"center": v(82.1, 244.1) * mm, "radius": 2 * mm});
            skCircle(sketch, "E7.0.25.35", {"center": v(82.1, 260.1) * mm, "radius": 2 * mm});
            skCircle(sketch, "E7.0.25.36", {"center": v(82.1, 276.1) * mm, "radius": 2 * mm});
            skCircle(sketch, "E7.0.25.37", {"center": v(82.1, 292.1) * mm, "radius": 2 * mm});
            skCircle(sketch, "E7.0.26.10", {"center": v(98.1, -139.9) * mm, "radius": 2 * mm});
            skCircle(sketch, "E7.0.26.11", {"center": v(98.1, -123.9) * mm, "radius": 2 * mm});
            skCircle(sketch, "E7.0.26.12", {"center": v(98.1, -107.9) * mm, "radius": 2 * mm});
            skCircle(sketch, "E7.0.26.13", {"center": v(98.1, -91.9) * mm, "radius": 2 * mm});
            skCircle(sketch, "E7.0.26.14", {"center": v(98.1, -75.9) * mm, "radius": 2 * mm});
            skCircle(sketch, "E7.0.26.15", {"center": v(98.1, -59.9) * mm, "radius": 2 * mm});
            skCircle(sketch, "E7.0.26.16", {"center": v(98.1, -43.9) * mm, "radius": 2 * mm});
            skCircle(sketch, "E7.0.26.17", {"center": v(98.1, -27.9) * mm, "radius": 2 * mm});
            skCircle(sketch, "E7.0.26.18", {"center": v(98.1, -11.9) * mm, "radius": 2 * mm});
            skCircle(sketch, "E7.0.26.19", {"center": v(98.1, 4.1) * mm, "radius": 2 * mm});
            skCircle(sketch, "E7.0.26.20", {"center": v(98.1, 20.1) * mm, "radius": 2 * mm});
            skCircle(sketch, "E7.0.26.21", {"center": v(98.1, 36.1) * mm, "radius": 2 * mm});
            skCircle(sketch, "E7.0.26.22", {"center": v(98.1, 52.1) * mm, "radius": 2 * mm});
            skCircle(sketch, "E7.0.26.23", {"center": v(98.1, 68.1) * mm, "radius": 2 * mm});
            skCircle(sketch, "E7.0.26.24", {"center": v(98.1, 84.1) * mm, "radius": 2 * mm});
            skCircle(sketch, "E7.0.26.25", {"center": v(98.1, 100.1) * mm, "radius": 2 * mm});
            skCircle(sketch, "E7.0.26.26", {"center": v(98.1, 116.1) * mm, "radius": 2 * mm});
            skCircle(sketch, "E7.0.26.27", {"center": v(98.1, 132.1) * mm, "radius": 2 * mm});
            skCircle(sketch, "E7.0.26.28", {"center": v(98.1, 148.1) * mm, "radius": 2 * mm});
            skCircle(sketch, "E7.0.26.29", {"center": v(98.1, 164.1) * mm, "radius": 2 * mm});
            skCircle(sketch, "E7.0.26.30", {"center": v(98.1, 180.1) * mm, "radius": 2 * mm});
            skCircle(sketch, "E7.0.26.31", {"center": v(98.1, 196.1) * mm, "radius": 2 * mm});
            skCircle(sketch, "E7.0.26.32", {"center": v(98.1, 212.1) * mm, "radius": 2 * mm});
            skCircle(sketch, "E7.0.26.33", {"center": v(98.1, 228.1) * mm, "radius": 2 * mm});
            skCircle(sketch, "E7.0.26.34", {"center": v(98.1, 244.1) * mm, "radius": 2 * mm});
            skCircle(sketch, "E7.0.26.35", {"center": v(98.1, 260.1) * mm, "radius": 2 * mm});
            skCircle(sketch, "E7.0.26.36", {"center": v(98.1, 276.1) * mm, "radius": 2 * mm});
            skCircle(sketch, "E7.0.26.37", {"center": v(98.1, 292.1) * mm, "radius": 2 * mm});
            skCircle(sketch, "E7.0.27.10", {"center": v(114.1, -139.9) * mm, "radius": 2 * mm});
            skCircle(sketch, "E7.0.27.11", {"center": v(114.1, -123.9) * mm, "radius": 2 * mm});
            skCircle(sketch, "E7.0.27.12", {"center": v(114.1, -107.9) * mm, "radius": 2 * mm});
            skCircle(sketch, "E7.0.27.13", {"center": v(114.1, -91.9) * mm, "radius": 2 * mm});
            skCircle(sketch, "E7.0.27.14", {"center": v(114.1, -75.9) * mm, "radius": 2 * mm});
            skCircle(sketch, "E7.0.27.15", {"center": v(114.1, -59.9) * mm, "radius": 2 * mm});
            skCircle(sketch, "E7.0.27.16", {"center": v(114.1, -43.9) * mm, "radius": 2 * mm});
            skCircle(sketch, "E7.0.27.17", {"center": v(114.1, -27.9) * mm, "radius": 2 * mm});
            skCircle(sketch, "E7.0.27.18", {"center": v(114.1, -11.9) * mm, "radius": 2 * mm});
            skCircle(sketch, "E7.0.27.19", {"center": v(114.1, 4.1) * mm, "radius": 2 * mm});
            skCircle(sketch, "E7.0.27.20", {"center": v(114.1, 20.1) * mm, "radius": 2 * mm});
            skCircle(sketch, "E7.0.27.21", {"center": v(114.1, 36.1) * mm, "radius": 2 * mm});
            skCircle(sketch, "E7.0.27.22", {"center": v(114.1, 52.1) * mm, "radius": 2 * mm});
            skCircle(sketch, "E7.0.27.23", {"center": v(114.1, 68.1) * mm, "radius": 2 * mm});
            skCircle(sketch, "E7.0.27.24", {"center": v(114.1, 84.1) * mm, "radius": 2 * mm});
            skCircle(sketch, "E7.0.27.25", {"center": v(114.1, 100.1) * mm, "radius": 2 * mm});
            skCircle(sketch, "E7.0.27.26", {"center": v(114.1, 116.1) * mm, "radius": 2 * mm});
            skCircle(sketch, "E7.0.27.27", {"center": v(114.1, 132.1) * mm, "radius": 2 * mm});
            skCircle(sketch, "E7.0.27.28", {"center": v(114.1, 148.1) * mm, "radius": 2 * mm});
            skCircle(sketch, "E7.0.27.29", {"center": v(114.1, 164.1) * mm, "radius": 2 * mm});
            skCircle(sketch, "E7.0.27.30", {"center": v(114.1, 180.1) * mm, "radius": 2 * mm});
            skCircle(sketch, "E7.0.27.31", {"center": v(114.1, 196.1) * mm, "radius": 2 * mm});
            skCircle(sketch, "E7.0.27.32", {"center": v(114.1, 212.1) * mm, "radius": 2 * mm});
            skCircle(sketch, "E7.0.27.33", {"center": v(114.1, 228.1) * mm, "radius": 2 * mm});
            skCircle(sketch, "E7.0.27.34", {"center": v(114.1, 244.1) * mm, "radius": 2 * mm});
            skCircle(sketch, "E7.0.27.35", {"center": v(114.1, 260.1) * mm, "radius": 2 * mm});
            skCircle(sketch, "E7.0.27.36", {"center": v(114.1, 276.1) * mm, "radius": 2 * mm});
            skCircle(sketch, "E7.0.27.37", {"center": v(114.1, 292.1) * mm, "radius": 2 * mm});
            skCircle(sketch, "E7.0.28.10", {"center": v(130.1, -139.9) * mm, "radius": 2 * mm});
            skCircle(sketch, "E7.0.28.11", {"center": v(130.1, -123.9) * mm, "radius": 2 * mm});
            skCircle(sketch, "E7.0.28.12", {"center": v(130.1, -107.9) * mm, "radius": 2 * mm});
            skCircle(sketch, "E7.0.28.13", {"center": v(130.1, -91.9) * mm, "radius": 2 * mm});
            skCircle(sketch, "E7.0.28.14", {"center": v(130.1, -75.9) * mm, "radius": 2 * mm});
            skCircle(sketch, "E7.0.28.15", {"center": v(130.1, -59.9) * mm, "radius": 2 * mm});
            skCircle(sketch, "E7.0.28.16", {"center": v(130.1, -43.9) * mm, "radius": 2 * mm});
            skCircle(sketch, "E7.0.28.17", {"center": v(130.1, -27.9) * mm, "radius": 2 * mm});
            skCircle(sketch, "E7.0.28.18", {"center": v(130.1, -11.9) * mm, "radius": 2 * mm});
            skCircle(sketch, "E7.0.28.19", {"center": v(130.1, 4.1) * mm, "radius": 2 * mm});
            skCircle(sketch, "E7.0.28.20", {"center": v(130.1, 20.1) * mm, "radius": 2 * mm});
            skCircle(sketch, "E7.0.28.21", {"center": v(130.1, 36.1) * mm, "radius": 2 * mm});
            skCircle(sketch, "E7.0.28.22", {"center": v(130.1, 52.1) * mm, "radius": 2 * mm});
            skCircle(sketch, "E7.0.28.23", {"center": v(130.1, 68.1) * mm, "radius": 2 * mm});
            skCircle(sketch, "E7.0.28.24", {"center": v(130.1, 84.1) * mm, "radius": 2 * mm});
            skCircle(sketch, "E7.0.28.25", {"center": v(130.1, 100.1) * mm, "radius": 2 * mm});
            skCircle(sketch, "E7.0.28.26", {"center": v(130.1, 116.1) * mm, "radius": 2 * mm});
            skCircle(sketch, "E7.0.28.27", {"center": v(130.1, 132.1) * mm, "radius": 2 * mm});
            skCircle(sketch, "E7.0.28.28", {"center": v(130.1, 148.1) * mm, "radius": 2 * mm});
            skCircle(sketch, "E7.0.28.29", {"center": v(130.1, 164.1) * mm, "radius": 2 * mm});
            skCircle(sketch, "E7.0.28.30", {"center": v(130.1, 180.1) * mm, "radius": 2 * mm});
            skCircle(sketch, "E7.0.28.31", {"center": v(130.1, 196.1) * mm, "radius": 2 * mm});
            skCircle(sketch, "E7.0.28.32", {"center": v(130.1, 212.1) * mm, "radius": 2 * mm});
            skCircle(sketch, "E7.0.28.33", {"center": v(130.1, 228.1) * mm, "radius": 2 * mm});
            skCircle(sketch, "E7.0.28.34", {"center": v(130.1, 244.1) * mm, "radius": 2 * mm});
            skCircle(sketch, "E7.0.28.35", {"center": v(130.1, 260.1) * mm, "radius": 2 * mm});
            skCircle(sketch, "E7.0.28.36", {"center": v(130.1, 276.1) * mm, "radius": 2 * mm});
            skCircle(sketch, "E7.0.28.37", {"center": v(130.1, 292.1) * mm, "radius": 2 * mm});
            skCircle(sketch, "E7.0.29.10", {"center": v(146.1, -139.9) * mm, "radius": 2 * mm});
            skCircle(sketch, "E7.0.29.11", {"center": v(146.1, -123.9) * mm, "radius": 2 * mm});
            skCircle(sketch, "E7.0.29.12", {"center": v(146.1, -107.9) * mm, "radius": 2 * mm});
            skCircle(sketch, "E7.0.29.13", {"center": v(146.1, -91.9) * mm, "radius": 2 * mm});
            skCircle(sketch, "E7.0.29.14", {"center": v(146.1, -75.9) * mm, "radius": 2 * mm});
            skCircle(sketch, "E7.0.29.15", {"center": v(146.1, -59.9) * mm, "radius": 2 * mm});
            skCircle(sketch, "E7.0.29.16", {"center": v(146.1, -43.9) * mm, "radius": 2 * mm});
            skCircle(sketch, "E7.0.29.17", {"center": v(146.1, -27.9) * mm, "radius": 2 * mm});
            skCircle(sketch, "E7.0.29.18", {"center": v(146.1, -11.9) * mm, "radius": 2 * mm});
            skCircle(sketch, "E7.0.29.19", {"center": v(146.1, 4.1) * mm, "radius": 2 * mm});
            skCircle(sketch, "E7.0.29.20", {"center": v(146.1, 20.1) * mm, "radius": 2 * mm});
            skCircle(sketch, "E7.0.29.21", {"center": v(146.1, 36.1) * mm, "radius": 2 * mm});
            skCircle(sketch, "E7.0.29.22", {"center": v(146.1, 52.1) * mm, "radius": 2 * mm});
            skCircle(sketch, "E7.0.29.23", {"center": v(146.1, 68.1) * mm, "radius": 2 * mm});
            skCircle(sketch, "E7.0.29.24", {"center": v(146.1, 84.1) * mm, "radius": 2 * mm});
            skCircle(sketch, "E7.0.29.25", {"center": v(146.1, 100.1) * mm, "radius": 2 * mm});
            skCircle(sketch, "E7.0.29.26", {"center": v(146.1, 116.1) * mm, "radius": 2 * mm});
            skCircle(sketch, "E7.0.29.27", {"center": v(146.1, 132.1) * mm, "radius": 2 * mm});
            skCircle(sketch, "E7.0.29.28", {"center": v(146.1, 148.1) * mm, "radius": 2 * mm});
            skCircle(sketch, "E7.0.29.29", {"center": v(146.1, 164.1) * mm, "radius": 2 * mm});
            skCircle(sketch, "E7.0.29.30", {"center": v(146.1, 180.1) * mm, "radius": 2 * mm});
            skCircle(sketch, "E7.0.29.31", {"center": v(146.1, 196.1) * mm, "radius": 2 * mm});
            skCircle(sketch, "E7.0.29.32", {"center": v(146.1, 212.1) * mm, "radius": 2 * mm});
            skCircle(sketch, "E7.0.29.33", {"center": v(146.1, 228.1) * mm, "radius": 2 * mm});
            skCircle(sketch, "E7.0.29.34", {"center": v(146.1, 244.1) * mm, "radius": 2 * mm});
            skCircle(sketch, "E7.0.29.35", {"center": v(146.1, 260.1) * mm, "radius": 2 * mm});
            skCircle(sketch, "E7.0.29.36", {"center": v(146.1, 276.1) * mm, "radius": 2 * mm});
            skCircle(sketch, "E7.0.29.37", {"center": v(146.1, 292.1) * mm, "radius": 2 * mm});
            skCircle(sketch, "E7.0.30.10", {"center": v(162.1, -139.9) * mm, "radius": 2 * mm});
            skCircle(sketch, "E7.0.30.11", {"center": v(162.1, -123.9) * mm, "radius": 2 * mm});
            skCircle(sketch, "E7.0.30.12", {"center": v(162.1, -107.9) * mm, "radius": 2 * mm});
            skCircle(sketch, "E7.0.30.13", {"center": v(162.1, -91.9) * mm, "radius": 2 * mm});
            skCircle(sketch, "E7.0.30.14", {"center": v(162.1, -75.9) * mm, "radius": 2 * mm});
            skCircle(sketch, "E7.0.30.15", {"center": v(162.1, -59.9) * mm, "radius": 2 * mm});
            skCircle(sketch, "E7.0.30.16", {"center": v(162.1, -43.9) * mm, "radius": 2 * mm});
            skCircle(sketch, "E7.0.30.17", {"center": v(162.1, -27.9) * mm, "radius": 2 * mm});
            skCircle(sketch, "E7.0.30.18", {"center": v(162.1, -11.9) * mm, "radius": 2 * mm});
            skCircle(sketch, "E7.0.30.19", {"center": v(162.1, 4.1) * mm, "radius": 2 * mm});
            skCircle(sketch, "E7.0.30.20", {"center": v(162.1, 20.1) * mm, "radius": 2 * mm});
            skCircle(sketch, "E7.0.30.21", {"center": v(162.1, 36.1) * mm, "radius": 2 * mm});
            skCircle(sketch, "E7.0.30.22", {"center": v(162.1, 52.1) * mm, "radius": 2 * mm});
            skCircle(sketch, "E7.0.30.23", {"center": v(162.1, 68.1) * mm, "radius": 2 * mm});
            skCircle(sketch, "E7.0.30.24", {"center": v(162.1, 84.1) * mm, "radius": 2 * mm});
            skCircle(sketch, "E7.0.30.25", {"center": v(162.1, 100.1) * mm, "radius": 2 * mm});
            skCircle(sketch, "E7.0.30.26", {"center": v(162.1, 116.1) * mm, "radius": 2 * mm});
            skCircle(sketch, "E7.0.30.27", {"center": v(162.1, 132.1) * mm, "radius": 2 * mm});
            skCircle(sketch, "E7.0.30.28", {"center": v(162.1, 148.1) * mm, "radius": 2 * mm});
            skCircle(sketch, "E7.0.30.29", {"center": v(162.1, 164.1) * mm, "radius": 2 * mm});
            skCircle(sketch, "E7.0.30.30", {"center": v(162.1, 180.1) * mm, "radius": 2 * mm});
            skCircle(sketch, "E7.0.30.31", {"center": v(162.1, 196.1) * mm, "radius": 2 * mm});
            skCircle(sketch, "E7.0.30.32", {"center": v(162.1, 212.1) * mm, "radius": 2 * mm});
            skCircle(sketch, "E7.0.30.33", {"center": v(162.1, 228.1) * mm, "radius": 2 * mm});
            skCircle(sketch, "E7.0.30.34", {"center": v(162.1, 244.1) * mm, "radius": 2 * mm});
            skCircle(sketch, "E7.0.30.35", {"center": v(162.1, 260.1) * mm, "radius": 2 * mm});
            skCircle(sketch, "E7.0.30.36", {"center": v(162.1, 276.1) * mm, "radius": 2 * mm});
            skCircle(sketch, "E7.0.30.37", {"center": v(162.1, 292.1) * mm, "radius": 2 * mm});
            skCircle(sketch, "E7.0.31.10", {"center": v(178.1, -139.9) * mm, "radius": 2 * mm});
            skCircle(sketch, "E7.0.31.11", {"center": v(178.1, -123.9) * mm, "radius": 2 * mm});
            skCircle(sketch, "E7.0.31.12", {"center": v(178.1, -107.9) * mm, "radius": 2 * mm});
            skCircle(sketch, "E7.0.31.13", {"center": v(178.1, -91.9) * mm, "radius": 2 * mm});
            skCircle(sketch, "E7.0.31.14", {"center": v(178.1, -75.9) * mm, "radius": 2 * mm});
            skCircle(sketch, "E7.0.31.15", {"center": v(178.1, -59.9) * mm, "radius": 2 * mm});
            skCircle(sketch, "E7.0.31.16", {"center": v(178.1, -43.9) * mm, "radius": 2 * mm});
            skCircle(sketch, "E7.0.31.17", {"center": v(178.1, -27.9) * mm, "radius": 2 * mm});
            skCircle(sketch, "E7.0.31.18", {"center": v(178.1, -11.9) * mm, "radius": 2 * mm});
            skCircle(sketch, "E7.0.31.19", {"center": v(178.1, 4.1) * mm, "radius": 2 * mm});
            skCircle(sketch, "E7.0.31.20", {"center": v(178.1, 20.1) * mm, "radius": 2 * mm});
            skCircle(sketch, "E7.0.31.21", {"center": v(178.1, 36.1) * mm, "radius": 2 * mm});
            skCircle(sketch, "E7.0.31.22", {"center": v(178.1, 52.1) * mm, "radius": 2 * mm});
            skCircle(sketch, "E7.0.31.23", {"center": v(178.1, 68.1) * mm, "radius": 2 * mm});
            skCircle(sketch, "E7.0.31.24", {"center": v(178.1, 84.1) * mm, "radius": 2 * mm});
            skCircle(sketch, "E7.0.31.25", {"center": v(178.1, 100.1) * mm, "radius": 2 * mm});
            skCircle(sketch, "E7.0.31.26", {"center": v(178.1, 116.1) * mm, "radius": 2 * mm});
            skCircle(sketch, "E7.0.31.27", {"center": v(178.1, 132.1) * mm, "radius": 2 * mm});
            skCircle(sketch, "E7.0.31.28", {"center": v(178.1, 148.1) * mm, "radius": 2 * mm});
            skCircle(sketch, "E7.0.31.29", {"center": v(178.1, 164.1) * mm, "radius": 2 * mm});
            skCircle(sketch, "E7.0.31.30", {"center": v(178.1, 180.1) * mm, "radius": 2 * mm});
            skCircle(sketch, "E7.0.31.31", {"center": v(178.1, 196.1) * mm, "radius": 2 * mm});
            skCircle(sketch, "E7.0.31.32", {"center": v(178.1, 212.1) * mm, "radius": 2 * mm});
            skCircle(sketch, "E7.0.31.33", {"center": v(178.1, 228.1) * mm, "radius": 2 * mm});
            skCircle(sketch, "E7.0.31.34", {"center": v(178.1, 244.1) * mm, "radius": 2 * mm});
            skCircle(sketch, "E7.0.31.35", {"center": v(178.1, 260.1) * mm, "radius": 2 * mm});
            skCircle(sketch, "E7.0.31.36", {"center": v(178.1, 276.1) * mm, "radius": 2 * mm});
            skCircle(sketch, "E7.0.31.37", {"center": v(178.1, 292.1) * mm, "radius": 2 * mm});
            skCircle(sketch, "E7.0.32.10", {"center": v(194.1, -139.9) * mm, "radius": 2 * mm});
            skCircle(sketch, "E7.0.32.11", {"center": v(194.1, -123.9) * mm, "radius": 2 * mm});
            skCircle(sketch, "E7.0.32.12", {"center": v(194.1, -107.9) * mm, "radius": 2 * mm});
            skCircle(sketch, "E7.0.32.13", {"center": v(194.1, -91.9) * mm, "radius": 2 * mm});
            skCircle(sketch, "E7.0.32.14", {"center": v(194.1, -75.9) * mm, "radius": 2 * mm});
            skCircle(sketch, "E7.0.32.15", {"center": v(194.1, -59.9) * mm, "radius": 2 * mm});
            skCircle(sketch, "E7.0.32.16", {"center": v(194.1, -43.9) * mm, "radius": 2 * mm});
            skCircle(sketch, "E7.0.32.17", {"center": v(194.1, -27.9) * mm, "radius": 2 * mm});
            skCircle(sketch, "E7.0.32.18", {"center": v(194.1, -11.9) * mm, "radius": 2 * mm});
            skCircle(sketch, "E7.0.32.19", {"center": v(194.1, 4.1) * mm, "radius": 2 * mm});
            skCircle(sketch, "E7.0.32.20", {"center": v(194.1, 20.1) * mm, "radius": 2 * mm});
            skCircle(sketch, "E7.0.32.21", {"center": v(194.1, 36.1) * mm, "radius": 2 * mm});
            skCircle(sketch, "E7.0.32.22", {"center": v(194.1, 52.1) * mm, "radius": 2 * mm});
            skCircle(sketch, "E7.0.32.23", {"center": v(194.1, 68.1) * mm, "radius": 2 * mm});
            skCircle(sketch, "E7.0.32.24", {"center": v(194.1, 84.1) * mm, "radius": 2 * mm});
            skCircle(sketch, "E7.0.32.25", {"center": v(194.1, 100.1) * mm, "radius": 2 * mm});
            skCircle(sketch, "E7.0.32.26", {"center": v(194.1, 116.1) * mm, "radius": 2 * mm});
            skCircle(sketch, "E7.0.32.27", {"center": v(194.1, 132.1) * mm, "radius": 2 * mm});
            skCircle(sketch, "E7.0.32.28", {"center": v(194.1, 148.1) * mm, "radius": 2 * mm});
            skCircle(sketch, "E7.0.32.29", {"center": v(194.1, 164.1) * mm, "radius": 2 * mm});
            skCircle(sketch, "E7.0.32.30", {"center": v(194.1, 180.1) * mm, "radius": 2 * mm});
            skCircle(sketch, "E7.0.32.31", {"center": v(194.1, 196.1) * mm, "radius": 2 * mm});
            skCircle(sketch, "E7.0.32.32", {"center": v(194.1, 212.1) * mm, "radius": 2 * mm});
            skCircle(sketch, "E7.0.32.33", {"center": v(194.1, 228.1) * mm, "radius": 2 * mm});
            skCircle(sketch, "E7.0.32.34", {"center": v(194.1, 244.1) * mm, "radius": 2 * mm});
            skCircle(sketch, "E7.0.32.35", {"center": v(194.1, 260.1) * mm, "radius": 2 * mm});
            skCircle(sketch, "E7.0.32.36", {"center": v(194.1, 276.1) * mm, "radius": 2 * mm});
            skCircle(sketch, "E7.0.32.37", {"center": v(194.1, 292.1) * mm, "radius": 2 * mm});
            skCircle(sketch, "E7.0.33.10", {"center": v(210.1, -139.9) * mm, "radius": 2 * mm});
            skCircle(sketch, "E7.0.33.11", {"center": v(210.1, -123.9) * mm, "radius": 2 * mm});
            skCircle(sketch, "E7.0.33.12", {"center": v(210.1, -107.9) * mm, "radius": 2 * mm});
            skCircle(sketch, "E7.0.33.13", {"center": v(210.1, -91.9) * mm, "radius": 2 * mm});
            skCircle(sketch, "E7.0.33.14", {"center": v(210.1, -75.9) * mm, "radius": 2 * mm});
            skCircle(sketch, "E7.0.33.15", {"center": v(210.1, -59.9) * mm, "radius": 2 * mm});
            skCircle(sketch, "E7.0.33.16", {"center": v(210.1, -43.9) * mm, "radius": 2 * mm});
            skCircle(sketch, "E7.0.33.17", {"center": v(210.1, -27.9) * mm, "radius": 2 * mm});
            skCircle(sketch, "E7.0.33.18", {"center": v(210.1, -11.9) * mm, "radius": 2 * mm});
            skCircle(sketch, "E7.0.33.19", {"center": v(210.1, 4.1) * mm, "radius": 2 * mm});
            skCircle(sketch, "E7.0.33.20", {"center": v(210.1, 20.1) * mm, "radius": 2 * mm});
            skCircle(sketch, "E7.0.33.21", {"center": v(210.1, 36.1) * mm, "radius": 2 * mm});
            skCircle(sketch, "E7.0.33.22", {"center": v(210.1, 52.1) * mm, "radius": 2 * mm});
            skCircle(sketch, "E7.0.33.23", {"center": v(210.1, 68.1) * mm, "radius": 2 * mm});
            skCircle(sketch, "E7.0.33.24", {"center": v(210.1, 84.1) * mm, "radius": 2 * mm});
            skCircle(sketch, "E7.0.33.25", {"center": v(210.1, 100.1) * mm, "radius": 2 * mm});
            skCircle(sketch, "E7.0.33.26", {"center": v(210.1, 116.1) * mm, "radius": 2 * mm});
            skCircle(sketch, "E7.0.33.27", {"center": v(210.1, 132.1) * mm, "radius": 2 * mm});
            skCircle(sketch, "E7.0.33.28", {"center": v(210.1, 148.1) * mm, "radius": 2 * mm});
            skCircle(sketch, "E7.0.33.29", {"center": v(210.1, 164.1) * mm, "radius": 2 * mm});
            skCircle(sketch, "E7.0.33.30", {"center": v(210.1, 180.1) * mm, "radius": 2 * mm});
            skCircle(sketch, "E7.0.33.31", {"center": v(210.1, 196.1) * mm, "radius": 2 * mm});
            skCircle(sketch, "E7.0.33.32", {"center": v(210.1, 212.1) * mm, "radius": 2 * mm});
            skCircle(sketch, "E7.0.33.33", {"center": v(210.1, 228.1) * mm, "radius": 2 * mm});
            skCircle(sketch, "E7.0.33.34", {"center": v(210.1, 244.1) * mm, "radius": 2 * mm});
            skCircle(sketch, "E7.0.33.35", {"center": v(210.1, 260.1) * mm, "radius": 2 * mm});
            skCircle(sketch, "E7.0.33.36", {"center": v(210.1, 276.1) * mm, "radius": 2 * mm});
            skCircle(sketch, "E7.0.33.37", {"center": v(210.1, 292.1) * mm, "radius": 2 * mm});
            skCircle(sketch, "E7.0.34.10", {"center": v(226.1, -139.9) * mm, "radius": 2 * mm});
            skCircle(sketch, "E7.0.34.11", {"center": v(226.1, -123.9) * mm, "radius": 2 * mm});
            skCircle(sketch, "E7.0.34.12", {"center": v(226.1, -107.9) * mm, "radius": 2 * mm});
            skCircle(sketch, "E7.0.34.13", {"center": v(226.1, -91.9) * mm, "radius": 2 * mm});
            skCircle(sketch, "E7.0.34.14", {"center": v(226.1, -75.9) * mm, "radius": 2 * mm});
            skCircle(sketch, "E7.0.34.15", {"center": v(226.1, -59.9) * mm, "radius": 2 * mm});
            skCircle(sketch, "E7.0.34.16", {"center": v(226.1, -43.9) * mm, "radius": 2 * mm});
            skCircle(sketch, "E7.0.34.17", {"center": v(226.1, -27.9) * mm, "radius": 2 * mm});
            skCircle(sketch, "E7.0.34.18", {"center": v(226.1, -11.9) * mm, "radius": 2 * mm});
            skCircle(sketch, "E7.0.34.19", {"center": v(226.1, 4.1) * mm, "radius": 2 * mm});
            skCircle(sketch, "E7.0.34.20", {"center": v(226.1, 20.1) * mm, "radius": 2 * mm});
            skCircle(sketch, "E7.0.34.21", {"center": v(226.1, 36.1) * mm, "radius": 2 * mm});
            skCircle(sketch, "E7.0.34.22", {"center": v(226.1, 52.1) * mm, "radius": 2 * mm});
            skCircle(sketch, "E7.0.34.23", {"center": v(226.1, 68.1) * mm, "radius": 2 * mm});
            skCircle(sketch, "E7.0.34.24", {"center": v(226.1, 84.1) * mm, "radius": 2 * mm});
            skCircle(sketch, "E7.0.34.25", {"center": v(226.1, 100.1) * mm, "radius": 2 * mm});
            skCircle(sketch, "E7.0.34.26", {"center": v(226.1, 116.1) * mm, "radius": 2 * mm});
            skCircle(sketch, "E7.0.34.27", {"center": v(226.1, 132.1) * mm, "radius": 2 * mm});
            skCircle(sketch, "E7.0.34.28", {"center": v(226.1, 148.1) * mm, "radius": 2 * mm});
            skCircle(sketch, "E7.0.34.29", {"center": v(226.1, 164.1) * mm, "radius": 2 * mm});
            skCircle(sketch, "E7.0.34.30", {"center": v(226.1, 180.1) * mm, "radius": 2 * mm});
            skCircle(sketch, "E7.0.34.31", {"center": v(226.1, 196.1) * mm, "radius": 2 * mm});
            skCircle(sketch, "E7.0.34.32", {"center": v(226.1, 212.1) * mm, "radius": 2 * mm});
            skCircle(sketch, "E7.0.34.33", {"center": v(226.1, 228.1) * mm, "radius": 2 * mm});
            skCircle(sketch, "E7.0.34.34", {"center": v(226.1, 244.1) * mm, "radius": 2 * mm});
            skCircle(sketch, "E7.0.34.35", {"center": v(226.1, 260.1) * mm, "radius": 2 * mm});
            skCircle(sketch, "E7.0.34.36", {"center": v(226.1, 276.1) * mm, "radius": 2 * mm});
            skCircle(sketch, "E7.0.34.37", {"center": v(226.1, 292.1) * mm, "radius": 2 * mm});
            skCircle(sketch, "E7.0.35.10", {"center": v(242.1, -139.9) * mm, "radius": 2 * mm});
            skCircle(sketch, "E7.0.35.11", {"center": v(242.1, -123.9) * mm, "radius": 2 * mm});
            skCircle(sketch, "E7.0.35.12", {"center": v(242.1, -107.9) * mm, "radius": 2 * mm});
            skCircle(sketch, "E7.0.35.13", {"center": v(242.1, -91.9) * mm, "radius": 2 * mm});
            skCircle(sketch, "E7.0.35.14", {"center": v(242.1, -75.9) * mm, "radius": 2 * mm});
            skCircle(sketch, "E7.0.35.15", {"center": v(242.1, -59.9) * mm, "radius": 2 * mm});
            skCircle(sketch, "E7.0.35.16", {"center": v(242.1, -43.9) * mm, "radius": 2 * mm});
            skCircle(sketch, "E7.0.35.17", {"center": v(242.1, -27.9) * mm, "radius": 2 * mm});
            skCircle(sketch, "E7.0.35.18", {"center": v(242.1, -11.9) * mm, "radius": 2 * mm});
            skCircle(sketch, "E7.0.35.19", {"center": v(242.1, 4.1) * mm, "radius": 2 * mm});
            skCircle(sketch, "E7.0.35.20", {"center": v(242.1, 20.1) * mm, "radius": 2 * mm});
            skCircle(sketch, "E7.0.35.21", {"center": v(242.1, 36.1) * mm, "radius": 2 * mm});
            skCircle(sketch, "E7.0.35.22", {"center": v(242.1, 52.1) * mm, "radius": 2 * mm});
            skCircle(sketch, "E7.0.35.23", {"center": v(242.1, 68.1) * mm, "radius": 2 * mm});
            skCircle(sketch, "E7.0.35.24", {"center": v(242.1, 84.1) * mm, "radius": 2 * mm});
            skCircle(sketch, "E7.0.35.25", {"center": v(242.1, 100.1) * mm, "radius": 2 * mm});
            skCircle(sketch, "E7.0.35.26", {"center": v(242.1, 116.1) * mm, "radius": 2 * mm});
            skCircle(sketch, "E7.0.35.27", {"center": v(242.1, 132.1) * mm, "radius": 2 * mm});
            skCircle(sketch, "E7.0.35.28", {"center": v(242.1, 148.1) * mm, "radius": 2 * mm});
            skCircle(sketch, "E7.0.35.29", {"center": v(242.1, 164.1) * mm, "radius": 2 * mm});
            skCircle(sketch, "E7.0.35.30", {"center": v(242.1, 180.1) * mm, "radius": 2 * mm});
            skCircle(sketch, "E7.0.35.31", {"center": v(242.1, 196.1) * mm, "radius": 2 * mm});
            skCircle(sketch, "E7.0.35.32", {"center": v(242.1, 212.1) * mm, "radius": 2 * mm});
            skCircle(sketch, "E7.0.35.33", {"center": v(242.1, 228.1) * mm, "radius": 2 * mm});
            skCircle(sketch, "E7.0.35.34", {"center": v(242.1, 244.1) * mm, "radius": 2 * mm});
            skCircle(sketch, "E7.0.35.35", {"center": v(242.1, 260.1) * mm, "radius": 2 * mm});
            skCircle(sketch, "E7.0.35.36", {"center": v(242.1, 276.1) * mm, "radius": 2 * mm});
            skCircle(sketch, "E7.0.35.37", {"center": v(242.1, 292.1) * mm, "radius": 2 * mm});
            skCircle(sketch, "E7.0.36.10", {"center": v(258.1, -139.9) * mm, "radius": 2 * mm});
            skCircle(sketch, "E7.0.36.11", {"center": v(258.1, -123.9) * mm, "radius": 2 * mm});
            skCircle(sketch, "E7.0.36.12", {"center": v(258.1, -107.9) * mm, "radius": 2 * mm});
            skCircle(sketch, "E7.0.36.13", {"center": v(258.1, -91.9) * mm, "radius": 2 * mm});
            skCircle(sketch, "E7.0.36.14", {"center": v(258.1, -75.9) * mm, "radius": 2 * mm});
            skCircle(sketch, "E7.0.36.15", {"center": v(258.1, -59.9) * mm, "radius": 2 * mm});
            skCircle(sketch, "E7.0.36.16", {"center": v(258.1, -43.9) * mm, "radius": 2 * mm});
            skCircle(sketch, "E7.0.36.17", {"center": v(258.1, -27.9) * mm, "radius": 2 * mm});
            skCircle(sketch, "E7.0.36.18", {"center": v(258.1, -11.9) * mm, "radius": 2 * mm});
            skCircle(sketch, "E7.0.36.19", {"center": v(258.1, 4.1) * mm, "radius": 2 * mm});
            skCircle(sketch, "E7.0.36.20", {"center": v(258.1, 20.1) * mm, "radius": 2 * mm});
            skCircle(sketch, "E7.0.36.21", {"center": v(258.1, 36.1) * mm, "radius": 2 * mm});
            skCircle(sketch, "E7.0.36.22", {"center": v(258.1, 52.1) * mm, "radius": 2 * mm});
            skCircle(sketch, "E7.0.36.23", {"center": v(258.1, 68.1) * mm, "radius": 2 * mm});
            skCircle(sketch, "E7.0.36.24", {"center": v(258.1, 84.1) * mm, "radius": 2 * mm});
            skCircle(sketch, "E7.0.36.25", {"center": v(258.1, 100.1) * mm, "radius": 2 * mm});
            skCircle(sketch, "E7.0.36.26", {"center": v(258.1, 116.1) * mm, "radius": 2 * mm});
            skCircle(sketch, "E7.0.36.27", {"center": v(258.1, 132.1) * mm, "radius": 2 * mm});
            skCircle(sketch, "E7.0.36.28", {"center": v(258.1, 148.1) * mm, "radius": 2 * mm});
            skCircle(sketch, "E7.0.36.29", {"center": v(258.1, 164.1) * mm, "radius": 2 * mm});
            skCircle(sketch, "E7.0.36.30", {"center": v(258.1, 180.1) * mm, "radius": 2 * mm});
            skCircle(sketch, "E7.0.36.31", {"center": v(258.1, 196.1) * mm, "radius": 2 * mm});
            skCircle(sketch, "E7.0.36.32", {"center": v(258.1, 212.1) * mm, "radius": 2 * mm});
            skCircle(sketch, "E7.0.36.33", {"center": v(258.1, 228.1) * mm, "radius": 2 * mm});
            skCircle(sketch, "E7.0.36.34", {"center": v(258.1, 244.1) * mm, "radius": 2 * mm});
            skCircle(sketch, "E7.0.36.35", {"center": v(258.1, 260.1) * mm, "radius": 2 * mm});
            skCircle(sketch, "E7.0.36.36", {"center": v(258.1, 276.1) * mm, "radius": 2 * mm});
            skCircle(sketch, "E7.0.36.37", {"center": v(258.1, 292.1) * mm, "radius": 2 * mm});
            skCircle(sketch, "E7.0.37.10", {"center": v(274.1, -139.9) * mm, "radius": 2 * mm});
            skCircle(sketch, "E7.0.37.11", {"center": v(274.1, -123.9) * mm, "radius": 2 * mm});
            skCircle(sketch, "E7.0.37.12", {"center": v(274.1, -107.9) * mm, "radius": 2 * mm});
            skCircle(sketch, "E7.0.37.13", {"center": v(274.1, -91.9) * mm, "radius": 2 * mm});
            skCircle(sketch, "E7.0.37.14", {"center": v(274.1, -75.9) * mm, "radius": 2 * mm});
            skCircle(sketch, "E7.0.37.15", {"center": v(274.1, -59.9) * mm, "radius": 2 * mm});
            skCircle(sketch, "E7.0.37.16", {"center": v(274.1, -43.9) * mm, "radius": 2 * mm});
            skCircle(sketch, "E7.0.37.17", {"center": v(274.1, -27.9) * mm, "radius": 2 * mm});
            skCircle(sketch, "E7.0.37.18", {"center": v(274.1, -11.9) * mm, "radius": 2 * mm});
            skCircle(sketch, "E7.0.37.19", {"center": v(274.1, 4.1) * mm, "radius": 2 * mm});
            skCircle(sketch, "E7.0.37.20", {"center": v(274.1, 20.1) * mm, "radius": 2 * mm});
            skCircle(sketch, "E7.0.37.21", {"center": v(274.1, 36.1) * mm, "radius": 2 * mm});
            skCircle(sketch, "E7.0.37.22", {"center": v(274.1, 52.1) * mm, "radius": 2 * mm});
            skCircle(sketch, "E7.0.37.23", {"center": v(274.1, 68.1) * mm, "radius": 2 * mm});
            skCircle(sketch, "E7.0.37.24", {"center": v(274.1, 84.1) * mm, "radius": 2 * mm});
            skCircle(sketch, "E7.0.37.25", {"center": v(274.1, 100.1) * mm, "radius": 2 * mm});
            skCircle(sketch, "E7.0.37.26", {"center": v(274.1, 116.1) * mm, "radius": 2 * mm});
            skCircle(sketch, "E7.0.37.27", {"center": v(274.1, 132.1) * mm, "radius": 2 * mm});
            skCircle(sketch, "E7.0.37.28", {"center": v(274.1, 148.1) * mm, "radius": 2 * mm});
            skCircle(sketch, "E7.0.37.29", {"center": v(274.1, 164.1) * mm, "radius": 2 * mm});
            skCircle(sketch, "E7.0.37.30", {"center": v(274.1, 180.1) * mm, "radius": 2 * mm});
            skCircle(sketch, "E7.0.37.31", {"center": v(274.1, 196.1) * mm, "radius": 2 * mm});
            skCircle(sketch, "E7.0.37.32", {"center": v(274.1, 212.1) * mm, "radius": 2 * mm});
            skCircle(sketch, "E7.0.37.33", {"center": v(274.1, 228.1) * mm, "radius": 2 * mm});
            skCircle(sketch, "E7.0.37.34", {"center": v(274.1, 244.1) * mm, "radius": 2 * mm});
            skCircle(sketch, "E7.0.37.35", {"center": v(274.1, 260.1) * mm, "radius": 2 * mm});
            skCircle(sketch, "E7.0.37.36", {"center": v(274.1, 276.1) * mm, "radius": 2 * mm});
            skCircle(sketch, "E7.0.37.37", {"center": v(274.1, 292.1) * mm, "radius": 2 * mm});
            skCircle(sketch, "E7.0.38.10", {"center": v(290.1, -139.9) * mm, "radius": 2 * mm});
            skCircle(sketch, "E7.0.38.11", {"center": v(290.1, -123.9) * mm, "radius": 2 * mm});
            skCircle(sketch, "E7.0.38.12", {"center": v(290.1, -107.9) * mm, "radius": 2 * mm});
            skCircle(sketch, "E7.0.38.13", {"center": v(290.1, -91.9) * mm, "radius": 2 * mm});
            skCircle(sketch, "E7.0.38.14", {"center": v(290.1, -75.9) * mm, "radius": 2 * mm});
            skCircle(sketch, "E7.0.38.15", {"center": v(290.1, -59.9) * mm, "radius": 2 * mm});
            skCircle(sketch, "E7.0.38.16", {"center": v(290.1, -43.9) * mm, "radius": 2 * mm});
            skCircle(sketch, "E7.0.38.17", {"center": v(290.1, -27.9) * mm, "radius": 2 * mm});
            skCircle(sketch, "E7.0.38.18", {"center": v(290.1, -11.9) * mm, "radius": 2 * mm});
            skCircle(sketch, "E7.0.38.19", {"center": v(290.1, 4.1) * mm, "radius": 2 * mm});
            skCircle(sketch, "E7.0.38.20", {"center": v(290.1, 20.1) * mm, "radius": 2 * mm});
            skCircle(sketch, "E7.0.38.21", {"center": v(290.1, 36.1) * mm, "radius": 2 * mm});
            skCircle(sketch, "E7.0.38.22", {"center": v(290.1, 52.1) * mm, "radius": 2 * mm});
            skCircle(sketch, "E7.0.38.23", {"center": v(290.1, 68.1) * mm, "radius": 2 * mm});
            skCircle(sketch, "E7.0.38.24", {"center": v(290.1, 84.1) * mm, "radius": 2 * mm});
            skCircle(sketch, "E7.0.38.25", {"center": v(290.1, 100.1) * mm, "radius": 2 * mm});
            skCircle(sketch, "E7.0.38.26", {"center": v(290.1, 116.1) * mm, "radius": 2 * mm});
            skCircle(sketch, "E7.0.38.27", {"center": v(290.1, 132.1) * mm, "radius": 2 * mm});
            skCircle(sketch, "E7.0.38.28", {"center": v(290.1, 148.1) * mm, "radius": 2 * mm});
            skCircle(sketch, "E7.0.38.29", {"center": v(290.1, 164.1) * mm, "radius": 2 * mm});
            skCircle(sketch, "E7.0.38.30", {"center": v(290.1, 180.1) * mm, "radius": 2 * mm});
            skCircle(sketch, "E7.0.38.31", {"center": v(290.1, 196.1) * mm, "radius": 2 * mm});
            skCircle(sketch, "E7.0.38.32", {"center": v(290.1, 212.1) * mm, "radius": 2 * mm});
            skCircle(sketch, "E7.0.38.33", {"center": v(290.1, 228.1) * mm, "radius": 2 * mm});
            skCircle(sketch, "E7.0.38.34", {"center": v(290.1, 244.1) * mm, "radius": 2 * mm});
            skCircle(sketch, "E7.0.38.35", {"center": v(290.1, 260.1) * mm, "radius": 2 * mm});
            skCircle(sketch, "E7.0.38.36", {"center": v(290.1, 276.1) * mm, "radius": 2 * mm});
            skCircle(sketch, "E7.0.38.37", {"center": v(290.1, 292.1) * mm, "radius": 2 * mm});
            skCircle(sketch, "E7.0.39.10", {"center": v(306.1, -139.9) * mm, "radius": 2 * mm});
            skCircle(sketch, "E7.0.39.11", {"center": v(306.1, -123.9) * mm, "radius": 2 * mm});
            skCircle(sketch, "E7.0.39.12", {"center": v(306.1, -107.9) * mm, "radius": 2 * mm});
            skCircle(sketch, "E7.0.39.13", {"center": v(306.1, -91.9) * mm, "radius": 2 * mm});
            skCircle(sketch, "E7.0.39.14", {"center": v(306.1, -75.9) * mm, "radius": 2 * mm});
            skCircle(sketch, "E7.0.39.15", {"center": v(306.1, -59.9) * mm, "radius": 2 * mm});
            skCircle(sketch, "E7.0.39.16", {"center": v(306.1, -43.9) * mm, "radius": 2 * mm});
            skCircle(sketch, "E7.0.39.17", {"center": v(306.1, -27.9) * mm, "radius": 2 * mm});
            skCircle(sketch, "E7.0.39.18", {"center": v(306.1, -11.9) * mm, "radius": 2 * mm});
            skCircle(sketch, "E7.0.39.19", {"center": v(306.1, 4.1) * mm, "radius": 2 * mm});
            skCircle(sketch, "E7.0.39.20", {"center": v(306.1, 20.1) * mm, "radius": 2 * mm});
            skCircle(sketch, "E7.0.39.21", {"center": v(306.1, 36.1) * mm, "radius": 2 * mm});
            skCircle(sketch, "E7.0.39.22", {"center": v(306.1, 52.1) * mm, "radius": 2 * mm});
            skCircle(sketch, "E7.0.39.23", {"center": v(306.1, 68.1) * mm, "radius": 2 * mm});
            skCircle(sketch, "E7.0.39.24", {"center": v(306.1, 84.1) * mm, "radius": 2 * mm});
            skCircle(sketch, "E7.0.39.25", {"center": v(306.1, 100.1) * mm, "radius": 2 * mm});
            skCircle(sketch, "E7.0.39.26", {"center": v(306.1, 116.1) * mm, "radius": 2 * mm});
            skCircle(sketch, "E7.0.39.27", {"center": v(306.1, 132.1) * mm, "radius": 2 * mm});
            skCircle(sketch, "E7.0.39.28", {"center": v(306.1, 148.1) * mm, "radius": 2 * mm});
            skCircle(sketch, "E7.0.39.29", {"center": v(306.1, 164.1) * mm, "radius": 2 * mm});
            skCircle(sketch, "E7.0.39.30", {"center": v(306.1, 180.1) * mm, "radius": 2 * mm});
            skCircle(sketch, "E7.0.39.31", {"center": v(306.1, 196.1) * mm, "radius": 2 * mm});
            skCircle(sketch, "E7.0.39.32", {"center": v(306.1, 212.1) * mm, "radius": 2 * mm});
            skCircle(sketch, "E7.0.39.33", {"center": v(306.1, 228.1) * mm, "radius": 2 * mm});
            skCircle(sketch, "E7.0.39.34", {"center": v(306.1, 244.1) * mm, "radius": 2 * mm});
            skCircle(sketch, "E7.0.39.35", {"center": v(306.1, 260.1) * mm, "radius": 2 * mm});
            skCircle(sketch, "E7.0.39.36", {"center": v(306.1, 276.1) * mm, "radius": 2 * mm});
            skCircle(sketch, "E7.0.39.37", {"center": v(306.1, 292.1) * mm, "radius": 2 * mm});
            skCircle(sketch, "E8.0.0.10", {"center": v(-309.9, -131.9) * mm, "radius": 2 * mm});
            skCircle(sketch, "E8.0.0.11", {"center": v(-309.9, -115.9) * mm, "radius": 2 * mm});
            skCircle(sketch, "E8.0.0.12", {"center": v(-309.9, -99.9) * mm, "radius": 2 * mm});
            skCircle(sketch, "E8.0.0.13", {"center": v(-309.9, -83.9) * mm, "radius": 2 * mm});
            skCircle(sketch, "E8.0.0.14", {"center": v(-309.9, -67.9) * mm, "radius": 2 * mm});
            skCircle(sketch, "E8.0.0.15", {"center": v(-309.9, -51.9) * mm, "radius": 2 * mm});
            skCircle(sketch, "E8.0.0.16", {"center": v(-309.9, -35.9) * mm, "radius": 2 * mm});
            skCircle(sketch, "E8.0.0.17", {"center": v(-309.9, -19.9) * mm, "radius": 2 * mm});
            skCircle(sketch, "E8.0.0.18", {"center": v(-309.9, -3.9) * mm, "radius": 2 * mm});
            skCircle(sketch, "E8.0.0.19", {"center": v(-309.9, 12.1) * mm, "radius": 2 * mm});
            skCircle(sketch, "E8.0.0.20", {"center": v(-309.9, 28.1) * mm, "radius": 2 * mm});
            skCircle(sketch, "E8.0.0.21", {"center": v(-309.9, 44.1) * mm, "radius": 2 * mm});
            skCircle(sketch, "E8.0.0.22", {"center": v(-309.9, 60.1) * mm, "radius": 2 * mm});
            skCircle(sketch, "E8.0.0.23", {"center": v(-309.9, 76.1) * mm, "radius": 2 * mm});
            skCircle(sketch, "E8.0.0.24", {"center": v(-309.9, 92.1) * mm, "radius": 2 * mm});
            skCircle(sketch, "E8.0.0.25", {"center": v(-309.9, 108.1) * mm, "radius": 2 * mm});
            skCircle(sketch, "E8.0.0.26", {"center": v(-309.9, 124.1) * mm, "radius": 2 * mm});
            skCircle(sketch, "E8.0.0.27", {"center": v(-309.9, 140.1) * mm, "radius": 2 * mm});
            skCircle(sketch, "E8.0.0.28", {"center": v(-309.9, 156.1) * mm, "radius": 2 * mm});
            skCircle(sketch, "E8.0.0.29", {"center": v(-309.9, 172.1) * mm, "radius": 2 * mm});
            skCircle(sketch, "E8.0.0.30", {"center": v(-309.9, 188.1) * mm, "radius": 2 * mm});
            skCircle(sketch, "E8.0.0.31", {"center": v(-309.9, 204.1) * mm, "radius": 2 * mm});
            skCircle(sketch, "E8.0.0.32", {"center": v(-309.9, 220.1) * mm, "radius": 2 * mm});
            skCircle(sketch, "E8.0.0.33", {"center": v(-309.9, 236.1) * mm, "radius": 2 * mm});
            skCircle(sketch, "E8.0.0.34", {"center": v(-309.9, 252.1) * mm, "radius": 2 * mm});
            skCircle(sketch, "E8.0.0.35", {"center": v(-309.9, 268.1) * mm, "radius": 2 * mm});
            skCircle(sketch, "E8.0.0.36", {"center": v(-309.9, 284.1) * mm, "radius": 2 * mm});
            skCircle(sketch, "E8.0.0.37", {"center": v(-309.9, 300.1) * mm, "radius": 2 * mm});
            skCircle(sketch, "E8.0.1.10", {"center": v(-293.9, -131.9) * mm, "radius": 2 * mm});
            skCircle(sketch, "E8.0.1.11", {"center": v(-293.9, -115.9) * mm, "radius": 2 * mm});
            skCircle(sketch, "E8.0.1.12", {"center": v(-293.9, -99.9) * mm, "radius": 2 * mm});
            skCircle(sketch, "E8.0.1.13", {"center": v(-293.9, -83.9) * mm, "radius": 2 * mm});
            skCircle(sketch, "E8.0.1.14", {"center": v(-293.9, -67.9) * mm, "radius": 2 * mm});
            skCircle(sketch, "E8.0.1.15", {"center": v(-293.9, -51.9) * mm, "radius": 2 * mm});
            skCircle(sketch, "E8.0.1.16", {"center": v(-293.9, -35.9) * mm, "radius": 2 * mm});
            skCircle(sketch, "E8.0.1.17", {"center": v(-293.9, -19.9) * mm, "radius": 2 * mm});
            skCircle(sketch, "E8.0.1.18", {"center": v(-293.9, -3.9) * mm, "radius": 2 * mm});
            skCircle(sketch, "E8.0.1.19", {"center": v(-293.9, 12.1) * mm, "radius": 2 * mm});
            skCircle(sketch, "E8.0.1.20", {"center": v(-293.9, 28.1) * mm, "radius": 2 * mm});
            skCircle(sketch, "E8.0.1.21", {"center": v(-293.9, 44.1) * mm, "radius": 2 * mm});
            skCircle(sketch, "E8.0.1.22", {"center": v(-293.9, 60.1) * mm, "radius": 2 * mm});
            skCircle(sketch, "E8.0.1.23", {"center": v(-293.9, 76.1) * mm, "radius": 2 * mm});
            skCircle(sketch, "E8.0.1.24", {"center": v(-293.9, 92.1) * mm, "radius": 2 * mm});
            skCircle(sketch, "E8.0.1.25", {"center": v(-293.9, 108.1) * mm, "radius": 2 * mm});
            skCircle(sketch, "E8.0.1.26", {"center": v(-293.9, 124.1) * mm, "radius": 2 * mm});
            skCircle(sketch, "E8.0.1.27", {"center": v(-293.9, 140.1) * mm, "radius": 2 * mm});
            skCircle(sketch, "E8.0.1.28", {"center": v(-293.9, 156.1) * mm, "radius": 2 * mm});
            skCircle(sketch, "E8.0.1.29", {"center": v(-293.9, 172.1) * mm, "radius": 2 * mm});
            skCircle(sketch, "E8.0.1.30", {"center": v(-293.9, 188.1) * mm, "radius": 2 * mm});
            skCircle(sketch, "E8.0.1.31", {"center": v(-293.9, 204.1) * mm, "radius": 2 * mm});
            skCircle(sketch, "E8.0.1.32", {"center": v(-293.9, 220.1) * mm, "radius": 2 * mm});
            skCircle(sketch, "E8.0.1.33", {"center": v(-293.9, 236.1) * mm, "radius": 2 * mm});
            skCircle(sketch, "E8.0.1.34", {"center": v(-293.9, 252.1) * mm, "radius": 2 * mm});
            skCircle(sketch, "E8.0.1.35", {"center": v(-293.9, 268.1) * mm, "radius": 2 * mm});
            skCircle(sketch, "E8.0.1.36", {"center": v(-293.9, 284.1) * mm, "radius": 2 * mm});
            skCircle(sketch, "E8.0.1.37", {"center": v(-293.9, 300.1) * mm, "radius": 2 * mm});
            skCircle(sketch, "E8.0.2.10", {"center": v(-277.9, -131.9) * mm, "radius": 2 * mm});
            skCircle(sketch, "E8.0.2.11", {"center": v(-277.9, -115.9) * mm, "radius": 2 * mm});
            skCircle(sketch, "E8.0.2.12", {"center": v(-277.9, -99.9) * mm, "radius": 2 * mm});
            skCircle(sketch, "E8.0.2.13", {"center": v(-277.9, -83.9) * mm, "radius": 2 * mm});
            skCircle(sketch, "E8.0.2.14", {"center": v(-277.9, -67.9) * mm, "radius": 2 * mm});
            skCircle(sketch, "E8.0.2.15", {"center": v(-277.9, -51.9) * mm, "radius": 2 * mm});
            skCircle(sketch, "E8.0.2.16", {"center": v(-277.9, -35.9) * mm, "radius": 2 * mm});
            skCircle(sketch, "E8.0.2.17", {"center": v(-277.9, -19.9) * mm, "radius": 2 * mm});
            skCircle(sketch, "E8.0.2.18", {"center": v(-277.9, -3.9) * mm, "radius": 2 * mm});
            skCircle(sketch, "E8.0.2.19", {"center": v(-277.9, 12.1) * mm, "radius": 2 * mm});
            skCircle(sketch, "E8.0.2.20", {"center": v(-277.9, 28.1) * mm, "radius": 2 * mm});
            skCircle(sketch, "E8.0.2.21", {"center": v(-277.9, 44.1) * mm, "radius": 2 * mm});
            skCircle(sketch, "E8.0.2.22", {"center": v(-277.9, 60.1) * mm, "radius": 2 * mm});
            skCircle(sketch, "E8.0.2.23", {"center": v(-277.9, 76.1) * mm, "radius": 2 * mm});
            skCircle(sketch, "E8.0.2.24", {"center": v(-277.9, 92.1) * mm, "radius": 2 * mm});
            skCircle(sketch, "E8.0.2.25", {"center": v(-277.9, 108.1) * mm, "radius": 2 * mm});
            skCircle(sketch, "E8.0.2.26", {"center": v(-277.9, 124.1) * mm, "radius": 2 * mm});
            skCircle(sketch, "E8.0.2.27", {"center": v(-277.9, 140.1) * mm, "radius": 2 * mm});
            skCircle(sketch, "E8.0.2.28", {"center": v(-277.9, 156.1) * mm, "radius": 2 * mm});
            skCircle(sketch, "E8.0.2.29", {"center": v(-277.9, 172.1) * mm, "radius": 2 * mm});
            skCircle(sketch, "E8.0.2.30", {"center": v(-277.9, 188.1) * mm, "radius": 2 * mm});
            skCircle(sketch, "E8.0.2.31", {"center": v(-277.9, 204.1) * mm, "radius": 2 * mm});
            skCircle(sketch, "E8.0.2.32", {"center": v(-277.9, 220.1) * mm, "radius": 2 * mm});
            skCircle(sketch, "E8.0.2.33", {"center": v(-277.9, 236.1) * mm, "radius": 2 * mm});
            skCircle(sketch, "E8.0.2.34", {"center": v(-277.9, 252.1) * mm, "radius": 2 * mm});
            skCircle(sketch, "E8.0.2.35", {"center": v(-277.9, 268.1) * mm, "radius": 2 * mm});
            skCircle(sketch, "E8.0.2.36", {"center": v(-277.9, 284.1) * mm, "radius": 2 * mm});
            skCircle(sketch, "E8.0.2.37", {"center": v(-277.9, 300.1) * mm, "radius": 2 * mm});
            skCircle(sketch, "E8.0.3.10", {"center": v(-261.9, -131.9) * mm, "radius": 2 * mm});
            skCircle(sketch, "E8.0.3.11", {"center": v(-261.9, -115.9) * mm, "radius": 2 * mm});
            skCircle(sketch, "E8.0.3.12", {"center": v(-261.9, -99.9) * mm, "radius": 2 * mm});
            skCircle(sketch, "E8.0.3.13", {"center": v(-261.9, -83.9) * mm, "radius": 2 * mm});
            skCircle(sketch, "E8.0.3.14", {"center": v(-261.9, -67.9) * mm, "radius": 2 * mm});
            skCircle(sketch, "E8.0.3.15", {"center": v(-261.9, -51.9) * mm, "radius": 2 * mm});
            skCircle(sketch, "E8.0.3.16", {"center": v(-261.9, -35.9) * mm, "radius": 2 * mm});
            skCircle(sketch, "E8.0.3.17", {"center": v(-261.9, -19.9) * mm, "radius": 2 * mm});
            skCircle(sketch, "E8.0.3.18", {"center": v(-261.9, -3.9) * mm, "radius": 2 * mm});
            skCircle(sketch, "E8.0.3.19", {"center": v(-261.9, 12.1) * mm, "radius": 2 * mm});
            skCircle(sketch, "E8.0.3.20", {"center": v(-261.9, 28.1) * mm, "radius": 2 * mm});
            skCircle(sketch, "E8.0.3.21", {"center": v(-261.9, 44.1) * mm, "radius": 2 * mm});
            skCircle(sketch, "E8.0.3.22", {"center": v(-261.9, 60.1) * mm, "radius": 2 * mm});
            skCircle(sketch, "E8.0.3.23", {"center": v(-261.9, 76.1) * mm, "radius": 2 * mm});
            skCircle(sketch, "E8.0.3.24", {"center": v(-261.9, 92.1) * mm, "radius": 2 * mm});
            skCircle(sketch, "E8.0.3.25", {"center": v(-261.9, 108.1) * mm, "radius": 2 * mm});
            skCircle(sketch, "E8.0.3.26", {"center": v(-261.9, 124.1) * mm, "radius": 2 * mm});
            skCircle(sketch, "E8.0.3.27", {"center": v(-261.9, 140.1) * mm, "radius": 2 * mm});
            skCircle(sketch, "E8.0.3.28", {"center": v(-261.9, 156.1) * mm, "radius": 2 * mm});
            skCircle(sketch, "E8.0.3.29", {"center": v(-261.9, 172.1) * mm, "radius": 2 * mm});
            skCircle(sketch, "E8.0.3.30", {"center": v(-261.9, 188.1) * mm, "radius": 2 * mm});
            skCircle(sketch, "E8.0.3.31", {"center": v(-261.9, 204.1) * mm, "radius": 2 * mm});
            skCircle(sketch, "E8.0.3.32", {"center": v(-261.9, 220.1) * mm, "radius": 2 * mm});
            skCircle(sketch, "E8.0.3.33", {"center": v(-261.9, 236.1) * mm, "radius": 2 * mm});
            skCircle(sketch, "E8.0.3.34", {"center": v(-261.9, 252.1) * mm, "radius": 2 * mm});
            skCircle(sketch, "E8.0.3.35", {"center": v(-261.9, 268.1) * mm, "radius": 2 * mm});
            skCircle(sketch, "E8.0.3.36", {"center": v(-261.9, 284.1) * mm, "radius": 2 * mm});
            skCircle(sketch, "E8.0.3.37", {"center": v(-261.9, 300.1) * mm, "radius": 2 * mm});
            skCircle(sketch, "E8.0.4.10", {"center": v(-245.9, -131.9) * mm, "radius": 2 * mm});
            skCircle(sketch, "E8.0.4.11", {"center": v(-245.9, -115.9) * mm, "radius": 2 * mm});
            skCircle(sketch, "E8.0.4.12", {"center": v(-245.9, -99.9) * mm, "radius": 2 * mm});
            skCircle(sketch, "E8.0.4.13", {"center": v(-245.9, -83.9) * mm, "radius": 2 * mm});
            skCircle(sketch, "E8.0.4.14", {"center": v(-245.9, -67.9) * mm, "radius": 2 * mm});
            skCircle(sketch, "E8.0.4.15", {"center": v(-245.9, -51.9) * mm, "radius": 2 * mm});
            skCircle(sketch, "E8.0.4.16", {"center": v(-245.9, -35.9) * mm, "radius": 2 * mm});
            skCircle(sketch, "E8.0.4.17", {"center": v(-245.9, -19.9) * mm, "radius": 2 * mm});
            skCircle(sketch, "E8.0.4.18", {"center": v(-245.9, -3.9) * mm, "radius": 2 * mm});
            skCircle(sketch, "E8.0.4.19", {"center": v(-245.9, 12.1) * mm, "radius": 2 * mm});
            skCircle(sketch, "E8.0.4.20", {"center": v(-245.9, 28.1) * mm, "radius": 2 * mm});
            skCircle(sketch, "E8.0.4.21", {"center": v(-245.9, 44.1) * mm, "radius": 2 * mm});
            skCircle(sketch, "E8.0.4.22", {"center": v(-245.9, 60.1) * mm, "radius": 2 * mm});
            skCircle(sketch, "E8.0.4.23", {"center": v(-245.9, 76.1) * mm, "radius": 2 * mm});
            skCircle(sketch, "E8.0.4.24", {"center": v(-245.9, 92.1) * mm, "radius": 2 * mm});
            skCircle(sketch, "E8.0.4.25", {"center": v(-245.9, 108.1) * mm, "radius": 2 * mm});
            skCircle(sketch, "E8.0.4.26", {"center": v(-245.9, 124.1) * mm, "radius": 2 * mm});
            skCircle(sketch, "E8.0.4.27", {"center": v(-245.9, 140.1) * mm, "radius": 2 * mm});
            skCircle(sketch, "E8.0.4.28", {"center": v(-245.9, 156.1) * mm, "radius": 2 * mm});
            skCircle(sketch, "E8.0.4.29", {"center": v(-245.9, 172.1) * mm, "radius": 2 * mm});
            skCircle(sketch, "E8.0.4.30", {"center": v(-245.9, 188.1) * mm, "radius": 2 * mm});
            skCircle(sketch, "E8.0.4.31", {"center": v(-245.9, 204.1) * mm, "radius": 2 * mm});
            skCircle(sketch, "E8.0.4.32", {"center": v(-245.9, 220.1) * mm, "radius": 2 * mm});
            skCircle(sketch, "E8.0.4.33", {"center": v(-245.9, 236.1) * mm, "radius": 2 * mm});
            skCircle(sketch, "E8.0.4.34", {"center": v(-245.9, 252.1) * mm, "radius": 2 * mm});
            skCircle(sketch, "E8.0.4.35", {"center": v(-245.9, 268.1) * mm, "radius": 2 * mm});
            skCircle(sketch, "E8.0.4.36", {"center": v(-245.9, 284.1) * mm, "radius": 2 * mm});
            skCircle(sketch, "E8.0.4.37", {"center": v(-245.9, 300.1) * mm, "radius": 2 * mm});
            skCircle(sketch, "E8.0.5.10", {"center": v(-229.9, -131.9) * mm, "radius": 2 * mm});
            skCircle(sketch, "E8.0.5.11", {"center": v(-229.9, -115.9) * mm, "radius": 2 * mm});
            skCircle(sketch, "E8.0.5.12", {"center": v(-229.9, -99.9) * mm, "radius": 2 * mm});
            skCircle(sketch, "E8.0.5.13", {"center": v(-229.9, -83.9) * mm, "radius": 2 * mm});
            skCircle(sketch, "E8.0.5.14", {"center": v(-229.9, -67.9) * mm, "radius": 2 * mm});
            skCircle(sketch, "E8.0.5.15", {"center": v(-229.9, -51.9) * mm, "radius": 2 * mm});
            skCircle(sketch, "E8.0.5.16", {"center": v(-229.9, -35.9) * mm, "radius": 2 * mm});
            skCircle(sketch, "E8.0.5.17", {"center": v(-229.9, -19.9) * mm, "radius": 2 * mm});
            skCircle(sketch, "E8.0.5.18", {"center": v(-229.9, -3.9) * mm, "radius": 2 * mm});
            skCircle(sketch, "E8.0.5.19", {"center": v(-229.9, 12.1) * mm, "radius": 2 * mm});
            skCircle(sketch, "E8.0.5.20", {"center": v(-229.9, 28.1) * mm, "radius": 2 * mm});
            skCircle(sketch, "E8.0.5.21", {"center": v(-229.9, 44.1) * mm, "radius": 2 * mm});
            skCircle(sketch, "E8.0.5.22", {"center": v(-229.9, 60.1) * mm, "radius": 2 * mm});
            skCircle(sketch, "E8.0.5.23", {"center": v(-229.9, 76.1) * mm, "radius": 2 * mm});
            skCircle(sketch, "E8.0.5.24", {"center": v(-229.9, 92.1) * mm, "radius": 2 * mm});
            skCircle(sketch, "E8.0.5.25", {"center": v(-229.9, 108.1) * mm, "radius": 2 * mm});
            skCircle(sketch, "E8.0.5.26", {"center": v(-229.9, 124.1) * mm, "radius": 2 * mm});
            skCircle(sketch, "E8.0.5.27", {"center": v(-229.9, 140.1) * mm, "radius": 2 * mm});
            skCircle(sketch, "E8.0.5.28", {"center": v(-229.9, 156.1) * mm, "radius": 2 * mm});
            skCircle(sketch, "E8.0.5.29", {"center": v(-229.9, 172.1) * mm, "radius": 2 * mm});
            skCircle(sketch, "E8.0.5.30", {"center": v(-229.9, 188.1) * mm, "radius": 2 * mm});
            skCircle(sketch, "E8.0.5.31", {"center": v(-229.9, 204.1) * mm, "radius": 2 * mm});
            skCircle(sketch, "E8.0.5.32", {"center": v(-229.9, 220.1) * mm, "radius": 2 * mm});
            skCircle(sketch, "E8.0.5.33", {"center": v(-229.9, 236.1) * mm, "radius": 2 * mm});
            skCircle(sketch, "E8.0.5.34", {"center": v(-229.9, 252.1) * mm, "radius": 2 * mm});
            skCircle(sketch, "E8.0.5.35", {"center": v(-229.9, 268.1) * mm, "radius": 2 * mm});
            skCircle(sketch, "E8.0.5.36", {"center": v(-229.9, 284.1) * mm, "radius": 2 * mm});
            skCircle(sketch, "E8.0.5.37", {"center": v(-229.9, 300.1) * mm, "radius": 2 * mm});
            skCircle(sketch, "E8.0.6.10", {"center": v(-213.9, -131.9) * mm, "radius": 2 * mm});
            skCircle(sketch, "E8.0.6.11", {"center": v(-213.9, -115.9) * mm, "radius": 2 * mm});
            skCircle(sketch, "E8.0.6.12", {"center": v(-213.9, -99.9) * mm, "radius": 2 * mm});
            skCircle(sketch, "E8.0.6.13", {"center": v(-213.9, -83.9) * mm, "radius": 2 * mm});
            skCircle(sketch, "E8.0.6.14", {"center": v(-213.9, -67.9) * mm, "radius": 2 * mm});
            skCircle(sketch, "E8.0.6.15", {"center": v(-213.9, -51.9) * mm, "radius": 2 * mm});
            skCircle(sketch, "E8.0.6.16", {"center": v(-213.9, -35.9) * mm, "radius": 2 * mm});
            skCircle(sketch, "E8.0.6.17", {"center": v(-213.9, -19.9) * mm, "radius": 2 * mm});
            skCircle(sketch, "E8.0.6.18", {"center": v(-213.9, -3.9) * mm, "radius": 2 * mm});
            skCircle(sketch, "E8.0.6.19", {"center": v(-213.9, 12.1) * mm, "radius": 2 * mm});
            skCircle(sketch, "E8.0.6.20", {"center": v(-213.9, 28.1) * mm, "radius": 2 * mm});
            skCircle(sketch, "E8.0.6.21", {"center": v(-213.9, 44.1) * mm, "radius": 2 * mm});
            skCircle(sketch, "E8.0.6.22", {"center": v(-213.9, 60.1) * mm, "radius": 2 * mm});
            skCircle(sketch, "E8.0.6.23", {"center": v(-213.9, 76.1) * mm, "radius": 2 * mm});
            skCircle(sketch, "E8.0.6.24", {"center": v(-213.9, 92.1) * mm, "radius": 2 * mm});
            skCircle(sketch, "E8.0.6.25", {"center": v(-213.9, 108.1) * mm, "radius": 2 * mm});
            skCircle(sketch, "E8.0.6.26", {"center": v(-213.9, 124.1) * mm, "radius": 2 * mm});
            skCircle(sketch, "E8.0.6.27", {"center": v(-213.9, 140.1) * mm, "radius": 2 * mm});
            skCircle(sketch, "E8.0.6.28", {"center": v(-213.9, 156.1) * mm, "radius": 2 * mm});
            skCircle(sketch, "E8.0.6.29", {"center": v(-213.9, 172.1) * mm, "radius": 2 * mm});
            skCircle(sketch, "E8.0.6.30", {"center": v(-213.9, 188.1) * mm, "radius": 2 * mm});
            skCircle(sketch, "E8.0.6.31", {"center": v(-213.9, 204.1) * mm, "radius": 2 * mm});
            skCircle(sketch, "E8.0.6.32", {"center": v(-213.9, 220.1) * mm, "radius": 2 * mm});
            skCircle(sketch, "E8.0.6.33", {"center": v(-213.9, 236.1) * mm, "radius": 2 * mm});
            skCircle(sketch, "E8.0.6.34", {"center": v(-213.9, 252.1) * mm, "radius": 2 * mm});
            skCircle(sketch, "E8.0.6.35", {"center": v(-213.9, 268.1) * mm, "radius": 2 * mm});
            skCircle(sketch, "E8.0.6.36", {"center": v(-213.9, 284.1) * mm, "radius": 2 * mm});
            skCircle(sketch, "E8.0.6.37", {"center": v(-213.9, 300.1) * mm, "radius": 2 * mm});
            skCircle(sketch, "E8.0.7.10", {"center": v(-197.9, -131.9) * mm, "radius": 2 * mm});
            skCircle(sketch, "E8.0.7.11", {"center": v(-197.9, -115.9) * mm, "radius": 2 * mm});
            skCircle(sketch, "E8.0.7.12", {"center": v(-197.9, -99.9) * mm, "radius": 2 * mm});
            skCircle(sketch, "E8.0.7.13", {"center": v(-197.9, -83.9) * mm, "radius": 2 * mm});
            skCircle(sketch, "E8.0.7.14", {"center": v(-197.9, -67.9) * mm, "radius": 2 * mm});
            skCircle(sketch, "E8.0.7.15", {"center": v(-197.9, -51.9) * mm, "radius": 2 * mm});
            skCircle(sketch, "E8.0.7.16", {"center": v(-197.9, -35.9) * mm, "radius": 2 * mm});
            skCircle(sketch, "E8.0.7.17", {"center": v(-197.9, -19.9) * mm, "radius": 2 * mm});
            skCircle(sketch, "E8.0.7.18", {"center": v(-197.9, -3.9) * mm, "radius": 2 * mm});
            skCircle(sketch, "E8.0.7.19", {"center": v(-197.9, 12.1) * mm, "radius": 2 * mm});
            skCircle(sketch, "E8.0.7.20", {"center": v(-197.9, 28.1) * mm, "radius": 2 * mm});
            skCircle(sketch, "E8.0.7.21", {"center": v(-197.9, 44.1) * mm, "radius": 2 * mm});
            skCircle(sketch, "E8.0.7.22", {"center": v(-197.9, 60.1) * mm, "radius": 2 * mm});
            skCircle(sketch, "E8.0.7.23", {"center": v(-197.9, 76.1) * mm, "radius": 2 * mm});
            skCircle(sketch, "E8.0.7.24", {"center": v(-197.9, 92.1) * mm, "radius": 2 * mm});
            skCircle(sketch, "E8.0.7.25", {"center": v(-197.9, 108.1) * mm, "radius": 2 * mm});
            skCircle(sketch, "E8.0.7.26", {"center": v(-197.9, 124.1) * mm, "radius": 2 * mm});
            skCircle(sketch, "E8.0.7.27", {"center": v(-197.9, 140.1) * mm, "radius": 2 * mm});
            skCircle(sketch, "E8.0.7.28", {"center": v(-197.9, 156.1) * mm, "radius": 2 * mm});
            skCircle(sketch, "E8.0.7.29", {"center": v(-197.9, 172.1) * mm, "radius": 2 * mm});
            skCircle(sketch, "E8.0.7.30", {"center": v(-197.9, 188.1) * mm, "radius": 2 * mm});
            skCircle(sketch, "E8.0.7.31", {"center": v(-197.9, 204.1) * mm, "radius": 2 * mm});
            skCircle(sketch, "E8.0.7.32", {"center": v(-197.9, 220.1) * mm, "radius": 2 * mm});
            skCircle(sketch, "E8.0.7.33", {"center": v(-197.9, 236.1) * mm, "radius": 2 * mm});
            skCircle(sketch, "E8.0.7.34", {"center": v(-197.9, 252.1) * mm, "radius": 2 * mm});
            skCircle(sketch, "E8.0.7.35", {"center": v(-197.9, 268.1) * mm, "radius": 2 * mm});
            skCircle(sketch, "E8.0.7.36", {"center": v(-197.9, 284.1) * mm, "radius": 2 * mm});
            skCircle(sketch, "E8.0.7.37", {"center": v(-197.9, 300.1) * mm, "radius": 2 * mm});
            skCircle(sketch, "E8.0.8.10", {"center": v(-181.9, -131.9) * mm, "radius": 2 * mm});
            skCircle(sketch, "E8.0.8.11", {"center": v(-181.9, -115.9) * mm, "radius": 2 * mm});
            skCircle(sketch, "E8.0.8.12", {"center": v(-181.9, -99.9) * mm, "radius": 2 * mm});
            skCircle(sketch, "E8.0.8.13", {"center": v(-181.9, -83.9) * mm, "radius": 2 * mm});
            skCircle(sketch, "E8.0.8.14", {"center": v(-181.9, -67.9) * mm, "radius": 2 * mm});
            skCircle(sketch, "E8.0.8.15", {"center": v(-181.9, -51.9) * mm, "radius": 2 * mm});
            skCircle(sketch, "E8.0.8.16", {"center": v(-181.9, -35.9) * mm, "radius": 2 * mm});
            skCircle(sketch, "E8.0.8.17", {"center": v(-181.9, -19.9) * mm, "radius": 2 * mm});
            skCircle(sketch, "E8.0.8.18", {"center": v(-181.9, -3.9) * mm, "radius": 2 * mm});
            skCircle(sketch, "E8.0.8.19", {"center": v(-181.9, 12.1) * mm, "radius": 2 * mm});
            skCircle(sketch, "E8.0.8.20", {"center": v(-181.9, 28.1) * mm, "radius": 2 * mm});
            skCircle(sketch, "E8.0.8.21", {"center": v(-181.9, 44.1) * mm, "radius": 2 * mm});
            skCircle(sketch, "E8.0.8.22", {"center": v(-181.9, 60.1) * mm, "radius": 2 * mm});
            skCircle(sketch, "E8.0.8.23", {"center": v(-181.9, 76.1) * mm, "radius": 2 * mm});
            skCircle(sketch, "E8.0.8.24", {"center": v(-181.9, 92.1) * mm, "radius": 2 * mm});
            skCircle(sketch, "E8.0.8.25", {"center": v(-181.9, 108.1) * mm, "radius": 2 * mm});
            skCircle(sketch, "E8.0.8.26", {"center": v(-181.9, 124.1) * mm, "radius": 2 * mm});
            skCircle(sketch, "E8.0.8.27", {"center": v(-181.9, 140.1) * mm, "radius": 2 * mm});
            skCircle(sketch, "E8.0.8.28", {"center": v(-181.9, 156.1) * mm, "radius": 2 * mm});
            skCircle(sketch, "E8.0.8.29", {"center": v(-181.9, 172.1) * mm, "radius": 2 * mm});
            skCircle(sketch, "E8.0.8.30", {"center": v(-181.9, 188.1) * mm, "radius": 2 * mm});
            skCircle(sketch, "E8.0.8.31", {"center": v(-181.9, 204.1) * mm, "radius": 2 * mm});
            skCircle(sketch, "E8.0.8.32", {"center": v(-181.9, 220.1) * mm, "radius": 2 * mm});
            skCircle(sketch, "E8.0.8.33", {"center": v(-181.9, 236.1) * mm, "radius": 2 * mm});
            skCircle(sketch, "E8.0.8.34", {"center": v(-181.9, 252.1) * mm, "radius": 2 * mm});
            skCircle(sketch, "E8.0.8.35", {"center": v(-181.9, 268.1) * mm, "radius": 2 * mm});
            skCircle(sketch, "E8.0.8.36", {"center": v(-181.9, 284.1) * mm, "radius": 2 * mm});
            skCircle(sketch, "E8.0.8.37", {"center": v(-181.9, 300.1) * mm, "radius": 2 * mm});
            skCircle(sketch, "E8.0.9.10", {"center": v(-165.9, -131.9) * mm, "radius": 2 * mm});
            skCircle(sketch, "E8.0.9.11", {"center": v(-165.9, -115.9) * mm, "radius": 2 * mm});
            skCircle(sketch, "E8.0.9.12", {"center": v(-165.9, -99.9) * mm, "radius": 2 * mm});
            skCircle(sketch, "E8.0.9.13", {"center": v(-165.9, -83.9) * mm, "radius": 2 * mm});
            skCircle(sketch, "E8.0.9.14", {"center": v(-165.9, -67.9) * mm, "radius": 2 * mm});
            skCircle(sketch, "E8.0.9.15", {"center": v(-165.9, -51.9) * mm, "radius": 2 * mm});
            skCircle(sketch, "E8.0.9.16", {"center": v(-165.9, -35.9) * mm, "radius": 2 * mm});
            skCircle(sketch, "E8.0.9.17", {"center": v(-165.9, -19.9) * mm, "radius": 2 * mm});
            skCircle(sketch, "E8.0.9.18", {"center": v(-165.9, -3.9) * mm, "radius": 2 * mm});
            skCircle(sketch, "E8.0.9.19", {"center": v(-165.9, 12.1) * mm, "radius": 2 * mm});
            skCircle(sketch, "E8.0.9.20", {"center": v(-165.9, 28.1) * mm, "radius": 2 * mm});
            skCircle(sketch, "E8.0.9.21", {"center": v(-165.9, 44.1) * mm, "radius": 2 * mm});
            skCircle(sketch, "E8.0.9.22", {"center": v(-165.9, 60.1) * mm, "radius": 2 * mm});
            skCircle(sketch, "E8.0.9.23", {"center": v(-165.9, 76.1) * mm, "radius": 2 * mm});
            skCircle(sketch, "E8.0.9.24", {"center": v(-165.9, 92.1) * mm, "radius": 2 * mm});
            skCircle(sketch, "E8.0.9.25", {"center": v(-165.9, 108.1) * mm, "radius": 2 * mm});
            skCircle(sketch, "E8.0.9.26", {"center": v(-165.9, 124.1) * mm, "radius": 2 * mm});
            skCircle(sketch, "E8.0.9.27", {"center": v(-165.9, 140.1) * mm, "radius": 2 * mm});
            skCircle(sketch, "E8.0.9.28", {"center": v(-165.9, 156.1) * mm, "radius": 2 * mm});
            skCircle(sketch, "E8.0.9.29", {"center": v(-165.9, 172.1) * mm, "radius": 2 * mm});
            skCircle(sketch, "E8.0.9.30", {"center": v(-165.9, 188.1) * mm, "radius": 2 * mm});
            skCircle(sketch, "E8.0.9.31", {"center": v(-165.9, 204.1) * mm, "radius": 2 * mm});
            skCircle(sketch, "E8.0.9.32", {"center": v(-165.9, 220.1) * mm, "radius": 2 * mm});
            skCircle(sketch, "E8.0.9.33", {"center": v(-165.9, 236.1) * mm, "radius": 2 * mm});
            skCircle(sketch, "E8.0.9.34", {"center": v(-165.9, 252.1) * mm, "radius": 2 * mm});
            skCircle(sketch, "E8.0.9.35", {"center": v(-165.9, 268.1) * mm, "radius": 2 * mm});
            skCircle(sketch, "E8.0.9.36", {"center": v(-165.9, 284.1) * mm, "radius": 2 * mm});
            skCircle(sketch, "E8.0.9.37", {"center": v(-165.9, 300.1) * mm, "radius": 2 * mm});
            skCircle(sketch, "E8.0.10.10", {"center": v(-149.9, -131.9) * mm, "radius": 2 * mm});
            skCircle(sketch, "E8.0.10.11", {"center": v(-149.9, -115.9) * mm, "radius": 2 * mm});
            skCircle(sketch, "E8.0.10.12", {"center": v(-149.9, -99.9) * mm, "radius": 2 * mm});
            skCircle(sketch, "E8.0.10.13", {"center": v(-149.9, -83.9) * mm, "radius": 2 * mm});
            skCircle(sketch, "E8.0.10.14", {"center": v(-149.9, -67.9) * mm, "radius": 2 * mm});
            skCircle(sketch, "E8.0.10.15", {"center": v(-149.9, -51.9) * mm, "radius": 2 * mm});
            skCircle(sketch, "E8.0.10.16", {"center": v(-149.9, -35.9) * mm, "radius": 2 * mm});
            skCircle(sketch, "E8.0.10.17", {"center": v(-149.9, -19.9) * mm, "radius": 2 * mm});
            skCircle(sketch, "E8.0.10.18", {"center": v(-149.9, -3.9) * mm, "radius": 2 * mm});
            skCircle(sketch, "E8.0.10.19", {"center": v(-149.9, 12.1) * mm, "radius": 2 * mm});
            skCircle(sketch, "E8.0.10.20", {"center": v(-149.9, 28.1) * mm, "radius": 2 * mm});
            skCircle(sketch, "E8.0.10.21", {"center": v(-149.9, 44.1) * mm, "radius": 2 * mm});
            skCircle(sketch, "E8.0.10.22", {"center": v(-149.9, 60.1) * mm, "radius": 2 * mm});
            skCircle(sketch, "E8.0.10.23", {"center": v(-149.9, 76.1) * mm, "radius": 2 * mm});
            skCircle(sketch, "E8.0.10.24", {"center": v(-149.9, 92.1) * mm, "radius": 2 * mm});
            skCircle(sketch, "E8.0.10.25", {"center": v(-149.9, 108.1) * mm, "radius": 2 * mm});
            skCircle(sketch, "E8.0.10.26", {"center": v(-149.9, 124.1) * mm, "radius": 2 * mm});
            skCircle(sketch, "E8.0.10.27", {"center": v(-149.9, 140.1) * mm, "radius": 2 * mm});
            skCircle(sketch, "E8.0.10.28", {"center": v(-149.9, 156.1) * mm, "radius": 2 * mm});
            skCircle(sketch, "E8.0.10.29", {"center": v(-149.9, 172.1) * mm, "radius": 2 * mm});
            skCircle(sketch, "E8.0.10.30", {"center": v(-149.9, 188.1) * mm, "radius": 2 * mm});
            skCircle(sketch, "E8.0.10.31", {"center": v(-149.9, 204.1) * mm, "radius": 2 * mm});
            skCircle(sketch, "E8.0.10.32", {"center": v(-149.9, 220.1) * mm, "radius": 2 * mm});
            skCircle(sketch, "E8.0.10.33", {"center": v(-149.9, 236.1) * mm, "radius": 2 * mm});
            skCircle(sketch, "E8.0.10.34", {"center": v(-149.9, 252.1) * mm, "radius": 2 * mm});
            skCircle(sketch, "E8.0.10.35", {"center": v(-149.9, 268.1) * mm, "radius": 2 * mm});
            skCircle(sketch, "E8.0.10.36", {"center": v(-149.9, 284.1) * mm, "radius": 2 * mm});
            skCircle(sketch, "E8.0.10.37", {"center": v(-149.9, 300.1) * mm, "radius": 2 * mm});
            skCircle(sketch, "E8.0.11.10", {"center": v(-133.9, -131.9) * mm, "radius": 2 * mm});
            skCircle(sketch, "E8.0.11.11", {"center": v(-133.9, -115.9) * mm, "radius": 2 * mm});
            skCircle(sketch, "E8.0.11.12", {"center": v(-133.9, -99.9) * mm, "radius": 2 * mm});
            skCircle(sketch, "E8.0.11.13", {"center": v(-133.9, -83.9) * mm, "radius": 2 * mm});
            skCircle(sketch, "E8.0.11.14", {"center": v(-133.9, -67.9) * mm, "radius": 2 * mm});
            skCircle(sketch, "E8.0.11.15", {"center": v(-133.9, -51.9) * mm, "radius": 2 * mm});
            skCircle(sketch, "E8.0.11.16", {"center": v(-133.9, -35.9) * mm, "radius": 2 * mm});
            skCircle(sketch, "E8.0.11.17", {"center": v(-133.9, -19.9) * mm, "radius": 2 * mm});
            skCircle(sketch, "E8.0.11.18", {"center": v(-133.9, -3.9) * mm, "radius": 2 * mm});
            skCircle(sketch, "E8.0.11.19", {"center": v(-133.9, 12.1) * mm, "radius": 2 * mm});
            skCircle(sketch, "E8.0.11.20", {"center": v(-133.9, 28.1) * mm, "radius": 2 * mm});
            skCircle(sketch, "E8.0.11.21", {"center": v(-133.9, 44.1) * mm, "radius": 2 * mm});
            skCircle(sketch, "E8.0.11.22", {"center": v(-133.9, 60.1) * mm, "radius": 2 * mm});
            skCircle(sketch, "E8.0.11.23", {"center": v(-133.9, 76.1) * mm, "radius": 2 * mm});
            skCircle(sketch, "E8.0.11.24", {"center": v(-133.9, 92.1) * mm, "radius": 2 * mm});
            skCircle(sketch, "E8.0.11.25", {"center": v(-133.9, 108.1) * mm, "radius": 2 * mm});
            skCircle(sketch, "E8.0.11.26", {"center": v(-133.9, 124.1) * mm, "radius": 2 * mm});
            skCircle(sketch, "E8.0.11.27", {"center": v(-133.9, 140.1) * mm, "radius": 2 * mm});
            skCircle(sketch, "E8.0.11.28", {"center": v(-133.9, 156.1) * mm, "radius": 2 * mm});
            skCircle(sketch, "E8.0.11.29", {"center": v(-133.9, 172.1) * mm, "radius": 2 * mm});
            skCircle(sketch, "E8.0.11.30", {"center": v(-133.9, 188.1) * mm, "radius": 2 * mm});
            skCircle(sketch, "E8.0.11.31", {"center": v(-133.9, 204.1) * mm, "radius": 2 * mm});
            skCircle(sketch, "E8.0.11.32", {"center": v(-133.9, 220.1) * mm, "radius": 2 * mm});
            skCircle(sketch, "E8.0.11.33", {"center": v(-133.9, 236.1) * mm, "radius": 2 * mm});
            skCircle(sketch, "E8.0.11.34", {"center": v(-133.9, 252.1) * mm, "radius": 2 * mm});
            skCircle(sketch, "E8.0.11.35", {"center": v(-133.9, 268.1) * mm, "radius": 2 * mm});
            skCircle(sketch, "E8.0.11.36", {"center": v(-133.9, 284.1) * mm, "radius": 2 * mm});
            skCircle(sketch, "E8.0.11.37", {"center": v(-133.9, 300.1) * mm, "radius": 2 * mm});
            skCircle(sketch, "E8.0.12.10", {"center": v(-117.9, -131.9) * mm, "radius": 2 * mm});
            skCircle(sketch, "E8.0.12.11", {"center": v(-117.9, -115.9) * mm, "radius": 2 * mm});
            skCircle(sketch, "E8.0.12.12", {"center": v(-117.9, -99.9) * mm, "radius": 2 * mm});
            skCircle(sketch, "E8.0.12.13", {"center": v(-117.9, -83.9) * mm, "radius": 2 * mm});
            skCircle(sketch, "E8.0.12.14", {"center": v(-117.9, -67.9) * mm, "radius": 2 * mm});
            skCircle(sketch, "E8.0.12.15", {"center": v(-117.9, -51.9) * mm, "radius": 2 * mm});
            skCircle(sketch, "E8.0.12.16", {"center": v(-117.9, -35.9) * mm, "radius": 2 * mm});
            skCircle(sketch, "E8.0.12.17", {"center": v(-117.9, -19.9) * mm, "radius": 2 * mm});
            skCircle(sketch, "E8.0.12.18", {"center": v(-117.9, -3.9) * mm, "radius": 2 * mm});
            skCircle(sketch, "E8.0.12.19", {"center": v(-117.9, 12.1) * mm, "radius": 2 * mm});
            skCircle(sketch, "E8.0.12.20", {"center": v(-117.9, 28.1) * mm, "radius": 2 * mm});
            skCircle(sketch, "E8.0.12.21", {"center": v(-117.9, 44.1) * mm, "radius": 2 * mm});
            skCircle(sketch, "E8.0.12.22", {"center": v(-117.9, 60.1) * mm, "radius": 2 * mm});
            skCircle(sketch, "E8.0.12.23", {"center": v(-117.9, 76.1) * mm, "radius": 2 * mm});
            skCircle(sketch, "E8.0.12.24", {"center": v(-117.9, 92.1) * mm, "radius": 2 * mm});
            skCircle(sketch, "E8.0.12.25", {"center": v(-117.9, 108.1) * mm, "radius": 2 * mm});
            skCircle(sketch, "E8.0.12.26", {"center": v(-117.9, 124.1) * mm, "radius": 2 * mm});
            skCircle(sketch, "E8.0.12.27", {"center": v(-117.9, 140.1) * mm, "radius": 2 * mm});
            skCircle(sketch, "E8.0.12.28", {"center": v(-117.9, 156.1) * mm, "radius": 2 * mm});
            skCircle(sketch, "E8.0.12.29", {"center": v(-117.9, 172.1) * mm, "radius": 2 * mm});
            skCircle(sketch, "E8.0.12.30", {"center": v(-117.9, 188.1) * mm, "radius": 2 * mm});
            skCircle(sketch, "E8.0.12.31", {"center": v(-117.9, 204.1) * mm, "radius": 2 * mm});
            skCircle(sketch, "E8.0.12.32", {"center": v(-117.9, 220.1) * mm, "radius": 2 * mm});
            skCircle(sketch, "E8.0.12.33", {"center": v(-117.9, 236.1) * mm, "radius": 2 * mm});
            skCircle(sketch, "E8.0.12.34", {"center": v(-117.9, 252.1) * mm, "radius": 2 * mm});
            skCircle(sketch, "E8.0.12.35", {"center": v(-117.9, 268.1) * mm, "radius": 2 * mm});
            skCircle(sketch, "E8.0.12.36", {"center": v(-117.9, 284.1) * mm, "radius": 2 * mm});
            skCircle(sketch, "E8.0.12.37", {"center": v(-117.9, 300.1) * mm, "radius": 2 * mm});
            skCircle(sketch, "E8.0.13.10", {"center": v(-101.9, -131.9) * mm, "radius": 2 * mm});
            skCircle(sketch, "E8.0.13.11", {"center": v(-101.9, -115.9) * mm, "radius": 2 * mm});
            skCircle(sketch, "E8.0.13.12", {"center": v(-101.9, -99.9) * mm, "radius": 2 * mm});
            skCircle(sketch, "E8.0.13.13", {"center": v(-101.9, -83.9) * mm, "radius": 2 * mm});
            skCircle(sketch, "E8.0.13.14", {"center": v(-101.9, -67.9) * mm, "radius": 2 * mm});
            skCircle(sketch, "E8.0.13.15", {"center": v(-101.9, -51.9) * mm, "radius": 2 * mm});
            skCircle(sketch, "E8.0.13.16", {"center": v(-101.9, -35.9) * mm, "radius": 2 * mm});
            skCircle(sketch, "E8.0.13.17", {"center": v(-101.9, -19.9) * mm, "radius": 2 * mm});
            skCircle(sketch, "E8.0.13.18", {"center": v(-101.9, -3.9) * mm, "radius": 2 * mm});
            skCircle(sketch, "E8.0.13.19", {"center": v(-101.9, 12.1) * mm, "radius": 2 * mm});
            skCircle(sketch, "E8.0.13.20", {"center": v(-101.9, 28.1) * mm, "radius": 2 * mm});
            skCircle(sketch, "E8.0.13.21", {"center": v(-101.9, 44.1) * mm, "radius": 2 * mm});
            skCircle(sketch, "E8.0.13.22", {"center": v(-101.9, 60.1) * mm, "radius": 2 * mm});
            skCircle(sketch, "E8.0.13.23", {"center": v(-101.9, 76.1) * mm, "radius": 2 * mm});
            skCircle(sketch, "E8.0.13.24", {"center": v(-101.9, 92.1) * mm, "radius": 2 * mm});
            skCircle(sketch, "E8.0.13.25", {"center": v(-101.9, 108.1) * mm, "radius": 2 * mm});
            skCircle(sketch, "E8.0.13.26", {"center": v(-101.9, 124.1) * mm, "radius": 2 * mm});
            skCircle(sketch, "E8.0.13.27", {"center": v(-101.9, 140.1) * mm, "radius": 2 * mm});
            skCircle(sketch, "E8.0.13.28", {"center": v(-101.9, 156.1) * mm, "radius": 2 * mm});
            skCircle(sketch, "E8.0.13.29", {"center": v(-101.9, 172.1) * mm, "radius": 2 * mm});
            skCircle(sketch, "E8.0.13.30", {"center": v(-101.9, 188.1) * mm, "radius": 2 * mm});
            skCircle(sketch, "E8.0.13.31", {"center": v(-101.9, 204.1) * mm, "radius": 2 * mm});
            skCircle(sketch, "E8.0.13.32", {"center": v(-101.9, 220.1) * mm, "radius": 2 * mm});
            skCircle(sketch, "E8.0.13.33", {"center": v(-101.9, 236.1) * mm, "radius": 2 * mm});
            skCircle(sketch, "E8.0.13.34", {"center": v(-101.9, 252.1) * mm, "radius": 2 * mm});
            skCircle(sketch, "E8.0.13.35", {"center": v(-101.9, 268.1) * mm, "radius": 2 * mm});
            skCircle(sketch, "E8.0.13.36", {"center": v(-101.9, 284.1) * mm, "radius": 2 * mm});
            skCircle(sketch, "E8.0.13.37", {"center": v(-101.9, 300.1) * mm, "radius": 2 * mm});
            skCircle(sketch, "E8.0.14.10", {"center": v(-85.9, -131.9) * mm, "radius": 2 * mm});
            skCircle(sketch, "E8.0.14.11", {"center": v(-85.9, -115.9) * mm, "radius": 2 * mm});
            skCircle(sketch, "E8.0.14.12", {"center": v(-85.9, -99.9) * mm, "radius": 2 * mm});
            skCircle(sketch, "E8.0.14.13", {"center": v(-85.9, -83.9) * mm, "radius": 2 * mm});
            skCircle(sketch, "E8.0.14.14", {"center": v(-85.9, -67.9) * mm, "radius": 2 * mm});
            skCircle(sketch, "E8.0.14.15", {"center": v(-85.9, -51.9) * mm, "radius": 2 * mm});
            skCircle(sketch, "E8.0.14.16", {"center": v(-85.9, -35.9) * mm, "radius": 2 * mm});
            skCircle(sketch, "E8.0.14.17", {"center": v(-85.9, -19.9) * mm, "radius": 2 * mm});
            skCircle(sketch, "E8.0.14.18", {"center": v(-85.9, -3.9) * mm, "radius": 2 * mm});
            skCircle(sketch, "E8.0.14.19", {"center": v(-85.9, 12.1) * mm, "radius": 2 * mm});
            skCircle(sketch, "E8.0.14.20", {"center": v(-85.9, 28.1) * mm, "radius": 2 * mm});
            skCircle(sketch, "E8.0.14.21", {"center": v(-85.9, 44.1) * mm, "radius": 2 * mm});
            skCircle(sketch, "E8.0.14.22", {"center": v(-85.9, 60.1) * mm, "radius": 2 * mm});
            skCircle(sketch, "E8.0.14.23", {"center": v(-85.9, 76.1) * mm, "radius": 2 * mm});
            skCircle(sketch, "E8.0.14.24", {"center": v(-85.9, 92.1) * mm, "radius": 2 * mm});
            skCircle(sketch, "E8.0.14.25", {"center": v(-85.9, 108.1) * mm, "radius": 2 * mm});
            skCircle(sketch, "E8.0.14.26", {"center": v(-85.9, 124.1) * mm, "radius": 2 * mm});
            skCircle(sketch, "E8.0.14.27", {"center": v(-85.9, 140.1) * mm, "radius": 2 * mm});
            skCircle(sketch, "E8.0.14.28", {"center": v(-85.9, 156.1) * mm, "radius": 2 * mm});
            skCircle(sketch, "E8.0.14.29", {"center": v(-85.9, 172.1) * mm, "radius": 2 * mm});
            skCircle(sketch, "E8.0.14.30", {"center": v(-85.9, 188.1) * mm, "radius": 2 * mm});
            skCircle(sketch, "E8.0.14.31", {"center": v(-85.9, 204.1) * mm, "radius": 2 * mm});
            skCircle(sketch, "E8.0.14.32", {"center": v(-85.9, 220.1) * mm, "radius": 2 * mm});
            skCircle(sketch, "E8.0.14.33", {"center": v(-85.9, 236.1) * mm, "radius": 2 * mm});
            skCircle(sketch, "E8.0.14.34", {"center": v(-85.9, 252.1) * mm, "radius": 2 * mm});
            skCircle(sketch, "E8.0.14.35", {"center": v(-85.9, 268.1) * mm, "radius": 2 * mm});
            skCircle(sketch, "E8.0.14.36", {"center": v(-85.9, 284.1) * mm, "radius": 2 * mm});
            skCircle(sketch, "E8.0.14.37", {"center": v(-85.9, 300.1) * mm, "radius": 2 * mm});
            skCircle(sketch, "E8.0.15.10", {"center": v(-69.9, -131.9) * mm, "radius": 2 * mm});
            skCircle(sketch, "E8.0.15.11", {"center": v(-69.9, -115.9) * mm, "radius": 2 * mm});
            skCircle(sketch, "E8.0.15.12", {"center": v(-69.9, -99.9) * mm, "radius": 2 * mm});
            skCircle(sketch, "E8.0.15.13", {"center": v(-69.9, -83.9) * mm, "radius": 2 * mm});
            skCircle(sketch, "E8.0.15.14", {"center": v(-69.9, -67.9) * mm, "radius": 2 * mm});
            skCircle(sketch, "E8.0.15.15", {"center": v(-69.9, -51.9) * mm, "radius": 2 * mm});
            skCircle(sketch, "E8.0.15.16", {"center": v(-69.9, -35.9) * mm, "radius": 2 * mm});
            skCircle(sketch, "E8.0.15.17", {"center": v(-69.9, -19.9) * mm, "radius": 2 * mm});
            skCircle(sketch, "E8.0.15.18", {"center": v(-69.9, -3.9) * mm, "radius": 2 * mm});
            skCircle(sketch, "E8.0.15.19", {"center": v(-69.9, 12.1) * mm, "radius": 2 * mm});
            skCircle(sketch, "E8.0.15.20", {"center": v(-69.9, 28.1) * mm, "radius": 2 * mm});
            skCircle(sketch, "E8.0.15.21", {"center": v(-69.9, 44.1) * mm, "radius": 2 * mm});
            skCircle(sketch, "E8.0.15.22", {"center": v(-69.9, 60.1) * mm, "radius": 2 * mm});
            skCircle(sketch, "E8.0.15.23", {"center": v(-69.9, 76.1) * mm, "radius": 2 * mm});
            skCircle(sketch, "E8.0.15.24", {"center": v(-69.9, 92.1) * mm, "radius": 2 * mm});
            skCircle(sketch, "E8.0.15.25", {"center": v(-69.9, 108.1) * mm, "radius": 2 * mm});
            skCircle(sketch, "E8.0.15.26", {"center": v(-69.9, 124.1) * mm, "radius": 2 * mm});
            skCircle(sketch, "E8.0.15.27", {"center": v(-69.9, 140.1) * mm, "radius": 2 * mm});
            skCircle(sketch, "E8.0.15.28", {"center": v(-69.9, 156.1) * mm, "radius": 2 * mm});
            skCircle(sketch, "E8.0.15.29", {"center": v(-69.9, 172.1) * mm, "radius": 2 * mm});
            skCircle(sketch, "E8.0.15.30", {"center": v(-69.9, 188.1) * mm, "radius": 2 * mm});
            skCircle(sketch, "E8.0.15.31", {"center": v(-69.9, 204.1) * mm, "radius": 2 * mm});
            skCircle(sketch, "E8.0.15.32", {"center": v(-69.9, 220.1) * mm, "radius": 2 * mm});
            skCircle(sketch, "E8.0.15.33", {"center": v(-69.9, 236.1) * mm, "radius": 2 * mm});
            skCircle(sketch, "E8.0.15.34", {"center": v(-69.9, 252.1) * mm, "radius": 2 * mm});
            skCircle(sketch, "E8.0.15.35", {"center": v(-69.9, 268.1) * mm, "radius": 2 * mm});
            skCircle(sketch, "E8.0.15.36", {"center": v(-69.9, 284.1) * mm, "radius": 2 * mm});
            skCircle(sketch, "E8.0.15.37", {"center": v(-69.9, 300.1) * mm, "radius": 2 * mm});
            skCircle(sketch, "E8.0.16.10", {"center": v(-53.9, -131.9) * mm, "radius": 2 * mm});
            skCircle(sketch, "E8.0.16.11", {"center": v(-53.9, -115.9) * mm, "radius": 2 * mm});
            skCircle(sketch, "E8.0.16.12", {"center": v(-53.9, -99.9) * mm, "radius": 2 * mm});
            skCircle(sketch, "E8.0.16.13", {"center": v(-53.9, -83.9) * mm, "radius": 2 * mm});
            skCircle(sketch, "E8.0.16.14", {"center": v(-53.9, -67.9) * mm, "radius": 2 * mm});
            skCircle(sketch, "E8.0.16.15", {"center": v(-53.9, -51.9) * mm, "radius": 2 * mm});
            skCircle(sketch, "E8.0.16.16", {"center": v(-53.9, -35.9) * mm, "radius": 2 * mm});
            skCircle(sketch, "E8.0.16.17", {"center": v(-53.9, -19.9) * mm, "radius": 2 * mm});
            skCircle(sketch, "E8.0.16.18", {"center": v(-53.9, -3.9) * mm, "radius": 2 * mm});
            skCircle(sketch, "E8.0.16.19", {"center": v(-53.9, 12.1) * mm, "radius": 2 * mm});
            skCircle(sketch, "E8.0.16.20", {"center": v(-53.9, 28.1) * mm, "radius": 2 * mm});
            skCircle(sketch, "E8.0.16.21", {"center": v(-53.9, 44.1) * mm, "radius": 2 * mm});
            skCircle(sketch, "E8.0.16.22", {"center": v(-53.9, 60.1) * mm, "radius": 2 * mm});
            skCircle(sketch, "E8.0.16.23", {"center": v(-53.9, 76.1) * mm, "radius": 2 * mm});
            skCircle(sketch, "E8.0.16.24", {"center": v(-53.9, 92.1) * mm, "radius": 2 * mm});
            skCircle(sketch, "E8.0.16.25", {"center": v(-53.9, 108.1) * mm, "radius": 2 * mm});
            skCircle(sketch, "E8.0.16.26", {"center": v(-53.9, 124.1) * mm, "radius": 2 * mm});
            skCircle(sketch, "E8.0.16.27", {"center": v(-53.9, 140.1) * mm, "radius": 2 * mm});
            skCircle(sketch, "E8.0.16.28", {"center": v(-53.9, 156.1) * mm, "radius": 2 * mm});
            skCircle(sketch, "E8.0.16.29", {"center": v(-53.9, 172.1) * mm, "radius": 2 * mm});
            skCircle(sketch, "E8.0.16.30", {"center": v(-53.9, 188.1) * mm, "radius": 2 * mm});
            skCircle(sketch, "E8.0.16.31", {"center": v(-53.9, 204.1) * mm, "radius": 2 * mm});
            skCircle(sketch, "E8.0.16.32", {"center": v(-53.9, 220.1) * mm, "radius": 2 * mm});
            skCircle(sketch, "E8.0.16.33", {"center": v(-53.9, 236.1) * mm, "radius": 2 * mm});
            skCircle(sketch, "E8.0.16.34", {"center": v(-53.9, 252.1) * mm, "radius": 2 * mm});
            skCircle(sketch, "E8.0.16.35", {"center": v(-53.9, 268.1) * mm, "radius": 2 * mm});
            skCircle(sketch, "E8.0.16.36", {"center": v(-53.9, 284.1) * mm, "radius": 2 * mm});
            skCircle(sketch, "E8.0.16.37", {"center": v(-53.9, 300.1) * mm, "radius": 2 * mm});
            skCircle(sketch, "E8.0.17.10", {"center": v(-37.9, -131.9) * mm, "radius": 2 * mm});
            skCircle(sketch, "E8.0.17.11", {"center": v(-37.9, -115.9) * mm, "radius": 2 * mm});
            skCircle(sketch, "E8.0.17.12", {"center": v(-37.9, -99.9) * mm, "radius": 2 * mm});
            skCircle(sketch, "E8.0.17.13", {"center": v(-37.9, -83.9) * mm, "radius": 2 * mm});
            skCircle(sketch, "E8.0.17.14", {"center": v(-37.9, -67.9) * mm, "radius": 2 * mm});
            skCircle(sketch, "E8.0.17.15", {"center": v(-37.9, -51.9) * mm, "radius": 2 * mm});
            skCircle(sketch, "E8.0.17.16", {"center": v(-37.9, -35.9) * mm, "radius": 2 * mm});
            skCircle(sketch, "E8.0.17.17", {"center": v(-37.9, -19.9) * mm, "radius": 2 * mm});
            skCircle(sketch, "E8.0.17.18", {"center": v(-37.9, -3.9) * mm, "radius": 2 * mm});
            skCircle(sketch, "E8.0.17.19", {"center": v(-37.9, 12.1) * mm, "radius": 2 * mm});
            skCircle(sketch, "E8.0.17.20", {"center": v(-37.9, 28.1) * mm, "radius": 2 * mm});
            skCircle(sketch, "E8.0.17.21", {"center": v(-37.9, 44.1) * mm, "radius": 2 * mm});
            skCircle(sketch, "E8.0.17.22", {"center": v(-37.9, 60.1) * mm, "radius": 2 * mm});
            skCircle(sketch, "E8.0.17.23", {"center": v(-37.9, 76.1) * mm, "radius": 2 * mm});
            skCircle(sketch, "E8.0.17.24", {"center": v(-37.9, 92.1) * mm, "radius": 2 * mm});
            skCircle(sketch, "E8.0.17.25", {"center": v(-37.9, 108.1) * mm, "radius": 2 * mm});
            skCircle(sketch, "E8.0.17.26", {"center": v(-37.9, 124.1) * mm, "radius": 2 * mm});
            skCircle(sketch, "E8.0.17.27", {"center": v(-37.9, 140.1) * mm, "radius": 2 * mm});
            skCircle(sketch, "E8.0.17.28", {"center": v(-37.9, 156.1) * mm, "radius": 2 * mm});
            skCircle(sketch, "E8.0.17.29", {"center": v(-37.9, 172.1) * mm, "radius": 2 * mm});
            skCircle(sketch, "E8.0.17.30", {"center": v(-37.9, 188.1) * mm, "radius": 2 * mm});
            skCircle(sketch, "E8.0.17.31", {"center": v(-37.9, 204.1) * mm, "radius": 2 * mm});
            skCircle(sketch, "E8.0.17.32", {"center": v(-37.9, 220.1) * mm, "radius": 2 * mm});
            skCircle(sketch, "E8.0.17.33", {"center": v(-37.9, 236.1) * mm, "radius": 2 * mm});
            skCircle(sketch, "E8.0.17.34", {"center": v(-37.9, 252.1) * mm, "radius": 2 * mm});
            skCircle(sketch, "E8.0.17.35", {"center": v(-37.9, 268.1) * mm, "radius": 2 * mm});
            skCircle(sketch, "E8.0.17.36", {"center": v(-37.9, 284.1) * mm, "radius": 2 * mm});
            skCircle(sketch, "E8.0.17.37", {"center": v(-37.9, 300.1) * mm, "radius": 2 * mm});
            skCircle(sketch, "E8.0.18.10", {"center": v(-21.9, -131.9) * mm, "radius": 2 * mm});
            skCircle(sketch, "E8.0.18.11", {"center": v(-21.9, -115.9) * mm, "radius": 2 * mm});
            skCircle(sketch, "E8.0.18.12", {"center": v(-21.9, -99.9) * mm, "radius": 2 * mm});
            skCircle(sketch, "E8.0.18.13", {"center": v(-21.9, -83.9) * mm, "radius": 2 * mm});
            skCircle(sketch, "E8.0.18.14", {"center": v(-21.9, -67.9) * mm, "radius": 2 * mm});
            skCircle(sketch, "E8.0.18.15", {"center": v(-21.9, -51.9) * mm, "radius": 2 * mm});
            skCircle(sketch, "E8.0.18.16", {"center": v(-21.9, -35.9) * mm, "radius": 2 * mm});
            skCircle(sketch, "E8.0.18.17", {"center": v(-21.9, -19.9) * mm, "radius": 2 * mm});
            skCircle(sketch, "E8.0.18.18", {"center": v(-21.9, -3.9) * mm, "radius": 2 * mm});
            skCircle(sketch, "E8.0.18.19", {"center": v(-21.9, 12.1) * mm, "radius": 2 * mm});
            skCircle(sketch, "E8.0.18.20", {"center": v(-21.9, 28.1) * mm, "radius": 2 * mm});
            skCircle(sketch, "E8.0.18.21", {"center": v(-21.9, 44.1) * mm, "radius": 2 * mm});
            skCircle(sketch, "E8.0.18.22", {"center": v(-21.9, 60.1) * mm, "radius": 2 * mm});
            skCircle(sketch, "E8.0.18.23", {"center": v(-21.9, 76.1) * mm, "radius": 2 * mm});
            skCircle(sketch, "E8.0.18.24", {"center": v(-21.9, 92.1) * mm, "radius": 2 * mm});
            skCircle(sketch, "E8.0.18.25", {"center": v(-21.9, 108.1) * mm, "radius": 2 * mm});
            skCircle(sketch, "E8.0.18.26", {"center": v(-21.9, 124.1) * mm, "radius": 2 * mm});
            skCircle(sketch, "E8.0.18.27", {"center": v(-21.9, 140.1) * mm, "radius": 2 * mm});
            skCircle(sketch, "E8.0.18.28", {"center": v(-21.9, 156.1) * mm, "radius": 2 * mm});
            skCircle(sketch, "E8.0.18.29", {"center": v(-21.9, 172.1) * mm, "radius": 2 * mm});
            skCircle(sketch, "E8.0.18.30", {"center": v(-21.9, 188.1) * mm, "radius": 2 * mm});
            skCircle(sketch, "E8.0.18.31", {"center": v(-21.9, 204.1) * mm, "radius": 2 * mm});
            skCircle(sketch, "E8.0.18.32", {"center": v(-21.9, 220.1) * mm, "radius": 2 * mm});
            skCircle(sketch, "E8.0.18.33", {"center": v(-21.9, 236.1) * mm, "radius": 2 * mm});
            skCircle(sketch, "E8.0.18.34", {"center": v(-21.9, 252.1) * mm, "radius": 2 * mm});
            skCircle(sketch, "E8.0.18.35", {"center": v(-21.9, 268.1) * mm, "radius": 2 * mm});
            skCircle(sketch, "E8.0.18.36", {"center": v(-21.9, 284.1) * mm, "radius": 2 * mm});
            skCircle(sketch, "E8.0.18.37", {"center": v(-21.9, 300.1) * mm, "radius": 2 * mm});
            skCircle(sketch, "E8.0.19.10", {"center": v(-5.9, -131.9) * mm, "radius": 2 * mm});
            skCircle(sketch, "E8.0.19.11", {"center": v(-5.9, -115.9) * mm, "radius": 2 * mm});
            skCircle(sketch, "E8.0.19.12", {"center": v(-5.9, -99.9) * mm, "radius": 2 * mm});
            skCircle(sketch, "E8.0.19.13", {"center": v(-5.9, -83.9) * mm, "radius": 2 * mm});
            skCircle(sketch, "E8.0.19.14", {"center": v(-5.9, -67.9) * mm, "radius": 2 * mm});
            skCircle(sketch, "E8.0.19.15", {"center": v(-5.9, -51.9) * mm, "radius": 2 * mm});
            skCircle(sketch, "E8.0.19.16", {"center": v(-5.9, -35.9) * mm, "radius": 2 * mm});
            skCircle(sketch, "E8.0.19.17", {"center": v(-5.9, -19.9) * mm, "radius": 2 * mm});
            skCircle(sketch, "E8.0.19.18", {"center": v(-5.9, -3.9) * mm, "radius": 2 * mm});
            skCircle(sketch, "E8.0.19.19", {"center": v(-5.9, 12.1) * mm, "radius": 2 * mm});
            skCircle(sketch, "E8.0.19.20", {"center": v(-5.9, 28.1) * mm, "radius": 2 * mm});
            skCircle(sketch, "E8.0.19.21", {"center": v(-5.9, 44.1) * mm, "radius": 2 * mm});
            skCircle(sketch, "E8.0.19.22", {"center": v(-5.9, 60.1) * mm, "radius": 2 * mm});
            skCircle(sketch, "E8.0.19.23", {"center": v(-5.9, 76.1) * mm, "radius": 2 * mm});
            skCircle(sketch, "E8.0.19.24", {"center": v(-5.9, 92.1) * mm, "radius": 2 * mm});
            skCircle(sketch, "E8.0.19.25", {"center": v(-5.9, 108.1) * mm, "radius": 2 * mm});
            skCircle(sketch, "E8.0.19.26", {"center": v(-5.9, 124.1) * mm, "radius": 2 * mm});
            skCircle(sketch, "E8.0.19.27", {"center": v(-5.9, 140.1) * mm, "radius": 2 * mm});
            skCircle(sketch, "E8.0.19.28", {"center": v(-5.9, 156.1) * mm, "radius": 2 * mm});
            skCircle(sketch, "E8.0.19.29", {"center": v(-5.9, 172.1) * mm, "radius": 2 * mm});
            skCircle(sketch, "E8.0.19.30", {"center": v(-5.9, 188.1) * mm, "radius": 2 * mm});
            skCircle(sketch, "E8.0.19.31", {"center": v(-5.9, 204.1) * mm, "radius": 2 * mm});
            skCircle(sketch, "E8.0.19.32", {"center": v(-5.9, 220.1) * mm, "radius": 2 * mm});
            skCircle(sketch, "E8.0.19.33", {"center": v(-5.9, 236.1) * mm, "radius": 2 * mm});
            skCircle(sketch, "E8.0.19.34", {"center": v(-5.9, 252.1) * mm, "radius": 2 * mm});
            skCircle(sketch, "E8.0.19.35", {"center": v(-5.9, 268.1) * mm, "radius": 2 * mm});
            skCircle(sketch, "E8.0.19.36", {"center": v(-5.9, 284.1) * mm, "radius": 2 * mm});
            skCircle(sketch, "E8.0.19.37", {"center": v(-5.9, 300.1) * mm, "radius": 2 * mm});
            skCircle(sketch, "E8.0.20.10", {"center": v(10.1, -131.9) * mm, "radius": 2 * mm});
            skCircle(sketch, "E8.0.20.11", {"center": v(10.1, -115.9) * mm, "radius": 2 * mm});
            skCircle(sketch, "E8.0.20.12", {"center": v(10.1, -99.9) * mm, "radius": 2 * mm});
            skCircle(sketch, "E8.0.20.13", {"center": v(10.1, -83.9) * mm, "radius": 2 * mm});
            skCircle(sketch, "E8.0.20.14", {"center": v(10.1, -67.9) * mm, "radius": 2 * mm});
            skCircle(sketch, "E8.0.20.15", {"center": v(10.1, -51.9) * mm, "radius": 2 * mm});
            skCircle(sketch, "E8.0.20.16", {"center": v(10.1, -35.9) * mm, "radius": 2 * mm});
            skCircle(sketch, "E8.0.20.17", {"center": v(10.1, -19.9) * mm, "radius": 2 * mm});
            skCircle(sketch, "E8.0.20.18", {"center": v(10.1, -3.9) * mm, "radius": 2 * mm});
            skCircle(sketch, "E8.0.20.19", {"center": v(10.1, 12.1) * mm, "radius": 2 * mm});
            skCircle(sketch, "E8.0.20.20", {"center": v(10.1, 28.1) * mm, "radius": 2 * mm});
            skCircle(sketch, "E8.0.20.21", {"center": v(10.1, 44.1) * mm, "radius": 2 * mm});
            skCircle(sketch, "E8.0.20.22", {"center": v(10.1, 60.1) * mm, "radius": 2 * mm});
            skCircle(sketch, "E8.0.20.23", {"center": v(10.1, 76.1) * mm, "radius": 2 * mm});
            skCircle(sketch, "E8.0.20.24", {"center": v(10.1, 92.1) * mm, "radius": 2 * mm});
            skCircle(sketch, "E8.0.20.25", {"center": v(10.1, 108.1) * mm, "radius": 2 * mm});
            skCircle(sketch, "E8.0.20.26", {"center": v(10.1, 124.1) * mm, "radius": 2 * mm});
            skCircle(sketch, "E8.0.20.27", {"center": v(10.1, 140.1) * mm, "radius": 2 * mm});
            skCircle(sketch, "E8.0.20.28", {"center": v(10.1, 156.1) * mm, "radius": 2 * mm});
            skCircle(sketch, "E8.0.20.29", {"center": v(10.1, 172.1) * mm, "radius": 2 * mm});
            skCircle(sketch, "E8.0.20.30", {"center": v(10.1, 188.1) * mm, "radius": 2 * mm});
            skCircle(sketch, "E8.0.20.31", {"center": v(10.1, 204.1) * mm, "radius": 2 * mm});
            skCircle(sketch, "E8.0.20.32", {"center": v(10.1, 220.1) * mm, "radius": 2 * mm});
            skCircle(sketch, "E8.0.20.33", {"center": v(10.1, 236.1) * mm, "radius": 2 * mm});
            skCircle(sketch, "E8.0.20.34", {"center": v(10.1, 252.1) * mm, "radius": 2 * mm});
            skCircle(sketch, "E8.0.20.35", {"center": v(10.1, 268.1) * mm, "radius": 2 * mm});
            skCircle(sketch, "E8.0.20.36", {"center": v(10.1, 284.1) * mm, "radius": 2 * mm});
            skCircle(sketch, "E8.0.20.37", {"center": v(10.1, 300.1) * mm, "radius": 2 * mm});
            skCircle(sketch, "E8.0.21.10", {"center": v(26.1, -131.9) * mm, "radius": 2 * mm});
            skCircle(sketch, "E8.0.21.11", {"center": v(26.1, -115.9) * mm, "radius": 2 * mm});
            skCircle(sketch, "E8.0.21.12", {"center": v(26.1, -99.9) * mm, "radius": 2 * mm});
            skCircle(sketch, "E8.0.21.13", {"center": v(26.1, -83.9) * mm, "radius": 2 * mm});
            skCircle(sketch, "E8.0.21.14", {"center": v(26.1, -67.9) * mm, "radius": 2 * mm});
            skCircle(sketch, "E8.0.21.15", {"center": v(26.1, -51.9) * mm, "radius": 2 * mm});
            skCircle(sketch, "E8.0.21.16", {"center": v(26.1, -35.9) * mm, "radius": 2 * mm});
            skCircle(sketch, "E8.0.21.17", {"center": v(26.1, -19.9) * mm, "radius": 2 * mm});
            skCircle(sketch, "E8.0.21.18", {"center": v(26.1, -3.9) * mm, "radius": 2 * mm});
            skCircle(sketch, "E8.0.21.19", {"center": v(26.1, 12.1) * mm, "radius": 2 * mm});
            skCircle(sketch, "E8.0.21.20", {"center": v(26.1, 28.1) * mm, "radius": 2 * mm});
            skCircle(sketch, "E8.0.21.21", {"center": v(26.1, 44.1) * mm, "radius": 2 * mm});
            skCircle(sketch, "E8.0.21.22", {"center": v(26.1, 60.1) * mm, "radius": 2 * mm});
            skCircle(sketch, "E8.0.21.23", {"center": v(26.1, 76.1) * mm, "radius": 2 * mm});
            skCircle(sketch, "E8.0.21.24", {"center": v(26.1, 92.1) * mm, "radius": 2 * mm});
            skCircle(sketch, "E8.0.21.25", {"center": v(26.1, 108.1) * mm, "radius": 2 * mm});
            skCircle(sketch, "E8.0.21.26", {"center": v(26.1, 124.1) * mm, "radius": 2 * mm});
            skCircle(sketch, "E8.0.21.27", {"center": v(26.1, 140.1) * mm, "radius": 2 * mm});
            skCircle(sketch, "E8.0.21.28", {"center": v(26.1, 156.1) * mm, "radius": 2 * mm});
            skCircle(sketch, "E8.0.21.29", {"center": v(26.1, 172.1) * mm, "radius": 2 * mm});
            skCircle(sketch, "E8.0.21.30", {"center": v(26.1, 188.1) * mm, "radius": 2 * mm});
            skCircle(sketch, "E8.0.21.31", {"center": v(26.1, 204.1) * mm, "radius": 2 * mm});
            skCircle(sketch, "E8.0.21.32", {"center": v(26.1, 220.1) * mm, "radius": 2 * mm});
            skCircle(sketch, "E8.0.21.33", {"center": v(26.1, 236.1) * mm, "radius": 2 * mm});
            skCircle(sketch, "E8.0.21.34", {"center": v(26.1, 252.1) * mm, "radius": 2 * mm});
            skCircle(sketch, "E8.0.21.35", {"center": v(26.1, 268.1) * mm, "radius": 2 * mm});
            skCircle(sketch, "E8.0.21.36", {"center": v(26.1, 284.1) * mm, "radius": 2 * mm});
            skCircle(sketch, "E8.0.21.37", {"center": v(26.1, 300.1) * mm, "radius": 2 * mm});
            skCircle(sketch, "E8.0.22.10", {"center": v(42.1, -131.9) * mm, "radius": 2 * mm});
            skCircle(sketch, "E8.0.22.11", {"center": v(42.1, -115.9) * mm, "radius": 2 * mm});
            skCircle(sketch, "E8.0.22.12", {"center": v(42.1, -99.9) * mm, "radius": 2 * mm});
            skCircle(sketch, "E8.0.22.13", {"center": v(42.1, -83.9) * mm, "radius": 2 * mm});
            skCircle(sketch, "E8.0.22.14", {"center": v(42.1, -67.9) * mm, "radius": 2 * mm});
            skCircle(sketch, "E8.0.22.15", {"center": v(42.1, -51.9) * mm, "radius": 2 * mm});
            skCircle(sketch, "E8.0.22.16", {"center": v(42.1, -35.9) * mm, "radius": 2 * mm});
            skCircle(sketch, "E8.0.22.17", {"center": v(42.1, -19.9) * mm, "radius": 2 * mm});
            skCircle(sketch, "E8.0.22.18", {"center": v(42.1, -3.9) * mm, "radius": 2 * mm});
            skCircle(sketch, "E8.0.22.19", {"center": v(42.1, 12.1) * mm, "radius": 2 * mm});
            skCircle(sketch, "E8.0.22.20", {"center": v(42.1, 28.1) * mm, "radius": 2 * mm});
            skCircle(sketch, "E8.0.22.21", {"center": v(42.1, 44.1) * mm, "radius": 2 * mm});
            skCircle(sketch, "E8.0.22.22", {"center": v(42.1, 60.1) * mm, "radius": 2 * mm});
            skCircle(sketch, "E8.0.22.23", {"center": v(42.1, 76.1) * mm, "radius": 2 * mm});
            skCircle(sketch, "E8.0.22.24", {"center": v(42.1, 92.1) * mm, "radius": 2 * mm});
            skCircle(sketch, "E8.0.22.25", {"center": v(42.1, 108.1) * mm, "radius": 2 * mm});
            skCircle(sketch, "E8.0.22.26", {"center": v(42.1, 124.1) * mm, "radius": 2 * mm});
            skCircle(sketch, "E8.0.22.27", {"center": v(42.1, 140.1) * mm, "radius": 2 * mm});
            skCircle(sketch, "E8.0.22.28", {"center": v(42.1, 156.1) * mm, "radius": 2 * mm});
            skCircle(sketch, "E8.0.22.29", {"center": v(42.1, 172.1) * mm, "radius": 2 * mm});
            skCircle(sketch, "E8.0.22.30", {"center": v(42.1, 188.1) * mm, "radius": 2 * mm});
            skCircle(sketch, "E8.0.22.31", {"center": v(42.1, 204.1) * mm, "radius": 2 * mm});
            skCircle(sketch, "E8.0.22.32", {"center": v(42.1, 220.1) * mm, "radius": 2 * mm});
            skCircle(sketch, "E8.0.22.33", {"center": v(42.1, 236.1) * mm, "radius": 2 * mm});
            skCircle(sketch, "E8.0.22.34", {"center": v(42.1, 252.1) * mm, "radius": 2 * mm});
            skCircle(sketch, "E8.0.22.35", {"center": v(42.1, 268.1) * mm, "radius": 2 * mm});
            skCircle(sketch, "E8.0.22.36", {"center": v(42.1, 284.1) * mm, "radius": 2 * mm});
            skCircle(sketch, "E8.0.22.37", {"center": v(42.1, 300.1) * mm, "radius": 2 * mm});
            skCircle(sketch, "E8.0.23.10", {"center": v(58.1, -131.9) * mm, "radius": 2 * mm});
            skCircle(sketch, "E8.0.23.11", {"center": v(58.1, -115.9) * mm, "radius": 2 * mm});
            skCircle(sketch, "E8.0.23.12", {"center": v(58.1, -99.9) * mm, "radius": 2 * mm});
            skCircle(sketch, "E8.0.23.13", {"center": v(58.1, -83.9) * mm, "radius": 2 * mm});
            skCircle(sketch, "E8.0.23.14", {"center": v(58.1, -67.9) * mm, "radius": 2 * mm});
            skCircle(sketch, "E8.0.23.15", {"center": v(58.1, -51.9) * mm, "radius": 2 * mm});
            skCircle(sketch, "E8.0.23.16", {"center": v(58.1, -35.9) * mm, "radius": 2 * mm});
            skCircle(sketch, "E8.0.23.17", {"center": v(58.1, -19.9) * mm, "radius": 2 * mm});
            skCircle(sketch, "E8.0.23.18", {"center": v(58.1, -3.9) * mm, "radius": 2 * mm});
            skCircle(sketch, "E8.0.23.19", {"center": v(58.1, 12.1) * mm, "radius": 2 * mm});
            skCircle(sketch, "E8.0.23.20", {"center": v(58.1, 28.1) * mm, "radius": 2 * mm});
            skCircle(sketch, "E8.0.23.21", {"center": v(58.1, 44.1) * mm, "radius": 2 * mm});
            skCircle(sketch, "E8.0.23.22", {"center": v(58.1, 60.1) * mm, "radius": 2 * mm});
            skCircle(sketch, "E8.0.23.23", {"center": v(58.1, 76.1) * mm, "radius": 2 * mm});
            skCircle(sketch, "E8.0.23.24", {"center": v(58.1, 92.1) * mm, "radius": 2 * mm});
            skCircle(sketch, "E8.0.23.25", {"center": v(58.1, 108.1) * mm, "radius": 2 * mm});
            skCircle(sketch, "E8.0.23.26", {"center": v(58.1, 124.1) * mm, "radius": 2 * mm});
            skCircle(sketch, "E8.0.23.27", {"center": v(58.1, 140.1) * mm, "radius": 2 * mm});
            skCircle(sketch, "E8.0.23.28", {"center": v(58.1, 156.1) * mm, "radius": 2 * mm});
            skCircle(sketch, "E8.0.23.29", {"center": v(58.1, 172.1) * mm, "radius": 2 * mm});
            skCircle(sketch, "E8.0.23.30", {"center": v(58.1, 188.1) * mm, "radius": 2 * mm});
            skCircle(sketch, "E8.0.23.31", {"center": v(58.1, 204.1) * mm, "radius": 2 * mm});
            skCircle(sketch, "E8.0.23.32", {"center": v(58.1, 220.1) * mm, "radius": 2 * mm});
            skCircle(sketch, "E8.0.23.33", {"center": v(58.1, 236.1) * mm, "radius": 2 * mm});
            skCircle(sketch, "E8.0.23.34", {"center": v(58.1, 252.1) * mm, "radius": 2 * mm});
            skCircle(sketch, "E8.0.23.35", {"center": v(58.1, 268.1) * mm, "radius": 2 * mm});
            skCircle(sketch, "E8.0.23.36", {"center": v(58.1, 284.1) * mm, "radius": 2 * mm});
            skCircle(sketch, "E8.0.23.37", {"center": v(58.1, 300.1) * mm, "radius": 2 * mm});
            skCircle(sketch, "E8.0.24.10", {"center": v(74.1, -131.9) * mm, "radius": 2 * mm});
            skCircle(sketch, "E8.0.24.11", {"center": v(74.1, -115.9) * mm, "radius": 2 * mm});
            skCircle(sketch, "E8.0.24.12", {"center": v(74.1, -99.9) * mm, "radius": 2 * mm});
            skCircle(sketch, "E8.0.24.13", {"center": v(74.1, -83.9) * mm, "radius": 2 * mm});
            skCircle(sketch, "E8.0.24.14", {"center": v(74.1, -67.9) * mm, "radius": 2 * mm});
            skCircle(sketch, "E8.0.24.15", {"center": v(74.1, -51.9) * mm, "radius": 2 * mm});
            skCircle(sketch, "E8.0.24.16", {"center": v(74.1, -35.9) * mm, "radius": 2 * mm});
            skCircle(sketch, "E8.0.24.17", {"center": v(74.1, -19.9) * mm, "radius": 2 * mm});
            skCircle(sketch, "E8.0.24.18", {"center": v(74.1, -3.9) * mm, "radius": 2 * mm});
            skCircle(sketch, "E8.0.24.19", {"center": v(74.1, 12.1) * mm, "radius": 2 * mm});
            skCircle(sketch, "E8.0.24.20", {"center": v(74.1, 28.1) * mm, "radius": 2 * mm});
            skCircle(sketch, "E8.0.24.21", {"center": v(74.1, 44.1) * mm, "radius": 2 * mm});
            skCircle(sketch, "E8.0.24.22", {"center": v(74.1, 60.1) * mm, "radius": 2 * mm});
            skCircle(sketch, "E8.0.24.23", {"center": v(74.1, 76.1) * mm, "radius": 2 * mm});
            skCircle(sketch, "E8.0.24.24", {"center": v(74.1, 92.1) * mm, "radius": 2 * mm});
            skCircle(sketch, "E8.0.24.25", {"center": v(74.1, 108.1) * mm, "radius": 2 * mm});
            skCircle(sketch, "E8.0.24.26", {"center": v(74.1, 124.1) * mm, "radius": 2 * mm});
            skCircle(sketch, "E8.0.24.27", {"center": v(74.1, 140.1) * mm, "radius": 2 * mm});
            skCircle(sketch, "E8.0.24.28", {"center": v(74.1, 156.1) * mm, "radius": 2 * mm});
            skCircle(sketch, "E8.0.24.29", {"center": v(74.1, 172.1) * mm, "radius": 2 * mm});
            skCircle(sketch, "E8.0.24.30", {"center": v(74.1, 188.1) * mm, "radius": 2 * mm});
            skCircle(sketch, "E8.0.24.31", {"center": v(74.1, 204.1) * mm, "radius": 2 * mm});
            skCircle(sketch, "E8.0.24.32", {"center": v(74.1, 220.1) * mm, "radius": 2 * mm});
            skCircle(sketch, "E8.0.24.33", {"center": v(74.1, 236.1) * mm, "radius": 2 * mm});
            skCircle(sketch, "E8.0.24.34", {"center": v(74.1, 252.1) * mm, "radius": 2 * mm});
            skCircle(sketch, "E8.0.24.35", {"center": v(74.1, 268.1) * mm, "radius": 2 * mm});
            skCircle(sketch, "E8.0.24.36", {"center": v(74.1, 284.1) * mm, "radius": 2 * mm});
            skCircle(sketch, "E8.0.24.37", {"center": v(74.1, 300.1) * mm, "radius": 2 * mm});
            skCircle(sketch, "E8.0.25.10", {"center": v(90.1, -131.9) * mm, "radius": 2 * mm});
            skCircle(sketch, "E8.0.25.11", {"center": v(90.1, -115.9) * mm, "radius": 2 * mm});
            skCircle(sketch, "E8.0.25.12", {"center": v(90.1, -99.9) * mm, "radius": 2 * mm});
            skCircle(sketch, "E8.0.25.13", {"center": v(90.1, -83.9) * mm, "radius": 2 * mm});
            skCircle(sketch, "E8.0.25.14", {"center": v(90.1, -67.9) * mm, "radius": 2 * mm});
            skCircle(sketch, "E8.0.25.15", {"center": v(90.1, -51.9) * mm, "radius": 2 * mm});
            skCircle(sketch, "E8.0.25.16", {"center": v(90.1, -35.9) * mm, "radius": 2 * mm});
            skCircle(sketch, "E8.0.25.17", {"center": v(90.1, -19.9) * mm, "radius": 2 * mm});
            skCircle(sketch, "E8.0.25.18", {"center": v(90.1, -3.9) * mm, "radius": 2 * mm});
            skCircle(sketch, "E8.0.25.19", {"center": v(90.1, 12.1) * mm, "radius": 2 * mm});
            skCircle(sketch, "E8.0.25.20", {"center": v(90.1, 28.1) * mm, "radius": 2 * mm});
            skCircle(sketch, "E8.0.25.21", {"center": v(90.1, 44.1) * mm, "radius": 2 * mm});
            skCircle(sketch, "E8.0.25.22", {"center": v(90.1, 60.1) * mm, "radius": 2 * mm});
            skCircle(sketch, "E8.0.25.23", {"center": v(90.1, 76.1) * mm, "radius": 2 * mm});
            skCircle(sketch, "E8.0.25.24", {"center": v(90.1, 92.1) * mm, "radius": 2 * mm});
            skCircle(sketch, "E8.0.25.25", {"center": v(90.1, 108.1) * mm, "radius": 2 * mm});
            skCircle(sketch, "E8.0.25.26", {"center": v(90.1, 124.1) * mm, "radius": 2 * mm});
            skCircle(sketch, "E8.0.25.27", {"center": v(90.1, 140.1) * mm, "radius": 2 * mm});
            skCircle(sketch, "E8.0.25.28", {"center": v(90.1, 156.1) * mm, "radius": 2 * mm});
            skCircle(sketch, "E8.0.25.29", {"center": v(90.1, 172.1) * mm, "radius": 2 * mm});
            skCircle(sketch, "E8.0.25.30", {"center": v(90.1, 188.1) * mm, "radius": 2 * mm});
            skCircle(sketch, "E8.0.25.31", {"center": v(90.1, 204.1) * mm, "radius": 2 * mm});
            skCircle(sketch, "E8.0.25.32", {"center": v(90.1, 220.1) * mm, "radius": 2 * mm});
            skCircle(sketch, "E8.0.25.33", {"center": v(90.1, 236.1) * mm, "radius": 2 * mm});
            skCircle(sketch, "E8.0.25.34", {"center": v(90.1, 252.1) * mm, "radius": 2 * mm});
            skCircle(sketch, "E8.0.25.35", {"center": v(90.1, 268.1) * mm, "radius": 2 * mm});
            skCircle(sketch, "E8.0.25.36", {"center": v(90.1, 284.1) * mm, "radius": 2 * mm});
            skCircle(sketch, "E8.0.25.37", {"center": v(90.1, 300.1) * mm, "radius": 2 * mm});
            skCircle(sketch, "E8.0.26.10", {"center": v(106.1, -131.9) * mm, "radius": 2 * mm});
            skCircle(sketch, "E8.0.26.11", {"center": v(106.1, -115.9) * mm, "radius": 2 * mm});
            skCircle(sketch, "E8.0.26.12", {"center": v(106.1, -99.9) * mm, "radius": 2 * mm});
            skCircle(sketch, "E8.0.26.13", {"center": v(106.1, -83.9) * mm, "radius": 2 * mm});
            skCircle(sketch, "E8.0.26.14", {"center": v(106.1, -67.9) * mm, "radius": 2 * mm});
            skCircle(sketch, "E8.0.26.15", {"center": v(106.1, -51.9) * mm, "radius": 2 * mm});
            skCircle(sketch, "E8.0.26.16", {"center": v(106.1, -35.9) * mm, "radius": 2 * mm});
            skCircle(sketch, "E8.0.26.17", {"center": v(106.1, -19.9) * mm, "radius": 2 * mm});
            skCircle(sketch, "E8.0.26.18", {"center": v(106.1, -3.9) * mm, "radius": 2 * mm});
            skCircle(sketch, "E8.0.26.19", {"center": v(106.1, 12.1) * mm, "radius": 2 * mm});
            skCircle(sketch, "E8.0.26.20", {"center": v(106.1, 28.1) * mm, "radius": 2 * mm});
            skCircle(sketch, "E8.0.26.21", {"center": v(106.1, 44.1) * mm, "radius": 2 * mm});
            skCircle(sketch, "E8.0.26.22", {"center": v(106.1, 60.1) * mm, "radius": 2 * mm});
            skCircle(sketch, "E8.0.26.23", {"center": v(106.1, 76.1) * mm, "radius": 2 * mm});
            skCircle(sketch, "E8.0.26.24", {"center": v(106.1, 92.1) * mm, "radius": 2 * mm});
            skCircle(sketch, "E8.0.26.25", {"center": v(106.1, 108.1) * mm, "radius": 2 * mm});
            skCircle(sketch, "E8.0.26.26", {"center": v(106.1, 124.1) * mm, "radius": 2 * mm});
            skCircle(sketch, "E8.0.26.27", {"center": v(106.1, 140.1) * mm, "radius": 2 * mm});
            skCircle(sketch, "E8.0.26.28", {"center": v(106.1, 156.1) * mm, "radius": 2 * mm});
            skCircle(sketch, "E8.0.26.29", {"center": v(106.1, 172.1) * mm, "radius": 2 * mm});
            skCircle(sketch, "E8.0.26.30", {"center": v(106.1, 188.1) * mm, "radius": 2 * mm});
            skCircle(sketch, "E8.0.26.31", {"center": v(106.1, 204.1) * mm, "radius": 2 * mm});
            skCircle(sketch, "E8.0.26.32", {"center": v(106.1, 220.1) * mm, "radius": 2 * mm});
            skCircle(sketch, "E8.0.26.33", {"center": v(106.1, 236.1) * mm, "radius": 2 * mm});
            skCircle(sketch, "E8.0.26.34", {"center": v(106.1, 252.1) * mm, "radius": 2 * mm});
            skCircle(sketch, "E8.0.26.35", {"center": v(106.1, 268.1) * mm, "radius": 2 * mm});
            skCircle(sketch, "E8.0.26.36", {"center": v(106.1, 284.1) * mm, "radius": 2 * mm});
            skCircle(sketch, "E8.0.26.37", {"center": v(106.1, 300.1) * mm, "radius": 2 * mm});
            skCircle(sketch, "E8.0.27.10", {"center": v(122.1, -131.9) * mm, "radius": 2 * mm});
            skCircle(sketch, "E8.0.27.11", {"center": v(122.1, -115.9) * mm, "radius": 2 * mm});
            skCircle(sketch, "E8.0.27.12", {"center": v(122.1, -99.9) * mm, "radius": 2 * mm});
            skCircle(sketch, "E8.0.27.13", {"center": v(122.1, -83.9) * mm, "radius": 2 * mm});
            skCircle(sketch, "E8.0.27.14", {"center": v(122.1, -67.9) * mm, "radius": 2 * mm});
            skCircle(sketch, "E8.0.27.15", {"center": v(122.1, -51.9) * mm, "radius": 2 * mm});
            skCircle(sketch, "E8.0.27.16", {"center": v(122.1, -35.9) * mm, "radius": 2 * mm});
            skCircle(sketch, "E8.0.27.17", {"center": v(122.1, -19.9) * mm, "radius": 2 * mm});
            skCircle(sketch, "E8.0.27.18", {"center": v(122.1, -3.9) * mm, "radius": 2 * mm});
            skCircle(sketch, "E8.0.27.19", {"center": v(122.1, 12.1) * mm, "radius": 2 * mm});
            skCircle(sketch, "E8.0.27.20", {"center": v(122.1, 28.1) * mm, "radius": 2 * mm});
            skCircle(sketch, "E8.0.27.21", {"center": v(122.1, 44.1) * mm, "radius": 2 * mm});
            skCircle(sketch, "E8.0.27.22", {"center": v(122.1, 60.1) * mm, "radius": 2 * mm});
            skCircle(sketch, "E8.0.27.23", {"center": v(122.1, 76.1) * mm, "radius": 2 * mm});
            skCircle(sketch, "E8.0.27.24", {"center": v(122.1, 92.1) * mm, "radius": 2 * mm});
            skCircle(sketch, "E8.0.27.25", {"center": v(122.1, 108.1) * mm, "radius": 2 * mm});
            skCircle(sketch, "E8.0.27.26", {"center": v(122.1, 124.1) * mm, "radius": 2 * mm});
            skCircle(sketch, "E8.0.27.27", {"center": v(122.1, 140.1) * mm, "radius": 2 * mm});
            skCircle(sketch, "E8.0.27.28", {"center": v(122.1, 156.1) * mm, "radius": 2 * mm});
            skCircle(sketch, "E8.0.27.29", {"center": v(122.1, 172.1) * mm, "radius": 2 * mm});
            skCircle(sketch, "E8.0.27.30", {"center": v(122.1, 188.1) * mm, "radius": 2 * mm});
            skCircle(sketch, "E8.0.27.31", {"center": v(122.1, 204.1) * mm, "radius": 2 * mm});
            skCircle(sketch, "E8.0.27.32", {"center": v(122.1, 220.1) * mm, "radius": 2 * mm});
            skCircle(sketch, "E8.0.27.33", {"center": v(122.1, 236.1) * mm, "radius": 2 * mm});
            skCircle(sketch, "E8.0.27.34", {"center": v(122.1, 252.1) * mm, "radius": 2 * mm});
            skCircle(sketch, "E8.0.27.35", {"center": v(122.1, 268.1) * mm, "radius": 2 * mm});
            skCircle(sketch, "E8.0.27.36", {"center": v(122.1, 284.1) * mm, "radius": 2 * mm});
            skCircle(sketch, "E8.0.27.37", {"center": v(122.1, 300.1) * mm, "radius": 2 * mm});
            skCircle(sketch, "E8.0.28.10", {"center": v(138.1, -131.9) * mm, "radius": 2 * mm});
            skCircle(sketch, "E8.0.28.11", {"center": v(138.1, -115.9) * mm, "radius": 2 * mm});
            skCircle(sketch, "E8.0.28.12", {"center": v(138.1, -99.9) * mm, "radius": 2 * mm});
            skCircle(sketch, "E8.0.28.13", {"center": v(138.1, -83.9) * mm, "radius": 2 * mm});
            skCircle(sketch, "E8.0.28.14", {"center": v(138.1, -67.9) * mm, "radius": 2 * mm});
            skCircle(sketch, "E8.0.28.15", {"center": v(138.1, -51.9) * mm, "radius": 2 * mm});
            skCircle(sketch, "E8.0.28.16", {"center": v(138.1, -35.9) * mm, "radius": 2 * mm});
            skCircle(sketch, "E8.0.28.17", {"center": v(138.1, -19.9) * mm, "radius": 2 * mm});
            skCircle(sketch, "E8.0.28.18", {"center": v(138.1, -3.9) * mm, "radius": 2 * mm});
            skCircle(sketch, "E8.0.28.19", {"center": v(138.1, 12.1) * mm, "radius": 2 * mm});
            skCircle(sketch, "E8.0.28.20", {"center": v(138.1, 28.1) * mm, "radius": 2 * mm});
            skCircle(sketch, "E8.0.28.21", {"center": v(138.1, 44.1) * mm, "radius": 2 * mm});
            skCircle(sketch, "E8.0.28.22", {"center": v(138.1, 60.1) * mm, "radius": 2 * mm});
            skCircle(sketch, "E8.0.28.23", {"center": v(138.1, 76.1) * mm, "radius": 2 * mm});
            skCircle(sketch, "E8.0.28.24", {"center": v(138.1, 92.1) * mm, "radius": 2 * mm});
            skCircle(sketch, "E8.0.28.25", {"center": v(138.1, 108.1) * mm, "radius": 2 * mm});
            skCircle(sketch, "E8.0.28.26", {"center": v(138.1, 124.1) * mm, "radius": 2 * mm});
            skCircle(sketch, "E8.0.28.27", {"center": v(138.1, 140.1) * mm, "radius": 2 * mm});
            skCircle(sketch, "E8.0.28.28", {"center": v(138.1, 156.1) * mm, "radius": 2 * mm});
            skCircle(sketch, "E8.0.28.29", {"center": v(138.1, 172.1) * mm, "radius": 2 * mm});
            skCircle(sketch, "E8.0.28.30", {"center": v(138.1, 188.1) * mm, "radius": 2 * mm});
            skCircle(sketch, "E8.0.28.31", {"center": v(138.1, 204.1) * mm, "radius": 2 * mm});
            skCircle(sketch, "E8.0.28.32", {"center": v(138.1, 220.1) * mm, "radius": 2 * mm});
            skCircle(sketch, "E8.0.28.33", {"center": v(138.1, 236.1) * mm, "radius": 2 * mm});
            skCircle(sketch, "E8.0.28.34", {"center": v(138.1, 252.1) * mm, "radius": 2 * mm});
            skCircle(sketch, "E8.0.28.35", {"center": v(138.1, 268.1) * mm, "radius": 2 * mm});
            skCircle(sketch, "E8.0.28.36", {"center": v(138.1, 284.1) * mm, "radius": 2 * mm});
            skCircle(sketch, "E8.0.28.37", {"center": v(138.1, 300.1) * mm, "radius": 2 * mm});
            skCircle(sketch, "E8.0.29.10", {"center": v(154.1, -131.9) * mm, "radius": 2 * mm});
            skCircle(sketch, "E8.0.29.11", {"center": v(154.1, -115.9) * mm, "radius": 2 * mm});
            skCircle(sketch, "E8.0.29.12", {"center": v(154.1, -99.9) * mm, "radius": 2 * mm});
            skCircle(sketch, "E8.0.29.13", {"center": v(154.1, -83.9) * mm, "radius": 2 * mm});
            skCircle(sketch, "E8.0.29.14", {"center": v(154.1, -67.9) * mm, "radius": 2 * mm});
            skCircle(sketch, "E8.0.29.15", {"center": v(154.1, -51.9) * mm, "radius": 2 * mm});
            skCircle(sketch, "E8.0.29.16", {"center": v(154.1, -35.9) * mm, "radius": 2 * mm});
            skCircle(sketch, "E8.0.29.17", {"center": v(154.1, -19.9) * mm, "radius": 2 * mm});
            skCircle(sketch, "E8.0.29.18", {"center": v(154.1, -3.9) * mm, "radius": 2 * mm});
            skCircle(sketch, "E8.0.29.19", {"center": v(154.1, 12.1) * mm, "radius": 2 * mm});
            skCircle(sketch, "E8.0.29.20", {"center": v(154.1, 28.1) * mm, "radius": 2 * mm});
            skCircle(sketch, "E8.0.29.21", {"center": v(154.1, 44.1) * mm, "radius": 2 * mm});
            skCircle(sketch, "E8.0.29.22", {"center": v(154.1, 60.1) * mm, "radius": 2 * mm});
            skCircle(sketch, "E8.0.29.23", {"center": v(154.1, 76.1) * mm, "radius": 2 * mm});
            skCircle(sketch, "E8.0.29.24", {"center": v(154.1, 92.1) * mm, "radius": 2 * mm});
            skCircle(sketch, "E8.0.29.25", {"center": v(154.1, 108.1) * mm, "radius": 2 * mm});
            skCircle(sketch, "E8.0.29.26", {"center": v(154.1, 124.1) * mm, "radius": 2 * mm});
            skCircle(sketch, "E8.0.29.27", {"center": v(154.1, 140.1) * mm, "radius": 2 * mm});
            skCircle(sketch, "E8.0.29.28", {"center": v(154.1, 156.1) * mm, "radius": 2 * mm});
            skCircle(sketch, "E8.0.29.29", {"center": v(154.1, 172.1) * mm, "radius": 2 * mm});
            skCircle(sketch, "E8.0.29.30", {"center": v(154.1, 188.1) * mm, "radius": 2 * mm});
            skCircle(sketch, "E8.0.29.31", {"center": v(154.1, 204.1) * mm, "radius": 2 * mm});
            skCircle(sketch, "E8.0.29.32", {"center": v(154.1, 220.1) * mm, "radius": 2 * mm});
            skCircle(sketch, "E8.0.29.33", {"center": v(154.1, 236.1) * mm, "radius": 2 * mm});
            skCircle(sketch, "E8.0.29.34", {"center": v(154.1, 252.1) * mm, "radius": 2 * mm});
            skCircle(sketch, "E8.0.29.35", {"center": v(154.1, 268.1) * mm, "radius": 2 * mm});
            skCircle(sketch, "E8.0.29.36", {"center": v(154.1, 284.1) * mm, "radius": 2 * mm});
            skCircle(sketch, "E8.0.29.37", {"center": v(154.1, 300.1) * mm, "radius": 2 * mm});
            skCircle(sketch, "E8.0.30.10", {"center": v(170.1, -131.9) * mm, "radius": 2 * mm});
            skCircle(sketch, "E8.0.30.11", {"center": v(170.1, -115.9) * mm, "radius": 2 * mm});
            skCircle(sketch, "E8.0.30.12", {"center": v(170.1, -99.9) * mm, "radius": 2 * mm});
            skCircle(sketch, "E8.0.30.13", {"center": v(170.1, -83.9) * mm, "radius": 2 * mm});
            skCircle(sketch, "E8.0.30.14", {"center": v(170.1, -67.9) * mm, "radius": 2 * mm});
            skCircle(sketch, "E8.0.30.15", {"center": v(170.1, -51.9) * mm, "radius": 2 * mm});
            skCircle(sketch, "E8.0.30.16", {"center": v(170.1, -35.9) * mm, "radius": 2 * mm});
            skCircle(sketch, "E8.0.30.17", {"center": v(170.1, -19.9) * mm, "radius": 2 * mm});
            skCircle(sketch, "E8.0.30.18", {"center": v(170.1, -3.9) * mm, "radius": 2 * mm});
            skCircle(sketch, "E8.0.30.19", {"center": v(170.1, 12.1) * mm, "radius": 2 * mm});
            skCircle(sketch, "E8.0.30.20", {"center": v(170.1, 28.1) * mm, "radius": 2 * mm});
            skCircle(sketch, "E8.0.30.21", {"center": v(170.1, 44.1) * mm, "radius": 2 * mm});
            skCircle(sketch, "E8.0.30.22", {"center": v(170.1, 60.1) * mm, "radius": 2 * mm});
            skCircle(sketch, "E8.0.30.23", {"center": v(170.1, 76.1) * mm, "radius": 2 * mm});
            skCircle(sketch, "E8.0.30.24", {"center": v(170.1, 92.1) * mm, "radius": 2 * mm});
            skCircle(sketch, "E8.0.30.25", {"center": v(170.1, 108.1) * mm, "radius": 2 * mm});
            skCircle(sketch, "E8.0.30.26", {"center": v(170.1, 124.1) * mm, "radius": 2 * mm});
            skCircle(sketch, "E8.0.30.27", {"center": v(170.1, 140.1) * mm, "radius": 2 * mm});
            skCircle(sketch, "E8.0.30.28", {"center": v(170.1, 156.1) * mm, "radius": 2 * mm});
            skCircle(sketch, "E8.0.30.29", {"center": v(170.1, 172.1) * mm, "radius": 2 * mm});
            skCircle(sketch, "E8.0.30.30", {"center": v(170.1, 188.1) * mm, "radius": 2 * mm});
            skCircle(sketch, "E8.0.30.31", {"center": v(170.1, 204.1) * mm, "radius": 2 * mm});
            skCircle(sketch, "E8.0.30.32", {"center": v(170.1, 220.1) * mm, "radius": 2 * mm});
            skCircle(sketch, "E8.0.30.33", {"center": v(170.1, 236.1) * mm, "radius": 2 * mm});
            skCircle(sketch, "E8.0.30.34", {"center": v(170.1, 252.1) * mm, "radius": 2 * mm});
            skCircle(sketch, "E8.0.30.35", {"center": v(170.1, 268.1) * mm, "radius": 2 * mm});
            skCircle(sketch, "E8.0.30.36", {"center": v(170.1, 284.1) * mm, "radius": 2 * mm});
            skCircle(sketch, "E8.0.30.37", {"center": v(170.1, 300.1) * mm, "radius": 2 * mm});
            skCircle(sketch, "E8.0.31.10", {"center": v(186.1, -131.9) * mm, "radius": 2 * mm});
            skCircle(sketch, "E8.0.31.11", {"center": v(186.1, -115.9) * mm, "radius": 2 * mm});
            skCircle(sketch, "E8.0.31.12", {"center": v(186.1, -99.9) * mm, "radius": 2 * mm});
            skCircle(sketch, "E8.0.31.13", {"center": v(186.1, -83.9) * mm, "radius": 2 * mm});
            skCircle(sketch, "E8.0.31.14", {"center": v(186.1, -67.9) * mm, "radius": 2 * mm});
            skCircle(sketch, "E8.0.31.15", {"center": v(186.1, -51.9) * mm, "radius": 2 * mm});
            skCircle(sketch, "E8.0.31.16", {"center": v(186.1, -35.9) * mm, "radius": 2 * mm});
            skCircle(sketch, "E8.0.31.17", {"center": v(186.1, -19.9) * mm, "radius": 2 * mm});
            skCircle(sketch, "E8.0.31.18", {"center": v(186.1, -3.9) * mm, "radius": 2 * mm});
            skCircle(sketch, "E8.0.31.19", {"center": v(186.1, 12.1) * mm, "radius": 2 * mm});
            skCircle(sketch, "E8.0.31.20", {"center": v(186.1, 28.1) * mm, "radius": 2 * mm});
            skCircle(sketch, "E8.0.31.21", {"center": v(186.1, 44.1) * mm, "radius": 2 * mm});
            skCircle(sketch, "E8.0.31.22", {"center": v(186.1, 60.1) * mm, "radius": 2 * mm});
            skCircle(sketch, "E8.0.31.23", {"center": v(186.1, 76.1) * mm, "radius": 2 * mm});
            skCircle(sketch, "E8.0.31.24", {"center": v(186.1, 92.1) * mm, "radius": 2 * mm});
            skCircle(sketch, "E8.0.31.25", {"center": v(186.1, 108.1) * mm, "radius": 2 * mm});
            skCircle(sketch, "E8.0.31.26", {"center": v(186.1, 124.1) * mm, "radius": 2 * mm});
            skCircle(sketch, "E8.0.31.27", {"center": v(186.1, 140.1) * mm, "radius": 2 * mm});
            skCircle(sketch, "E8.0.31.28", {"center": v(186.1, 156.1) * mm, "radius": 2 * mm});
            skCircle(sketch, "E8.0.31.29", {"center": v(186.1, 172.1) * mm, "radius": 2 * mm});
            skCircle(sketch, "E8.0.31.30", {"center": v(186.1, 188.1) * mm, "radius": 2 * mm});
            skCircle(sketch, "E8.0.31.31", {"center": v(186.1, 204.1) * mm, "radius": 2 * mm});
            skCircle(sketch, "E8.0.31.32", {"center": v(186.1, 220.1) * mm, "radius": 2 * mm});
            skCircle(sketch, "E8.0.31.33", {"center": v(186.1, 236.1) * mm, "radius": 2 * mm});
            skCircle(sketch, "E8.0.31.34", {"center": v(186.1, 252.1) * mm, "radius": 2 * mm});
            skCircle(sketch, "E8.0.31.35", {"center": v(186.1, 268.1) * mm, "radius": 2 * mm});
            skCircle(sketch, "E8.0.31.36", {"center": v(186.1, 284.1) * mm, "radius": 2 * mm});
            skCircle(sketch, "E8.0.31.37", {"center": v(186.1, 300.1) * mm, "radius": 2 * mm});
            skCircle(sketch, "E8.0.32.10", {"center": v(202.1, -131.9) * mm, "radius": 2 * mm});
            skCircle(sketch, "E8.0.32.11", {"center": v(202.1, -115.9) * mm, "radius": 2 * mm});
            skCircle(sketch, "E8.0.32.12", {"center": v(202.1, -99.9) * mm, "radius": 2 * mm});
            skCircle(sketch, "E8.0.32.13", {"center": v(202.1, -83.9) * mm, "radius": 2 * mm});
            skCircle(sketch, "E8.0.32.14", {"center": v(202.1, -67.9) * mm, "radius": 2 * mm});
            skCircle(sketch, "E8.0.32.15", {"center": v(202.1, -51.9) * mm, "radius": 2 * mm});
            skCircle(sketch, "E8.0.32.16", {"center": v(202.1, -35.9) * mm, "radius": 2 * mm});
            skCircle(sketch, "E8.0.32.17", {"center": v(202.1, -19.9) * mm, "radius": 2 * mm});
            skCircle(sketch, "E8.0.32.18", {"center": v(202.1, -3.9) * mm, "radius": 2 * mm});
            skCircle(sketch, "E8.0.32.19", {"center": v(202.1, 12.1) * mm, "radius": 2 * mm});
            skCircle(sketch, "E8.0.32.20", {"center": v(202.1, 28.1) * mm, "radius": 2 * mm});
            skCircle(sketch, "E8.0.32.21", {"center": v(202.1, 44.1) * mm, "radius": 2 * mm});
            skCircle(sketch, "E8.0.32.22", {"center": v(202.1, 60.1) * mm, "radius": 2 * mm});
            skCircle(sketch, "E8.0.32.23", {"center": v(202.1, 76.1) * mm, "radius": 2 * mm});
            skCircle(sketch, "E8.0.32.24", {"center": v(202.1, 92.1) * mm, "radius": 2 * mm});
            skCircle(sketch, "E8.0.32.25", {"center": v(202.1, 108.1) * mm, "radius": 2 * mm});
            skCircle(sketch, "E8.0.32.26", {"center": v(202.1, 124.1) * mm, "radius": 2 * mm});
            skCircle(sketch, "E8.0.32.27", {"center": v(202.1, 140.1) * mm, "radius": 2 * mm});
            skCircle(sketch, "E8.0.32.28", {"center": v(202.1, 156.1) * mm, "radius": 2 * mm});
            skCircle(sketch, "E8.0.32.29", {"center": v(202.1, 172.1) * mm, "radius": 2 * mm});
            skCircle(sketch, "E8.0.32.30", {"center": v(202.1, 188.1) * mm, "radius": 2 * mm});
            skCircle(sketch, "E8.0.32.31", {"center": v(202.1, 204.1) * mm, "radius": 2 * mm});
            skCircle(sketch, "E8.0.32.32", {"center": v(202.1, 220.1) * mm, "radius": 2 * mm});
            skCircle(sketch, "E8.0.32.33", {"center": v(202.1, 236.1) * mm, "radius": 2 * mm});
            skCircle(sketch, "E8.0.32.34", {"center": v(202.1, 252.1) * mm, "radius": 2 * mm});
            skCircle(sketch, "E8.0.32.35", {"center": v(202.1, 268.1) * mm, "radius": 2 * mm});
            skCircle(sketch, "E8.0.32.36", {"center": v(202.1, 284.1) * mm, "radius": 2 * mm});
            skCircle(sketch, "E8.0.32.37", {"center": v(202.1, 300.1) * mm, "radius": 2 * mm});
            skCircle(sketch, "E8.0.33.10", {"center": v(218.1, -131.9) * mm, "radius": 2 * mm});
            skCircle(sketch, "E8.0.33.11", {"center": v(218.1, -115.9) * mm, "radius": 2 * mm});
            skCircle(sketch, "E8.0.33.12", {"center": v(218.1, -99.9) * mm, "radius": 2 * mm});
            skCircle(sketch, "E8.0.33.13", {"center": v(218.1, -83.9) * mm, "radius": 2 * mm});
            skCircle(sketch, "E8.0.33.14", {"center": v(218.1, -67.9) * mm, "radius": 2 * mm});
            skCircle(sketch, "E8.0.33.15", {"center": v(218.1, -51.9) * mm, "radius": 2 * mm});
            skCircle(sketch, "E8.0.33.16", {"center": v(218.1, -35.9) * mm, "radius": 2 * mm});
            skCircle(sketch, "E8.0.33.17", {"center": v(218.1, -19.9) * mm, "radius": 2 * mm});
            skCircle(sketch, "E8.0.33.18", {"center": v(218.1, -3.9) * mm, "radius": 2 * mm});
            skCircle(sketch, "E8.0.33.19", {"center": v(218.1, 12.1) * mm, "radius": 2 * mm});
            skCircle(sketch, "E8.0.33.20", {"center": v(218.1, 28.1) * mm, "radius": 2 * mm});
            skCircle(sketch, "E8.0.33.21", {"center": v(218.1, 44.1) * mm, "radius": 2 * mm});
            skCircle(sketch, "E8.0.33.22", {"center": v(218.1, 60.1) * mm, "radius": 2 * mm});
            skCircle(sketch, "E8.0.33.23", {"center": v(218.1, 76.1) * mm, "radius": 2 * mm});
            skCircle(sketch, "E8.0.33.24", {"center": v(218.1, 92.1) * mm, "radius": 2 * mm});
            skCircle(sketch, "E8.0.33.25", {"center": v(218.1, 108.1) * mm, "radius": 2 * mm});
            skCircle(sketch, "E8.0.33.26", {"center": v(218.1, 124.1) * mm, "radius": 2 * mm});
            skCircle(sketch, "E8.0.33.27", {"center": v(218.1, 140.1) * mm, "radius": 2 * mm});
            skCircle(sketch, "E8.0.33.28", {"center": v(218.1, 156.1) * mm, "radius": 2 * mm});
            skCircle(sketch, "E8.0.33.29", {"center": v(218.1, 172.1) * mm, "radius": 2 * mm});
            skCircle(sketch, "E8.0.33.30", {"center": v(218.1, 188.1) * mm, "radius": 2 * mm});
            skCircle(sketch, "E8.0.33.31", {"center": v(218.1, 204.1) * mm, "radius": 2 * mm});
            skCircle(sketch, "E8.0.33.32", {"center": v(218.1, 220.1) * mm, "radius": 2 * mm});
            skCircle(sketch, "E8.0.33.33", {"center": v(218.1, 236.1) * mm, "radius": 2 * mm});
            skCircle(sketch, "E8.0.33.34", {"center": v(218.1, 252.1) * mm, "radius": 2 * mm});
            skCircle(sketch, "E8.0.33.35", {"center": v(218.1, 268.1) * mm, "radius": 2 * mm});
            skCircle(sketch, "E8.0.33.36", {"center": v(218.1, 284.1) * mm, "radius": 2 * mm});
            skCircle(sketch, "E8.0.33.37", {"center": v(218.1, 300.1) * mm, "radius": 2 * mm});
            skCircle(sketch, "E8.0.34.10", {"center": v(234.1, -131.9) * mm, "radius": 2 * mm});
            skCircle(sketch, "E8.0.34.11", {"center": v(234.1, -115.9) * mm, "radius": 2 * mm});
            skCircle(sketch, "E8.0.34.12", {"center": v(234.1, -99.9) * mm, "radius": 2 * mm});
            skCircle(sketch, "E8.0.34.13", {"center": v(234.1, -83.9) * mm, "radius": 2 * mm});
            skCircle(sketch, "E8.0.34.14", {"center": v(234.1, -67.9) * mm, "radius": 2 * mm});
            skCircle(sketch, "E8.0.34.15", {"center": v(234.1, -51.9) * mm, "radius": 2 * mm});
            skCircle(sketch, "E8.0.34.16", {"center": v(234.1, -35.9) * mm, "radius": 2 * mm});
            skCircle(sketch, "E8.0.34.17", {"center": v(234.1, -19.9) * mm, "radius": 2 * mm});
            skCircle(sketch, "E8.0.34.18", {"center": v(234.1, -3.9) * mm, "radius": 2 * mm});
            skCircle(sketch, "E8.0.34.19", {"center": v(234.1, 12.1) * mm, "radius": 2 * mm});
            skCircle(sketch, "E8.0.34.20", {"center": v(234.1, 28.1) * mm, "radius": 2 * mm});
            skCircle(sketch, "E8.0.34.21", {"center": v(234.1, 44.1) * mm, "radius": 2 * mm});
            skCircle(sketch, "E8.0.34.22", {"center": v(234.1, 60.1) * mm, "radius": 2 * mm});
            skCircle(sketch, "E8.0.34.23", {"center": v(234.1, 76.1) * mm, "radius": 2 * mm});
            skCircle(sketch, "E8.0.34.24", {"center": v(234.1, 92.1) * mm, "radius": 2 * mm});
            skCircle(sketch, "E8.0.34.25", {"center": v(234.1, 108.1) * mm, "radius": 2 * mm});
            skCircle(sketch, "E8.0.34.26", {"center": v(234.1, 124.1) * mm, "radius": 2 * mm});
            skCircle(sketch, "E8.0.34.27", {"center": v(234.1, 140.1) * mm, "radius": 2 * mm});
            skCircle(sketch, "E8.0.34.28", {"center": v(234.1, 156.1) * mm, "radius": 2 * mm});
            skCircle(sketch, "E8.0.34.29", {"center": v(234.1, 172.1) * mm, "radius": 2 * mm});
            skCircle(sketch, "E8.0.34.30", {"center": v(234.1, 188.1) * mm, "radius": 2 * mm});
            skCircle(sketch, "E8.0.34.31", {"center": v(234.1, 204.1) * mm, "radius": 2 * mm});
            skCircle(sketch, "E8.0.34.32", {"center": v(234.1, 220.1) * mm, "radius": 2 * mm});
            skCircle(sketch, "E8.0.34.33", {"center": v(234.1, 236.1) * mm, "radius": 2 * mm});
            skCircle(sketch, "E8.0.34.34", {"center": v(234.1, 252.1) * mm, "radius": 2 * mm});
            skCircle(sketch, "E8.0.34.35", {"center": v(234.1, 268.1) * mm, "radius": 2 * mm});
            skCircle(sketch, "E8.0.34.36", {"center": v(234.1, 284.1) * mm, "radius": 2 * mm});
            skCircle(sketch, "E8.0.34.37", {"center": v(234.1, 300.1) * mm, "radius": 2 * mm});
            skCircle(sketch, "E8.0.35.10", {"center": v(250.1, -131.9) * mm, "radius": 2 * mm});
            skCircle(sketch, "E8.0.35.11", {"center": v(250.1, -115.9) * mm, "radius": 2 * mm});
            skCircle(sketch, "E8.0.35.12", {"center": v(250.1, -99.9) * mm, "radius": 2 * mm});
            skCircle(sketch, "E8.0.35.13", {"center": v(250.1, -83.9) * mm, "radius": 2 * mm});
            skCircle(sketch, "E8.0.35.14", {"center": v(250.1, -67.9) * mm, "radius": 2 * mm});
            skCircle(sketch, "E8.0.35.15", {"center": v(250.1, -51.9) * mm, "radius": 2 * mm});
            skCircle(sketch, "E8.0.35.16", {"center": v(250.1, -35.9) * mm, "radius": 2 * mm});
            skCircle(sketch, "E8.0.35.17", {"center": v(250.1, -19.9) * mm, "radius": 2 * mm});
            skCircle(sketch, "E8.0.35.18", {"center": v(250.1, -3.9) * mm, "radius": 2 * mm});
            skCircle(sketch, "E8.0.35.19", {"center": v(250.1, 12.1) * mm, "radius": 2 * mm});
            skCircle(sketch, "E8.0.35.20", {"center": v(250.1, 28.1) * mm, "radius": 2 * mm});
            skCircle(sketch, "E8.0.35.21", {"center": v(250.1, 44.1) * mm, "radius": 2 * mm});
            skCircle(sketch, "E8.0.35.22", {"center": v(250.1, 60.1) * mm, "radius": 2 * mm});
            skCircle(sketch, "E8.0.35.23", {"center": v(250.1, 76.1) * mm, "radius": 2 * mm});
            skCircle(sketch, "E8.0.35.24", {"center": v(250.1, 92.1) * mm, "radius": 2 * mm});
            skCircle(sketch, "E8.0.35.25", {"center": v(250.1, 108.1) * mm, "radius": 2 * mm});
            skCircle(sketch, "E8.0.35.26", {"center": v(250.1, 124.1) * mm, "radius": 2 * mm});
            skCircle(sketch, "E8.0.35.27", {"center": v(250.1, 140.1) * mm, "radius": 2 * mm});
            skCircle(sketch, "E8.0.35.28", {"center": v(250.1, 156.1) * mm, "radius": 2 * mm});
            skCircle(sketch, "E8.0.35.29", {"center": v(250.1, 172.1) * mm, "radius": 2 * mm});
            skCircle(sketch, "E8.0.35.30", {"center": v(250.1, 188.1) * mm, "radius": 2 * mm});
            skCircle(sketch, "E8.0.35.31", {"center": v(250.1, 204.1) * mm, "radius": 2 * mm});
            skCircle(sketch, "E8.0.35.32", {"center": v(250.1, 220.1) * mm, "radius": 2 * mm});
            skCircle(sketch, "E8.0.35.33", {"center": v(250.1, 236.1) * mm, "radius": 2 * mm});
            skCircle(sketch, "E8.0.35.34", {"center": v(250.1, 252.1) * mm, "radius": 2 * mm});
            skCircle(sketch, "E8.0.35.35", {"center": v(250.1, 268.1) * mm, "radius": 2 * mm});
            skCircle(sketch, "E8.0.35.36", {"center": v(250.1, 284.1) * mm, "radius": 2 * mm});
            skCircle(sketch, "E8.0.35.37", {"center": v(250.1, 300.1) * mm, "radius": 2 * mm});
            skCircle(sketch, "E8.0.36.10", {"center": v(266.1, -131.9) * mm, "radius": 2 * mm});
            skCircle(sketch, "E8.0.36.11", {"center": v(266.1, -115.9) * mm, "radius": 2 * mm});
            skCircle(sketch, "E8.0.36.12", {"center": v(266.1, -99.9) * mm, "radius": 2 * mm});
            skCircle(sketch, "E8.0.36.13", {"center": v(266.1, -83.9) * mm, "radius": 2 * mm});
            skCircle(sketch, "E8.0.36.14", {"center": v(266.1, -67.9) * mm, "radius": 2 * mm});
            skCircle(sketch, "E8.0.36.15", {"center": v(266.1, -51.9) * mm, "radius": 2 * mm});
            skCircle(sketch, "E8.0.36.16", {"center": v(266.1, -35.9) * mm, "radius": 2 * mm});
            skCircle(sketch, "E8.0.36.17", {"center": v(266.1, -19.9) * mm, "radius": 2 * mm});
            skCircle(sketch, "E8.0.36.18", {"center": v(266.1, -3.9) * mm, "radius": 2 * mm});
            skCircle(sketch, "E8.0.36.19", {"center": v(266.1, 12.1) * mm, "radius": 2 * mm});
            skCircle(sketch, "E8.0.36.20", {"center": v(266.1, 28.1) * mm, "radius": 2 * mm});
            skCircle(sketch, "E8.0.36.21", {"center": v(266.1, 44.1) * mm, "radius": 2 * mm});
            skCircle(sketch, "E8.0.36.22", {"center": v(266.1, 60.1) * mm, "radius": 2 * mm});
            skCircle(sketch, "E8.0.36.23", {"center": v(266.1, 76.1) * mm, "radius": 2 * mm});
            skCircle(sketch, "E8.0.36.24", {"center": v(266.1, 92.1) * mm, "radius": 2 * mm});
            skCircle(sketch, "E8.0.36.25", {"center": v(266.1, 108.1) * mm, "radius": 2 * mm});
            skCircle(sketch, "E8.0.36.26", {"center": v(266.1, 124.1) * mm, "radius": 2 * mm});
            skCircle(sketch, "E8.0.36.27", {"center": v(266.1, 140.1) * mm, "radius": 2 * mm});
            skCircle(sketch, "E8.0.36.28", {"center": v(266.1, 156.1) * mm, "radius": 2 * mm});
            skCircle(sketch, "E8.0.36.29", {"center": v(266.1, 172.1) * mm, "radius": 2 * mm});
            skCircle(sketch, "E8.0.36.30", {"center": v(266.1, 188.1) * mm, "radius": 2 * mm});
            skCircle(sketch, "E8.0.36.31", {"center": v(266.1, 204.1) * mm, "radius": 2 * mm});
            skCircle(sketch, "E8.0.36.32", {"center": v(266.1, 220.1) * mm, "radius": 2 * mm});
            skCircle(sketch, "E8.0.36.33", {"center": v(266.1, 236.1) * mm, "radius": 2 * mm});
            skCircle(sketch, "E8.0.36.34", {"center": v(266.1, 252.1) * mm, "radius": 2 * mm});
            skCircle(sketch, "E8.0.36.35", {"center": v(266.1, 268.1) * mm, "radius": 2 * mm});
            skCircle(sketch, "E8.0.36.36", {"center": v(266.1, 284.1) * mm, "radius": 2 * mm});
            skCircle(sketch, "E8.0.36.37", {"center": v(266.1, 300.1) * mm, "radius": 2 * mm});
            skCircle(sketch, "E8.0.37.10", {"center": v(282.1, -131.9) * mm, "radius": 2 * mm});
            skCircle(sketch, "E8.0.37.11", {"center": v(282.1, -115.9) * mm, "radius": 2 * mm});
            skCircle(sketch, "E8.0.37.12", {"center": v(282.1, -99.9) * mm, "radius": 2 * mm});
            skCircle(sketch, "E8.0.37.13", {"center": v(282.1, -83.9) * mm, "radius": 2 * mm});
            skCircle(sketch, "E8.0.37.14", {"center": v(282.1, -67.9) * mm, "radius": 2 * mm});
            skCircle(sketch, "E8.0.37.15", {"center": v(282.1, -51.9) * mm, "radius": 2 * mm});
            skCircle(sketch, "E8.0.37.16", {"center": v(282.1, -35.9) * mm, "radius": 2 * mm});
            skCircle(sketch, "E8.0.37.17", {"center": v(282.1, -19.9) * mm, "radius": 2 * mm});
            skCircle(sketch, "E8.0.37.18", {"center": v(282.1, -3.9) * mm, "radius": 2 * mm});
            skCircle(sketch, "E8.0.37.19", {"center": v(282.1, 12.1) * mm, "radius": 2 * mm});
            skCircle(sketch, "E8.0.37.20", {"center": v(282.1, 28.1) * mm, "radius": 2 * mm});
            skCircle(sketch, "E8.0.37.21", {"center": v(282.1, 44.1) * mm, "radius": 2 * mm});
            skCircle(sketch, "E8.0.37.22", {"center": v(282.1, 60.1) * mm, "radius": 2 * mm});
            skCircle(sketch, "E8.0.37.23", {"center": v(282.1, 76.1) * mm, "radius": 2 * mm});
            skCircle(sketch, "E8.0.37.24", {"center": v(282.1, 92.1) * mm, "radius": 2 * mm});
            skCircle(sketch, "E8.0.37.25", {"center": v(282.1, 108.1) * mm, "radius": 2 * mm});
            skCircle(sketch, "E8.0.37.26", {"center": v(282.1, 124.1) * mm, "radius": 2 * mm});
            skCircle(sketch, "E8.0.37.27", {"center": v(282.1, 140.1) * mm, "radius": 2 * mm});
            skCircle(sketch, "E8.0.37.28", {"center": v(282.1, 156.1) * mm, "radius": 2 * mm});
            skCircle(sketch, "E8.0.37.29", {"center": v(282.1, 172.1) * mm, "radius": 2 * mm});
            skCircle(sketch, "E8.0.37.30", {"center": v(282.1, 188.1) * mm, "radius": 2 * mm});
            skCircle(sketch, "E8.0.37.31", {"center": v(282.1, 204.1) * mm, "radius": 2 * mm});
            skCircle(sketch, "E8.0.37.32", {"center": v(282.1, 220.1) * mm, "radius": 2 * mm});
            skCircle(sketch, "E8.0.37.33", {"center": v(282.1, 236.1) * mm, "radius": 2 * mm});
            skCircle(sketch, "E8.0.37.34", {"center": v(282.1, 252.1) * mm, "radius": 2 * mm});
            skCircle(sketch, "E8.0.37.35", {"center": v(282.1, 268.1) * mm, "radius": 2 * mm});
            skCircle(sketch, "E8.0.37.36", {"center": v(282.1, 284.1) * mm, "radius": 2 * mm});
            skCircle(sketch, "E8.0.37.37", {"center": v(282.1, 300.1) * mm, "radius": 2 * mm});
            skCircle(sketch, "E8.0.38.10", {"center": v(298.1, -131.9) * mm, "radius": 2 * mm});
            skCircle(sketch, "E8.0.38.11", {"center": v(298.1, -115.9) * mm, "radius": 2 * mm});
            skCircle(sketch, "E8.0.38.12", {"center": v(298.1, -99.9) * mm, "radius": 2 * mm});
            skCircle(sketch, "E8.0.38.13", {"center": v(298.1, -83.9) * mm, "radius": 2 * mm});
            skCircle(sketch, "E8.0.38.14", {"center": v(298.1, -67.9) * mm, "radius": 2 * mm});
            skCircle(sketch, "E8.0.38.15", {"center": v(298.1, -51.9) * mm, "radius": 2 * mm});
            skCircle(sketch, "E8.0.38.16", {"center": v(298.1, -35.9) * mm, "radius": 2 * mm});
            skCircle(sketch, "E8.0.38.17", {"center": v(298.1, -19.9) * mm, "radius": 2 * mm});
            skCircle(sketch, "E8.0.38.18", {"center": v(298.1, -3.9) * mm, "radius": 2 * mm});
            skCircle(sketch, "E8.0.38.19", {"center": v(298.1, 12.1) * mm, "radius": 2 * mm});
            skCircle(sketch, "E8.0.38.20", {"center": v(298.1, 28.1) * mm, "radius": 2 * mm});
            skCircle(sketch, "E8.0.38.21", {"center": v(298.1, 44.1) * mm, "radius": 2 * mm});
            skCircle(sketch, "E8.0.38.22", {"center": v(298.1, 60.1) * mm, "radius": 2 * mm});
            skCircle(sketch, "E8.0.38.23", {"center": v(298.1, 76.1) * mm, "radius": 2 * mm});
            skCircle(sketch, "E8.0.38.24", {"center": v(298.1, 92.1) * mm, "radius": 2 * mm});
            skCircle(sketch, "E8.0.38.25", {"center": v(298.1, 108.1) * mm, "radius": 2 * mm});
            skCircle(sketch, "E8.0.38.26", {"center": v(298.1, 124.1) * mm, "radius": 2 * mm});
            skCircle(sketch, "E8.0.38.27", {"center": v(298.1, 140.1) * mm, "radius": 2 * mm});
            skCircle(sketch, "E8.0.38.28", {"center": v(298.1, 156.1) * mm, "radius": 2 * mm});
            skCircle(sketch, "E8.0.38.29", {"center": v(298.1, 172.1) * mm, "radius": 2 * mm});
            skCircle(sketch, "E8.0.38.30", {"center": v(298.1, 188.1) * mm, "radius": 2 * mm});
            skCircle(sketch, "E8.0.38.31", {"center": v(298.1, 204.1) * mm, "radius": 2 * mm});
            skCircle(sketch, "E8.0.38.32", {"center": v(298.1, 220.1) * mm, "radius": 2 * mm});
            skCircle(sketch, "E8.0.38.33", {"center": v(298.1, 236.1) * mm, "radius": 2 * mm});
            skCircle(sketch, "E8.0.38.34", {"center": v(298.1, 252.1) * mm, "radius": 2 * mm});
            skCircle(sketch, "E8.0.38.35", {"center": v(298.1, 268.1) * mm, "radius": 2 * mm});
            skCircle(sketch, "E8.0.38.36", {"center": v(298.1, 284.1) * mm, "radius": 2 * mm});
            skCircle(sketch, "E8.0.38.37", {"center": v(298.1, 300.1) * mm, "radius": 2 * mm});
            skCircle(sketch, "E8.0.39.10", {"center": v(314.1, -131.9) * mm, "radius": 2 * mm});
            skCircle(sketch, "E8.0.39.11", {"center": v(314.1, -115.9) * mm, "radius": 2 * mm});
            skCircle(sketch, "E8.0.39.12", {"center": v(314.1, -99.9) * mm, "radius": 2 * mm});
            skCircle(sketch, "E8.0.39.13", {"center": v(314.1, -83.9) * mm, "radius": 2 * mm});
            skCircle(sketch, "E8.0.39.14", {"center": v(314.1, -67.9) * mm, "radius": 2 * mm});
            skCircle(sketch, "E8.0.39.15", {"center": v(314.1, -51.9) * mm, "radius": 2 * mm});
            skCircle(sketch, "E8.0.39.16", {"center": v(314.1, -35.9) * mm, "radius": 2 * mm});
            skCircle(sketch, "E8.0.39.17", {"center": v(314.1, -19.9) * mm, "radius": 2 * mm});
            skCircle(sketch, "E8.0.39.18", {"center": v(314.1, -3.9) * mm, "radius": 2 * mm});
            skCircle(sketch, "E8.0.39.19", {"center": v(314.1, 12.1) * mm, "radius": 2 * mm});
            skCircle(sketch, "E8.0.39.20", {"center": v(314.1, 28.1) * mm, "radius": 2 * mm});
            skCircle(sketch, "E8.0.39.21", {"center": v(314.1, 44.1) * mm, "radius": 2 * mm});
            skCircle(sketch, "E8.0.39.22", {"center": v(314.1, 60.1) * mm, "radius": 2 * mm});
            skCircle(sketch, "E8.0.39.23", {"center": v(314.1, 76.1) * mm, "radius": 2 * mm});
            skCircle(sketch, "E8.0.39.24", {"center": v(314.1, 92.1) * mm, "radius": 2 * mm});
            skCircle(sketch, "E8.0.39.25", {"center": v(314.1, 108.1) * mm, "radius": 2 * mm});
            skCircle(sketch, "E8.0.39.26", {"center": v(314.1, 124.1) * mm, "radius": 2 * mm});
            skCircle(sketch, "E8.0.39.27", {"center": v(314.1, 140.1) * mm, "radius": 2 * mm});
            skCircle(sketch, "E8.0.39.28", {"center": v(314.1, 156.1) * mm, "radius": 2 * mm});
            skCircle(sketch, "E8.0.39.29", {"center": v(314.1, 172.1) * mm, "radius": 2 * mm});
            skCircle(sketch, "E8.0.39.30", {"center": v(314.1, 188.1) * mm, "radius": 2 * mm});
            skCircle(sketch, "E8.0.39.31", {"center": v(314.1, 204.1) * mm, "radius": 2 * mm});
            skCircle(sketch, "E8.0.39.32", {"center": v(314.1, 220.1) * mm, "radius": 2 * mm});
            skCircle(sketch, "E8.0.39.33", {"center": v(314.1, 236.1) * mm, "radius": 2 * mm});
            skCircle(sketch, "E8.0.39.34", {"center": v(314.1, 252.1) * mm, "radius": 2 * mm});
            skCircle(sketch, "E8.0.39.35", {"center": v(314.1, 268.1) * mm, "radius": 2 * mm});
            skCircle(sketch, "E8.0.39.36", {"center": v(314.1, 284.1) * mm, "radius": 2 * mm});
            skCircle(sketch, "E8.0.39.37", {"center": v(314.1, 300.1) * mm, "radius": 2 * mm});
            skSolve(sketch);
        }
        {
            var Q0;
            {var subQ131=sQuery(id+"F0.wireOp",EDGE,"E0.right");Q0=makeQuery(id+"F0.imprint","IMPRINT",FACE,{"disambiguationData":[TD([[makeQuery(id+"F0.imprint","IMPRINT",EDGE,{"derivedFrom":subQ131}),-1.0]])]});}
            extrude(context, id + "F1", {"entities" : qUnion([Q0]), "depth" : 1 * mm, "offsetDistance" : 25 * mm});
        }
    });
